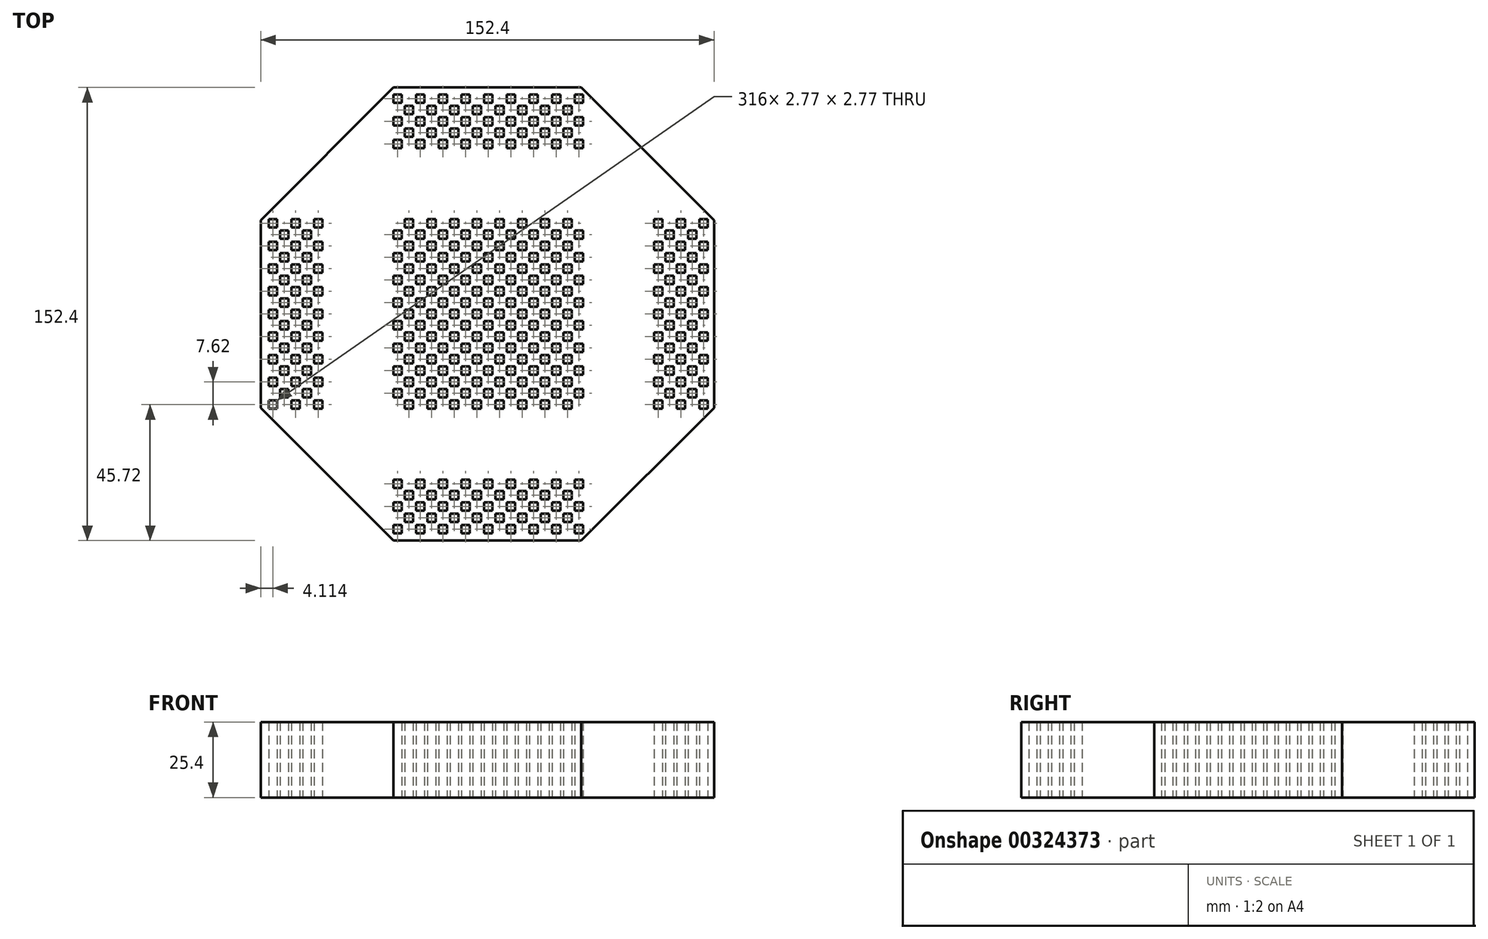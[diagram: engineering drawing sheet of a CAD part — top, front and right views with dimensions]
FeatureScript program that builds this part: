
annotation { "Feature Type Name" : "Feature", "Feature Type Description" : "" }
export const myFeature = defineFeature(function(context is Context, id is Id, definition is map)
    precondition{}
    {
        {
            var Q0;
            Q0=qCreatedBy(makeId("Top.planeOp"),FACE);
            var sketch = newSketch(context, id + "F0", { "sketchPlane" : qUnion([Q0])});
            skLineSegment(sketch, "E0.0", {"start": v(-31.56, 76.2) * mm, "end": v(31.56, 76.2) * mm});
            skLineSegment(sketch, "E0.1", {"start": v(31.56, 76.2) * mm, "end": v(76.2, 31.56) * mm});
            skLineSegment(sketch, "E0.2", {"start": v(76.2, 31.56) * mm, "end": v(76.2, -31.56) * mm});
            skLineSegment(sketch, "E0.3", {"start": v(76.2, -31.56) * mm, "end": v(31.56, -76.2) * mm});
            skLineSegment(sketch, "E0.4", {"start": v(31.56, -76.2) * mm, "end": v(-31.56, -76.2) * mm});
            skLineSegment(sketch, "E0.5", {"start": v(-31.56, -76.2) * mm, "end": v(-76.2, -31.56) * mm});
            skLineSegment(sketch, "E0.6", {"start": v(-76.2, -31.56) * mm, "end": v(-76.2, 31.56) * mm});
            skLineSegment(sketch, "E0.7", {"start": v(-76.2, 31.56) * mm, "end": v(-31.56, 76.2) * mm});
            skPoint(sketch, "E0.0.midPoint", {"position": v(0, 76.2) * mm});
            skPoint(sketch, "E0.cCircle.center.orphan", {"position": v(0, 0) * mm});
            skLineSegment(sketch, "E1.bottom", {"start": v(-31.56, 73.78) * mm, "end": v(-28.79, 73.78) * mm});
            skLineSegment(sketch, "E1.top", {"start": v(-31.56, 71) * mm, "end": v(-28.79, 71) * mm});
            skLineSegment(sketch, "E1.left", {"start": v(-31.56, 73.78) * mm, "end": v(-31.56, 71) * mm});
            skLineSegment(sketch, "E1.right", {"start": v(-28.79, 73.78) * mm, "end": v(-28.79, 71) * mm});
            skPoint(sketch, "E1.middle", {"position": v(-30.18, 72.4) * mm});
            skPoint(sketch, "E2.endSnap0", {"position": v(-30.18, 71) * mm});
            skLineSegment(sketch, "E3.bottom", {"start": v(-31.56, 66.16) * mm, "end": v(-28.79, 66.16) * mm});
            skLineSegment(sketch, "E3.top", {"start": v(-31.56, 63.38) * mm, "end": v(-28.79, 63.38) * mm});
            skLineSegment(sketch, "E3.left", {"start": v(-31.56, 66.16) * mm, "end": v(-31.56, 63.38) * mm});
            skLineSegment(sketch, "E3.right", {"start": v(-28.79, 66.16) * mm, "end": v(-28.79, 63.38) * mm});
            skPoint(sketch, "E3.middle", {"position": v(-30.18, 64.77) * mm});
            skLineSegment(sketch, "E4.1.0.0", {"start": v(-24.98, 69.97) * mm, "end": v(-24.98, 67.2) * mm});
            skPoint(sketch, "E4.1.0.1", {"position": v(-26.37, 68.58) * mm});
            skLineSegment(sketch, "E4.1.0.2", {"start": v(-27.75, 69.97) * mm, "end": v(-27.75, 67.2) * mm});
            skLineSegment(sketch, "E4.1.0.3", {"start": v(-27.75, 69.97) * mm, "end": v(-24.98, 69.97) * mm});
            skLineSegment(sketch, "E4.1.0.4", {"start": v(-27.75, 67.2) * mm, "end": v(-24.98, 67.2) * mm});
            skPoint(sketch, "E4.1.0.5", {"position": v(-22.56, 72.4) * mm});
            skLineSegment(sketch, "E4.1.0.6", {"start": v(-23.94, 73.78) * mm, "end": v(-21.17, 73.78) * mm});
            skPoint(sketch, "E4.1.0.7", {"position": v(-22.56, 71) * mm});
            skLineSegment(sketch, "E4.1.0.8", {"start": v(-23.94, 71) * mm, "end": v(-21.17, 71) * mm});
            skLineSegment(sketch, "E4.1.0.9", {"start": v(-23.94, 73.78) * mm, "end": v(-23.94, 71) * mm});
            skLineSegment(sketch, "E4.1.0.10", {"start": v(-21.17, 73.78) * mm, "end": v(-21.17, 71) * mm});
            skLineSegment(sketch, "E4.1.0.11", {"start": v(-23.94, 66.16) * mm, "end": v(-23.94, 63.38) * mm});
            skPoint(sketch, "E4.1.0.12", {"position": v(-22.56, 64.77) * mm});
            skLineSegment(sketch, "E4.1.0.13", {"start": v(-23.94, 63.38) * mm, "end": v(-21.17, 63.38) * mm});
            skLineSegment(sketch, "E4.1.0.14", {"start": v(-21.17, 66.16) * mm, "end": v(-21.17, 63.38) * mm});
            skLineSegment(sketch, "E4.1.0.15", {"start": v(-23.94, 66.16) * mm, "end": v(-21.17, 66.16) * mm});
            skLineSegment(sketch, "E4.2.0.0", {"start": v(-17.36, 69.97) * mm, "end": v(-17.36, 67.2) * mm});
            skPoint(sketch, "E4.2.0.1", {"position": v(-18.75, 68.58) * mm});
            skLineSegment(sketch, "E4.2.0.2", {"start": v(-20.13, 69.97) * mm, "end": v(-20.13, 67.2) * mm});
            skLineSegment(sketch, "E4.2.0.3", {"start": v(-20.13, 69.97) * mm, "end": v(-17.36, 69.97) * mm});
            skLineSegment(sketch, "E4.2.0.4", {"start": v(-20.13, 67.2) * mm, "end": v(-17.36, 67.2) * mm});
            skPoint(sketch, "E4.2.0.5", {"position": v(-14.94, 72.4) * mm});
            skLineSegment(sketch, "E4.2.0.6", {"start": v(-16.32, 73.78) * mm, "end": v(-13.55, 73.78) * mm});
            skPoint(sketch, "E4.2.0.7", {"position": v(-14.94, 71) * mm});
            skLineSegment(sketch, "E4.2.0.8", {"start": v(-16.32, 71) * mm, "end": v(-13.55, 71) * mm});
            skLineSegment(sketch, "E4.2.0.9", {"start": v(-16.32, 73.78) * mm, "end": v(-16.32, 71) * mm});
            skLineSegment(sketch, "E4.2.0.10", {"start": v(-13.55, 73.78) * mm, "end": v(-13.55, 71) * mm});
            skLineSegment(sketch, "E4.2.0.11", {"start": v(-16.32, 66.16) * mm, "end": v(-16.32, 63.38) * mm});
            skPoint(sketch, "E4.2.0.12", {"position": v(-14.94, 64.77) * mm});
            skLineSegment(sketch, "E4.2.0.13", {"start": v(-16.32, 63.38) * mm, "end": v(-13.55, 63.38) * mm});
            skLineSegment(sketch, "E4.2.0.14", {"start": v(-13.55, 66.16) * mm, "end": v(-13.55, 63.38) * mm});
            skLineSegment(sketch, "E4.2.0.15", {"start": v(-16.32, 66.16) * mm, "end": v(-13.55, 66.16) * mm});
            skLineSegment(sketch, "E4.3.0.0", {"start": v(-9.74, 69.97) * mm, "end": v(-9.74, 67.2) * mm});
            skPoint(sketch, "E4.3.0.1", {"position": v(-11.13, 68.58) * mm});
            skLineSegment(sketch, "E4.3.0.2", {"start": v(-12.51, 69.97) * mm, "end": v(-12.51, 67.2) * mm});
            skLineSegment(sketch, "E4.3.0.3", {"start": v(-12.51, 69.97) * mm, "end": v(-9.74, 69.97) * mm});
            skLineSegment(sketch, "E4.3.0.4", {"start": v(-12.51, 67.2) * mm, "end": v(-9.74, 67.2) * mm});
            skPoint(sketch, "E4.3.0.5", {"position": v(-7.32, 72.4) * mm});
            skLineSegment(sketch, "E4.3.0.6", {"start": v(-8.7, 73.78) * mm, "end": v(-5.93, 73.78) * mm});
            skPoint(sketch, "E4.3.0.7", {"position": v(-7.32, 71) * mm});
            skLineSegment(sketch, "E4.3.0.8", {"start": v(-8.7, 71) * mm, "end": v(-5.93, 71) * mm});
            skLineSegment(sketch, "E4.3.0.9", {"start": v(-8.7, 73.78) * mm, "end": v(-8.7, 71) * mm});
            skLineSegment(sketch, "E4.3.0.10", {"start": v(-5.93, 73.78) * mm, "end": v(-5.93, 71) * mm});
            skLineSegment(sketch, "E4.3.0.11", {"start": v(-8.7, 66.16) * mm, "end": v(-8.7, 63.38) * mm});
            skPoint(sketch, "E4.3.0.12", {"position": v(-7.32, 64.77) * mm});
            skLineSegment(sketch, "E4.3.0.13", {"start": v(-8.7, 63.38) * mm, "end": v(-5.93, 63.38) * mm});
            skLineSegment(sketch, "E4.3.0.14", {"start": v(-5.93, 66.16) * mm, "end": v(-5.93, 63.38) * mm});
            skLineSegment(sketch, "E4.3.0.15", {"start": v(-8.7, 66.16) * mm, "end": v(-5.93, 66.16) * mm});
            skLineSegment(sketch, "E4.4.0.0", {"start": v(-2.12, 69.97) * mm, "end": v(-2.12, 67.2) * mm});
            skPoint(sketch, "E4.4.0.1", {"position": v(-3.5, 68.58) * mm});
            skLineSegment(sketch, "E4.4.0.2", {"start": v(-4.9, 69.97) * mm, "end": v(-4.9, 67.2) * mm});
            skLineSegment(sketch, "E4.4.0.3", {"start": v(-4.9, 69.97) * mm, "end": v(-2.12, 69.97) * mm});
            skLineSegment(sketch, "E4.4.0.4", {"start": v(-4.9, 67.2) * mm, "end": v(-2.12, 67.2) * mm});
            skPoint(sketch, "E4.4.0.5", {"position": v(0.3, 72.4) * mm});
            skLineSegment(sketch, "E4.4.0.6", {"start": v(-1.08, 73.78) * mm, "end": v(1.7, 73.78) * mm});
            skPoint(sketch, "E4.4.0.7", {"position": v(0.3, 71) * mm});
            skLineSegment(sketch, "E4.4.0.8", {"start": v(-1.08, 71) * mm, "end": v(1.7, 71) * mm});
            skLineSegment(sketch, "E4.4.0.9", {"start": v(-1.08, 73.78) * mm, "end": v(-1.08, 71) * mm});
            skLineSegment(sketch, "E4.4.0.10", {"start": v(1.7, 73.78) * mm, "end": v(1.7, 71) * mm});
            skLineSegment(sketch, "E4.4.0.11", {"start": v(-1.08, 66.16) * mm, "end": v(-1.08, 63.38) * mm});
            skPoint(sketch, "E4.4.0.12", {"position": v(0.3, 64.77) * mm});
            skLineSegment(sketch, "E4.4.0.13", {"start": v(-1.08, 63.38) * mm, "end": v(1.7, 63.38) * mm});
            skLineSegment(sketch, "E4.4.0.14", {"start": v(1.7, 66.16) * mm, "end": v(1.7, 63.38) * mm});
            skLineSegment(sketch, "E4.4.0.15", {"start": v(-1.08, 66.16) * mm, "end": v(1.7, 66.16) * mm});
            skLineSegment(sketch, "E4.5.0.0", {"start": v(5.5, 69.97) * mm, "end": v(5.5, 67.2) * mm});
            skPoint(sketch, "E4.5.0.1", {"position": v(4.11, 68.58) * mm});
            skLineSegment(sketch, "E4.5.0.2", {"start": v(2.73, 69.97) * mm, "end": v(2.73, 67.2) * mm});
            skLineSegment(sketch, "E4.5.0.3", {"start": v(2.73, 69.97) * mm, "end": v(5.5, 69.97) * mm});
            skLineSegment(sketch, "E4.5.0.4", {"start": v(2.73, 67.2) * mm, "end": v(5.5, 67.2) * mm});
            skPoint(sketch, "E4.5.0.5", {"position": v(7.92, 72.4) * mm});
            skLineSegment(sketch, "E4.5.0.6", {"start": v(6.54, 73.78) * mm, "end": v(9.31, 73.78) * mm});
            skPoint(sketch, "E4.5.0.7", {"position": v(7.92, 71) * mm});
            skLineSegment(sketch, "E4.5.0.8", {"start": v(6.54, 71) * mm, "end": v(9.31, 71) * mm});
            skLineSegment(sketch, "E4.5.0.9", {"start": v(6.54, 73.78) * mm, "end": v(6.54, 71) * mm});
            skLineSegment(sketch, "E4.5.0.10", {"start": v(9.31, 73.78) * mm, "end": v(9.31, 71) * mm});
            skLineSegment(sketch, "E4.5.0.11", {"start": v(6.54, 66.16) * mm, "end": v(6.54, 63.38) * mm});
            skPoint(sketch, "E4.5.0.12", {"position": v(7.92, 64.77) * mm});
            skLineSegment(sketch, "E4.5.0.13", {"start": v(6.54, 63.38) * mm, "end": v(9.31, 63.38) * mm});
            skLineSegment(sketch, "E4.5.0.14", {"start": v(9.31, 66.16) * mm, "end": v(9.31, 63.38) * mm});
            skLineSegment(sketch, "E4.5.0.15", {"start": v(6.54, 66.16) * mm, "end": v(9.31, 66.16) * mm});
            skLineSegment(sketch, "E4.6.0.0", {"start": v(13.12, 69.97) * mm, "end": v(13.12, 67.2) * mm});
            skPoint(sketch, "E4.6.0.1", {"position": v(11.73, 68.58) * mm});
            skLineSegment(sketch, "E4.6.0.2", {"start": v(10.35, 69.97) * mm, "end": v(10.35, 67.2) * mm});
            skLineSegment(sketch, "E4.6.0.3", {"start": v(10.35, 69.97) * mm, "end": v(13.12, 69.97) * mm});
            skLineSegment(sketch, "E4.6.0.4", {"start": v(10.35, 67.2) * mm, "end": v(13.12, 67.2) * mm});
            skPoint(sketch, "E4.6.0.5", {"position": v(15.54, 72.4) * mm});
            skLineSegment(sketch, "E4.6.0.6", {"start": v(14.16, 73.78) * mm, "end": v(16.93, 73.78) * mm});
            skPoint(sketch, "E4.6.0.7", {"position": v(15.54, 71) * mm});
            skLineSegment(sketch, "E4.6.0.8", {"start": v(14.16, 71) * mm, "end": v(16.93, 71) * mm});
            skLineSegment(sketch, "E4.6.0.9", {"start": v(14.16, 73.78) * mm, "end": v(14.16, 71) * mm});
            skLineSegment(sketch, "E4.6.0.10", {"start": v(16.93, 73.78) * mm, "end": v(16.93, 71) * mm});
            skLineSegment(sketch, "E4.6.0.11", {"start": v(14.16, 66.16) * mm, "end": v(14.16, 63.38) * mm});
            skPoint(sketch, "E4.6.0.12", {"position": v(15.54, 64.77) * mm});
            skLineSegment(sketch, "E4.6.0.13", {"start": v(14.16, 63.38) * mm, "end": v(16.93, 63.38) * mm});
            skLineSegment(sketch, "E4.6.0.14", {"start": v(16.93, 66.16) * mm, "end": v(16.93, 63.38) * mm});
            skLineSegment(sketch, "E4.6.0.15", {"start": v(14.16, 66.16) * mm, "end": v(16.93, 66.16) * mm});
            skLineSegment(sketch, "E4.7.0.0", {"start": v(20.74, 69.97) * mm, "end": v(20.74, 67.2) * mm});
            skPoint(sketch, "E4.7.0.1", {"position": v(19.35, 68.58) * mm});
            skLineSegment(sketch, "E4.7.0.2", {"start": v(17.97, 69.97) * mm, "end": v(17.97, 67.2) * mm});
            skLineSegment(sketch, "E4.7.0.3", {"start": v(17.97, 69.97) * mm, "end": v(20.74, 69.97) * mm});
            skLineSegment(sketch, "E4.7.0.4", {"start": v(17.97, 67.2) * mm, "end": v(20.74, 67.2) * mm});
            skPoint(sketch, "E4.7.0.5", {"position": v(23.16, 72.4) * mm});
            skLineSegment(sketch, "E4.7.0.6", {"start": v(21.78, 73.78) * mm, "end": v(24.55, 73.78) * mm});
            skPoint(sketch, "E4.7.0.7", {"position": v(23.16, 71) * mm});
            skLineSegment(sketch, "E4.7.0.8", {"start": v(21.78, 71) * mm, "end": v(24.55, 71) * mm});
            skLineSegment(sketch, "E4.7.0.9", {"start": v(21.78, 73.78) * mm, "end": v(21.78, 71) * mm});
            skLineSegment(sketch, "E4.7.0.10", {"start": v(24.55, 73.78) * mm, "end": v(24.55, 71) * mm});
            skLineSegment(sketch, "E4.7.0.11", {"start": v(21.78, 66.16) * mm, "end": v(21.78, 63.38) * mm});
            skPoint(sketch, "E4.7.0.12", {"position": v(23.16, 64.77) * mm});
            skLineSegment(sketch, "E4.7.0.13", {"start": v(21.78, 63.38) * mm, "end": v(24.55, 63.38) * mm});
            skLineSegment(sketch, "E4.7.0.14", {"start": v(24.55, 66.16) * mm, "end": v(24.55, 63.38) * mm});
            skLineSegment(sketch, "E4.7.0.15", {"start": v(21.78, 66.16) * mm, "end": v(24.55, 66.16) * mm});
            skLineSegment(sketch, "E4.8.0.0", {"start": v(28.36, 69.97) * mm, "end": v(28.36, 67.2) * mm});
            skPoint(sketch, "E4.8.0.1", {"position": v(26.97, 68.58) * mm});
            skLineSegment(sketch, "E4.8.0.2", {"start": v(25.59, 69.97) * mm, "end": v(25.59, 67.2) * mm});
            skLineSegment(sketch, "E4.8.0.3", {"start": v(25.59, 69.97) * mm, "end": v(28.36, 69.97) * mm});
            skLineSegment(sketch, "E4.8.0.4", {"start": v(25.59, 67.2) * mm, "end": v(28.36, 67.2) * mm});
            skPoint(sketch, "E4.8.0.5", {"position": v(30.78, 72.4) * mm});
            skLineSegment(sketch, "E4.8.0.6", {"start": v(29.4, 73.78) * mm, "end": v(32.17, 73.78) * mm});
            skPoint(sketch, "E4.8.0.7", {"position": v(30.78, 71) * mm});
            skLineSegment(sketch, "E4.8.0.8", {"start": v(29.4, 71) * mm, "end": v(32.17, 71) * mm});
            skLineSegment(sketch, "E4.8.0.9", {"start": v(29.4, 73.78) * mm, "end": v(29.4, 71) * mm});
            skLineSegment(sketch, "E4.8.0.10", {"start": v(32.17, 73.78) * mm, "end": v(32.17, 71) * mm});
            skLineSegment(sketch, "E4.8.0.11", {"start": v(29.4, 66.16) * mm, "end": v(29.4, 63.38) * mm});
            skPoint(sketch, "E4.8.0.12", {"position": v(30.78, 64.77) * mm});
            skLineSegment(sketch, "E4.8.0.13", {"start": v(29.4, 63.38) * mm, "end": v(32.17, 63.38) * mm});
            skLineSegment(sketch, "E4.8.0.14", {"start": v(32.17, 66.16) * mm, "end": v(32.17, 63.38) * mm});
            skLineSegment(sketch, "E4.8.0.15", {"start": v(29.4, 66.16) * mm, "end": v(32.17, 66.16) * mm});
            skPoint(sketch, "E5.0.1.0", {"position": v(-11.13, 60.96) * mm});
            skPoint(sketch, "E5.0.1.1", {"position": v(19.35, 60.96) * mm});
            skPoint(sketch, "E5.0.1.2", {"position": v(23.16, 57.15) * mm});
            skPoint(sketch, "E5.0.1.3", {"position": v(11.73, 60.96) * mm});
            skPoint(sketch, "E5.0.1.4", {"position": v(-22.56, 57.15) * mm});
            skPoint(sketch, "E5.0.1.5", {"position": v(7.92, 57.15) * mm});
            skPoint(sketch, "E5.0.1.7", {"position": v(0.3, 57.15) * mm});
            skPoint(sketch, "E5.0.1.8", {"position": v(30.78, 57.15) * mm});
            skPoint(sketch, "E5.0.1.9", {"position": v(-30.18, 57.15) * mm});
            skPoint(sketch, "E5.0.1.10", {"position": v(-3.5, 60.96) * mm});
            skPoint(sketch, "E5.0.1.11", {"position": v(26.97, 60.96) * mm});
            skPoint(sketch, "E5.0.1.12", {"position": v(-7.32, 57.15) * mm});
            skPoint(sketch, "E5.0.1.13", {"position": v(-14.94, 57.15) * mm});
            skPoint(sketch, "E5.0.1.14", {"position": v(15.54, 57.15) * mm});
            skPoint(sketch, "E5.0.1.15", {"position": v(-18.75, 60.96) * mm});
            skPoint(sketch, "E5.0.1.17", {"position": v(-26.37, 60.96) * mm});
            skPoint(sketch, "E5.0.1.18", {"position": v(4.11, 60.96) * mm});
            skLineSegment(sketch, "E5.0.1.20", {"start": v(32.17, 58.54) * mm, "end": v(32.17, 55.76) * mm});
            skLineSegment(sketch, "E5.0.1.21", {"start": v(-20.13, 62.35) * mm, "end": v(-17.36, 62.35) * mm});
            skLineSegment(sketch, "E5.0.1.22", {"start": v(1.7, 58.54) * mm, "end": v(1.7, 55.76) * mm});
            skLineSegment(sketch, "E5.0.1.23", {"start": v(10.35, 62.35) * mm, "end": v(13.12, 62.35) * mm});
            skLineSegment(sketch, "E5.0.1.25", {"start": v(-28.79, 58.54) * mm, "end": v(-28.79, 55.76) * mm});
            skLineSegment(sketch, "E5.0.1.26", {"start": v(-31.56, 58.54) * mm, "end": v(-31.56, 55.76) * mm});
            skLineSegment(sketch, "E5.0.1.27", {"start": v(-31.56, 55.76) * mm, "end": v(-28.79, 55.76) * mm});
            skLineSegment(sketch, "E5.0.1.28", {"start": v(17.97, 59.57) * mm, "end": v(20.74, 59.57) * mm});
            skLineSegment(sketch, "E5.0.1.29", {"start": v(-23.94, 58.54) * mm, "end": v(-21.17, 58.54) * mm});
            skLineSegment(sketch, "E5.0.1.30", {"start": v(-12.51, 59.57) * mm, "end": v(-9.74, 59.57) * mm});
            skLineSegment(sketch, "E5.0.1.31", {"start": v(6.54, 58.54) * mm, "end": v(9.31, 58.54) * mm});
            skLineSegment(sketch, "E5.0.1.32", {"start": v(-21.17, 58.54) * mm, "end": v(-21.17, 55.76) * mm});
            skLineSegment(sketch, "E5.0.1.33", {"start": v(-12.51, 62.35) * mm, "end": v(-9.74, 62.35) * mm});
            skLineSegment(sketch, "E5.0.1.34", {"start": v(9.31, 58.54) * mm, "end": v(9.31, 55.76) * mm});
            skLineSegment(sketch, "E5.0.1.35", {"start": v(6.54, 58.54) * mm, "end": v(6.54, 55.76) * mm});
            skLineSegment(sketch, "E5.0.1.36", {"start": v(20.74, 62.35) * mm, "end": v(20.74, 59.57) * mm});
            skLineSegment(sketch, "E5.0.1.37", {"start": v(-23.94, 55.76) * mm, "end": v(-21.17, 55.76) * mm});
            skLineSegment(sketch, "E5.0.1.38", {"start": v(-12.51, 62.35) * mm, "end": v(-12.51, 59.57) * mm});
            skLineSegment(sketch, "E5.0.1.39", {"start": v(25.59, 59.57) * mm, "end": v(28.36, 59.57) * mm});
            skLineSegment(sketch, "E5.0.1.41", {"start": v(-4.9, 59.57) * mm, "end": v(-2.12, 59.57) * mm});
            skLineSegment(sketch, "E5.0.1.42", {"start": v(16.93, 58.54) * mm, "end": v(16.93, 55.76) * mm});
            skLineSegment(sketch, "E5.0.1.43", {"start": v(25.59, 62.35) * mm, "end": v(28.36, 62.35) * mm});
            skLineSegment(sketch, "E5.0.1.44", {"start": v(-13.55, 58.54) * mm, "end": v(-13.55, 55.76) * mm});
            skLineSegment(sketch, "E5.0.1.45", {"start": v(-4.9, 62.35) * mm, "end": v(-2.12, 62.35) * mm});
            skLineSegment(sketch, "E5.0.1.46", {"start": v(14.16, 55.76) * mm, "end": v(16.93, 55.76) * mm});
            skLineSegment(sketch, "E5.0.1.47", {"start": v(25.59, 62.35) * mm, "end": v(25.59, 59.57) * mm});
            skLineSegment(sketch, "E5.0.1.49", {"start": v(-16.32, 55.76) * mm, "end": v(-13.55, 55.76) * mm});
            skLineSegment(sketch, "E5.0.1.50", {"start": v(-4.9, 62.35) * mm, "end": v(-4.9, 59.57) * mm});
            skLineSegment(sketch, "E5.0.1.51", {"start": v(14.16, 58.54) * mm, "end": v(14.16, 55.76) * mm});
            skLineSegment(sketch, "E5.0.1.52", {"start": v(28.36, 62.35) * mm, "end": v(28.36, 59.57) * mm});
            skLineSegment(sketch, "E5.0.1.54", {"start": v(-16.32, 58.54) * mm, "end": v(-16.32, 55.76) * mm});
            skLineSegment(sketch, "E5.0.1.55", {"start": v(-2.12, 62.35) * mm, "end": v(-2.12, 59.57) * mm});
            skLineSegment(sketch, "E5.0.1.56", {"start": v(2.73, 59.57) * mm, "end": v(5.5, 59.57) * mm});
            skLineSegment(sketch, "E5.0.1.57", {"start": v(21.78, 58.54) * mm, "end": v(24.55, 58.54) * mm});
            skLineSegment(sketch, "E5.0.1.59", {"start": v(-27.75, 59.57) * mm, "end": v(-24.98, 59.57) * mm});
            skLineSegment(sketch, "E5.0.1.60", {"start": v(-8.7, 58.54) * mm, "end": v(-5.93, 58.54) * mm});
            skLineSegment(sketch, "E5.0.1.61", {"start": v(24.55, 58.54) * mm, "end": v(24.55, 55.76) * mm});
            skLineSegment(sketch, "E5.0.1.63", {"start": v(-5.93, 58.54) * mm, "end": v(-5.93, 55.76) * mm});
            skLineSegment(sketch, "E5.0.1.64", {"start": v(2.73, 62.35) * mm, "end": v(5.5, 62.35) * mm});
            skLineSegment(sketch, "E5.0.1.65", {"start": v(-27.75, 62.35) * mm, "end": v(-24.98, 62.35) * mm});
            skLineSegment(sketch, "E5.0.1.66", {"start": v(21.78, 55.76) * mm, "end": v(24.55, 55.76) * mm});
            skLineSegment(sketch, "E5.0.1.68", {"start": v(-8.7, 55.76) * mm, "end": v(-5.93, 55.76) * mm});
            skLineSegment(sketch, "E5.0.1.69", {"start": v(2.73, 62.35) * mm, "end": v(2.73, 59.57) * mm});
            skLineSegment(sketch, "E5.0.1.70", {"start": v(-27.75, 62.35) * mm, "end": v(-27.75, 59.57) * mm});
            skLineSegment(sketch, "E5.0.1.71", {"start": v(21.78, 58.54) * mm, "end": v(21.78, 55.76) * mm});
            skLineSegment(sketch, "E5.0.1.73", {"start": v(-8.7, 58.54) * mm, "end": v(-8.7, 55.76) * mm});
            skLineSegment(sketch, "E5.0.1.74", {"start": v(5.5, 62.35) * mm, "end": v(5.5, 59.57) * mm});
            skLineSegment(sketch, "E5.0.1.75", {"start": v(-24.98, 62.35) * mm, "end": v(-24.98, 59.57) * mm});
            skLineSegment(sketch, "E5.0.1.76", {"start": v(29.4, 58.54) * mm, "end": v(32.17, 58.54) * mm});
            skLineSegment(sketch, "E5.0.1.77", {"start": v(-20.13, 59.57) * mm, "end": v(-17.36, 59.57) * mm});
            skLineSegment(sketch, "E5.0.1.78", {"start": v(-1.08, 58.54) * mm, "end": v(1.7, 58.54) * mm});
            skLineSegment(sketch, "E5.0.1.79", {"start": v(10.35, 59.57) * mm, "end": v(13.12, 59.57) * mm});
            skLineSegment(sketch, "E5.0.1.80", {"start": v(29.4, 55.76) * mm, "end": v(32.17, 55.76) * mm});
            skLineSegment(sketch, "E5.0.1.81", {"start": v(-20.13, 62.35) * mm, "end": v(-20.13, 59.57) * mm});
            skLineSegment(sketch, "E5.0.1.82", {"start": v(-1.08, 55.76) * mm, "end": v(1.7, 55.76) * mm});
            skLineSegment(sketch, "E5.0.1.83", {"start": v(10.35, 62.35) * mm, "end": v(10.35, 59.57) * mm});
            skLineSegment(sketch, "E5.0.1.85", {"start": v(-17.36, 62.35) * mm, "end": v(-17.36, 59.57) * mm});
            skLineSegment(sketch, "E5.0.1.86", {"start": v(-1.08, 58.54) * mm, "end": v(-1.08, 55.76) * mm});
            skLineSegment(sketch, "E5.0.1.87", {"start": v(13.12, 62.35) * mm, "end": v(13.12, 59.57) * mm});
            skLineSegment(sketch, "E5.0.1.88", {"start": v(29.4, 58.54) * mm, "end": v(29.4, 55.76) * mm});
            skLineSegment(sketch, "E5.0.1.89", {"start": v(-31.56, 58.54) * mm, "end": v(-28.79, 58.54) * mm});
            skLineSegment(sketch, "E5.0.1.90", {"start": v(17.97, 62.35) * mm, "end": v(20.74, 62.35) * mm});
            skLineSegment(sketch, "E5.0.1.91", {"start": v(-23.94, 58.54) * mm, "end": v(-23.94, 55.76) * mm});
            skLineSegment(sketch, "E5.0.1.92", {"start": v(-9.74, 62.35) * mm, "end": v(-9.74, 59.57) * mm});
            skLineSegment(sketch, "E5.0.1.93", {"start": v(17.97, 62.35) * mm, "end": v(17.97, 59.57) * mm});
            skLineSegment(sketch, "E5.0.1.94", {"start": v(6.54, 55.76) * mm, "end": v(9.31, 55.76) * mm});
            skLineSegment(sketch, "E5.0.1.95", {"start": v(14.16, 58.54) * mm, "end": v(16.93, 58.54) * mm});
            skLineSegment(sketch, "E5.0.1.96", {"start": v(-16.32, 58.54) * mm, "end": v(-13.55, 58.54) * mm});
            skPoint(sketch, "E5.0.5.0", {"position": v(-11.13, 30.48) * mm});
            skPoint(sketch, "E5.0.5.1", {"position": v(19.35, 30.48) * mm});
            skPoint(sketch, "E5.0.5.2", {"position": v(23.16, 26.67) * mm});
            skPoint(sketch, "E5.0.5.3", {"position": v(11.73, 30.48) * mm});
            skPoint(sketch, "E5.0.5.4", {"position": v(-22.56, 26.67) * mm});
            skPoint(sketch, "E5.0.5.5", {"position": v(7.92, 26.67) * mm});
            skPoint(sketch, "E5.0.5.7", {"position": v(0.3, 26.67) * mm});
            skPoint(sketch, "E5.0.5.8", {"position": v(30.78, 26.67) * mm});
            skPoint(sketch, "E5.0.5.9", {"position": v(-30.18, 26.67) * mm});
            skPoint(sketch, "E5.0.5.10", {"position": v(-3.5, 30.48) * mm});
            skPoint(sketch, "E5.0.5.11", {"position": v(26.97, 30.48) * mm});
            skPoint(sketch, "E5.0.5.12", {"position": v(-7.32, 26.67) * mm});
            skPoint(sketch, "E5.0.5.13", {"position": v(-14.94, 26.67) * mm});
            skPoint(sketch, "E5.0.5.14", {"position": v(15.54, 26.67) * mm});
            skPoint(sketch, "E5.0.5.15", {"position": v(-18.75, 30.48) * mm});
            skPoint(sketch, "E5.0.5.17", {"position": v(-26.37, 30.48) * mm});
            skPoint(sketch, "E5.0.5.18", {"position": v(4.11, 30.48) * mm});
            skLineSegment(sketch, "E5.0.5.20", {"start": v(32.17, 28.06) * mm, "end": v(32.17, 25.28) * mm});
            skLineSegment(sketch, "E5.0.5.21", {"start": v(-20.13, 31.87) * mm, "end": v(-17.36, 31.87) * mm});
            skLineSegment(sketch, "E5.0.5.22", {"start": v(1.7, 28.06) * mm, "end": v(1.7, 25.28) * mm});
            skLineSegment(sketch, "E5.0.5.23", {"start": v(10.35, 31.87) * mm, "end": v(13.12, 31.87) * mm});
            skLineSegment(sketch, "E5.0.5.25", {"start": v(-28.79, 28.06) * mm, "end": v(-28.79, 25.28) * mm});
            skLineSegment(sketch, "E5.0.5.26", {"start": v(-31.56, 28.06) * mm, "end": v(-31.56, 25.28) * mm});
            skLineSegment(sketch, "E5.0.5.27", {"start": v(-31.56, 25.28) * mm, "end": v(-28.79, 25.28) * mm});
            skLineSegment(sketch, "E5.0.5.28", {"start": v(17.97, 29.1) * mm, "end": v(20.74, 29.1) * mm});
            skLineSegment(sketch, "E5.0.5.29", {"start": v(-23.94, 28.06) * mm, "end": v(-21.17, 28.06) * mm});
            skLineSegment(sketch, "E5.0.5.30", {"start": v(-12.51, 29.1) * mm, "end": v(-9.74, 29.1) * mm});
            skLineSegment(sketch, "E5.0.5.31", {"start": v(6.54, 28.06) * mm, "end": v(9.31, 28.06) * mm});
            skLineSegment(sketch, "E5.0.5.32", {"start": v(-21.17, 28.06) * mm, "end": v(-21.17, 25.28) * mm});
            skLineSegment(sketch, "E5.0.5.33", {"start": v(-12.51, 31.87) * mm, "end": v(-9.74, 31.87) * mm});
            skLineSegment(sketch, "E5.0.5.34", {"start": v(9.31, 28.06) * mm, "end": v(9.31, 25.28) * mm});
            skLineSegment(sketch, "E5.0.5.35", {"start": v(6.54, 28.06) * mm, "end": v(6.54, 25.28) * mm});
            skLineSegment(sketch, "E5.0.5.36", {"start": v(20.74, 31.87) * mm, "end": v(20.74, 29.1) * mm});
            skLineSegment(sketch, "E5.0.5.37", {"start": v(-23.94, 25.28) * mm, "end": v(-21.17, 25.28) * mm});
            skLineSegment(sketch, "E5.0.5.38", {"start": v(-12.51, 31.87) * mm, "end": v(-12.51, 29.1) * mm});
            skLineSegment(sketch, "E5.0.5.39", {"start": v(25.59, 29.1) * mm, "end": v(28.36, 29.1) * mm});
            skLineSegment(sketch, "E5.0.5.41", {"start": v(-4.9, 29.1) * mm, "end": v(-2.12, 29.1) * mm});
            skLineSegment(sketch, "E5.0.5.42", {"start": v(16.93, 28.06) * mm, "end": v(16.93, 25.28) * mm});
            skLineSegment(sketch, "E5.0.5.43", {"start": v(25.59, 31.87) * mm, "end": v(28.36, 31.87) * mm});
            skLineSegment(sketch, "E5.0.5.44", {"start": v(-13.55, 28.06) * mm, "end": v(-13.55, 25.28) * mm});
            skLineSegment(sketch, "E5.0.5.45", {"start": v(-4.9, 31.87) * mm, "end": v(-2.12, 31.87) * mm});
            skLineSegment(sketch, "E5.0.5.46", {"start": v(14.16, 25.28) * mm, "end": v(16.93, 25.28) * mm});
            skLineSegment(sketch, "E5.0.5.47", {"start": v(25.59, 31.87) * mm, "end": v(25.59, 29.1) * mm});
            skLineSegment(sketch, "E5.0.5.49", {"start": v(-16.32, 25.28) * mm, "end": v(-13.55, 25.28) * mm});
            skLineSegment(sketch, "E5.0.5.50", {"start": v(-4.9, 31.87) * mm, "end": v(-4.9, 29.1) * mm});
            skLineSegment(sketch, "E5.0.5.51", {"start": v(14.16, 28.06) * mm, "end": v(14.16, 25.28) * mm});
            skLineSegment(sketch, "E5.0.5.52", {"start": v(28.36, 31.87) * mm, "end": v(28.36, 29.1) * mm});
            skLineSegment(sketch, "E5.0.5.54", {"start": v(-16.32, 28.06) * mm, "end": v(-16.32, 25.28) * mm});
            skLineSegment(sketch, "E5.0.5.55", {"start": v(-2.12, 31.87) * mm, "end": v(-2.12, 29.1) * mm});
            skLineSegment(sketch, "E5.0.5.56", {"start": v(2.73, 29.1) * mm, "end": v(5.5, 29.1) * mm});
            skLineSegment(sketch, "E5.0.5.57", {"start": v(21.78, 28.06) * mm, "end": v(24.55, 28.06) * mm});
            skLineSegment(sketch, "E5.0.5.59", {"start": v(-27.75, 29.1) * mm, "end": v(-24.98, 29.1) * mm});
            skLineSegment(sketch, "E5.0.5.60", {"start": v(-8.7, 28.06) * mm, "end": v(-5.93, 28.06) * mm});
            skLineSegment(sketch, "E5.0.5.61", {"start": v(24.55, 28.06) * mm, "end": v(24.55, 25.28) * mm});
            skLineSegment(sketch, "E5.0.5.63", {"start": v(-5.93, 28.06) * mm, "end": v(-5.93, 25.28) * mm});
            skLineSegment(sketch, "E5.0.5.64", {"start": v(2.73, 31.87) * mm, "end": v(5.5, 31.87) * mm});
            skLineSegment(sketch, "E5.0.5.65", {"start": v(-27.75, 31.87) * mm, "end": v(-24.98, 31.87) * mm});
            skLineSegment(sketch, "E5.0.5.66", {"start": v(21.78, 25.28) * mm, "end": v(24.55, 25.28) * mm});
            skLineSegment(sketch, "E5.0.5.68", {"start": v(-8.7, 25.28) * mm, "end": v(-5.93, 25.28) * mm});
            skLineSegment(sketch, "E5.0.5.69", {"start": v(2.73, 31.87) * mm, "end": v(2.73, 29.1) * mm});
            skLineSegment(sketch, "E5.0.5.70", {"start": v(-27.75, 31.87) * mm, "end": v(-27.75, 29.1) * mm});
            skLineSegment(sketch, "E5.0.5.71", {"start": v(21.78, 28.06) * mm, "end": v(21.78, 25.28) * mm});
            skLineSegment(sketch, "E5.0.5.73", {"start": v(-8.7, 28.06) * mm, "end": v(-8.7, 25.28) * mm});
            skLineSegment(sketch, "E5.0.5.74", {"start": v(5.5, 31.87) * mm, "end": v(5.5, 29.1) * mm});
            skLineSegment(sketch, "E5.0.5.75", {"start": v(-24.98, 31.87) * mm, "end": v(-24.98, 29.1) * mm});
            skLineSegment(sketch, "E5.0.5.76", {"start": v(29.4, 28.06) * mm, "end": v(32.17, 28.06) * mm});
            skLineSegment(sketch, "E5.0.5.77", {"start": v(-20.13, 29.1) * mm, "end": v(-17.36, 29.1) * mm});
            skLineSegment(sketch, "E5.0.5.78", {"start": v(-1.08, 28.06) * mm, "end": v(1.7, 28.06) * mm});
            skLineSegment(sketch, "E5.0.5.79", {"start": v(10.35, 29.1) * mm, "end": v(13.12, 29.1) * mm});
            skLineSegment(sketch, "E5.0.5.80", {"start": v(29.4, 25.28) * mm, "end": v(32.17, 25.28) * mm});
            skLineSegment(sketch, "E5.0.5.81", {"start": v(-20.13, 31.87) * mm, "end": v(-20.13, 29.1) * mm});
            skLineSegment(sketch, "E5.0.5.82", {"start": v(-1.08, 25.28) * mm, "end": v(1.7, 25.28) * mm});
            skLineSegment(sketch, "E5.0.5.83", {"start": v(10.35, 31.87) * mm, "end": v(10.35, 29.1) * mm});
            skLineSegment(sketch, "E5.0.5.85", {"start": v(-17.36, 31.87) * mm, "end": v(-17.36, 29.1) * mm});
            skLineSegment(sketch, "E5.0.5.86", {"start": v(-1.08, 28.06) * mm, "end": v(-1.08, 25.28) * mm});
            skLineSegment(sketch, "E5.0.5.87", {"start": v(13.12, 31.87) * mm, "end": v(13.12, 29.1) * mm});
            skLineSegment(sketch, "E5.0.5.88", {"start": v(29.4, 28.06) * mm, "end": v(29.4, 25.28) * mm});
            skLineSegment(sketch, "E5.0.5.89", {"start": v(-31.56, 28.06) * mm, "end": v(-28.79, 28.06) * mm});
            skLineSegment(sketch, "E5.0.5.90", {"start": v(17.97, 31.87) * mm, "end": v(20.74, 31.87) * mm});
            skLineSegment(sketch, "E5.0.5.91", {"start": v(-23.94, 28.06) * mm, "end": v(-23.94, 25.28) * mm});
            skLineSegment(sketch, "E5.0.5.92", {"start": v(-9.74, 31.87) * mm, "end": v(-9.74, 29.1) * mm});
            skLineSegment(sketch, "E5.0.5.93", {"start": v(17.97, 31.87) * mm, "end": v(17.97, 29.1) * mm});
            skLineSegment(sketch, "E5.0.5.94", {"start": v(6.54, 25.28) * mm, "end": v(9.31, 25.28) * mm});
            skLineSegment(sketch, "E5.0.5.95", {"start": v(14.16, 28.06) * mm, "end": v(16.93, 28.06) * mm});
            skLineSegment(sketch, "E5.0.5.96", {"start": v(-16.32, 28.06) * mm, "end": v(-13.55, 28.06) * mm});
            skPoint(sketch, "E5.0.6.0", {"position": v(-11.13, 22.86) * mm});
            skPoint(sketch, "E5.0.6.1", {"position": v(19.35, 22.86) * mm});
            skPoint(sketch, "E5.0.6.2", {"position": v(23.16, 19.05) * mm});
            skPoint(sketch, "E5.0.6.3", {"position": v(11.73, 22.86) * mm});
            skPoint(sketch, "E5.0.6.4", {"position": v(-22.56, 19.05) * mm});
            skPoint(sketch, "E5.0.6.5", {"position": v(7.92, 19.05) * mm});
            skPoint(sketch, "E5.0.6.7", {"position": v(0.3, 19.05) * mm});
            skPoint(sketch, "E5.0.6.8", {"position": v(30.78, 19.05) * mm});
            skPoint(sketch, "E5.0.6.9", {"position": v(-30.18, 19.05) * mm});
            skPoint(sketch, "E5.0.6.10", {"position": v(-3.5, 22.86) * mm});
            skPoint(sketch, "E5.0.6.11", {"position": v(26.97, 22.86) * mm});
            skPoint(sketch, "E5.0.6.12", {"position": v(-7.32, 19.05) * mm});
            skPoint(sketch, "E5.0.6.13", {"position": v(-14.94, 19.05) * mm});
            skPoint(sketch, "E5.0.6.14", {"position": v(15.54, 19.05) * mm});
            skPoint(sketch, "E5.0.6.15", {"position": v(-18.75, 22.86) * mm});
            skPoint(sketch, "E5.0.6.17", {"position": v(-26.37, 22.86) * mm});
            skPoint(sketch, "E5.0.6.18", {"position": v(4.11, 22.86) * mm});
            skLineSegment(sketch, "E5.0.6.20", {"start": v(32.17, 20.44) * mm, "end": v(32.17, 17.66) * mm});
            skLineSegment(sketch, "E5.0.6.21", {"start": v(-20.13, 24.25) * mm, "end": v(-17.36, 24.25) * mm});
            skLineSegment(sketch, "E5.0.6.22", {"start": v(1.7, 20.44) * mm, "end": v(1.7, 17.66) * mm});
            skLineSegment(sketch, "E5.0.6.23", {"start": v(10.35, 24.25) * mm, "end": v(13.12, 24.25) * mm});
            skLineSegment(sketch, "E5.0.6.25", {"start": v(-28.79, 20.44) * mm, "end": v(-28.79, 17.66) * mm});
            skLineSegment(sketch, "E5.0.6.26", {"start": v(-31.56, 20.44) * mm, "end": v(-31.56, 17.66) * mm});
            skLineSegment(sketch, "E5.0.6.27", {"start": v(-31.56, 17.66) * mm, "end": v(-28.79, 17.66) * mm});
            skLineSegment(sketch, "E5.0.6.28", {"start": v(17.97, 21.47) * mm, "end": v(20.74, 21.47) * mm});
            skLineSegment(sketch, "E5.0.6.29", {"start": v(-23.94, 20.44) * mm, "end": v(-21.17, 20.44) * mm});
            skLineSegment(sketch, "E5.0.6.30", {"start": v(-12.51, 21.47) * mm, "end": v(-9.74, 21.47) * mm});
            skLineSegment(sketch, "E5.0.6.31", {"start": v(6.54, 20.44) * mm, "end": v(9.31, 20.44) * mm});
            skLineSegment(sketch, "E5.0.6.32", {"start": v(-21.17, 20.44) * mm, "end": v(-21.17, 17.66) * mm});
            skLineSegment(sketch, "E5.0.6.33", {"start": v(-12.51, 24.25) * mm, "end": v(-9.74, 24.25) * mm});
            skLineSegment(sketch, "E5.0.6.34", {"start": v(9.31, 20.44) * mm, "end": v(9.31, 17.66) * mm});
            skLineSegment(sketch, "E5.0.6.35", {"start": v(6.54, 20.44) * mm, "end": v(6.54, 17.66) * mm});
            skLineSegment(sketch, "E5.0.6.36", {"start": v(20.74, 24.25) * mm, "end": v(20.74, 21.47) * mm});
            skLineSegment(sketch, "E5.0.6.37", {"start": v(-23.94, 17.66) * mm, "end": v(-21.17, 17.66) * mm});
            skLineSegment(sketch, "E5.0.6.38", {"start": v(-12.51, 24.25) * mm, "end": v(-12.51, 21.47) * mm});
            skLineSegment(sketch, "E5.0.6.39", {"start": v(25.59, 21.47) * mm, "end": v(28.36, 21.47) * mm});
            skLineSegment(sketch, "E5.0.6.41", {"start": v(-4.9, 21.47) * mm, "end": v(-2.12, 21.47) * mm});
            skLineSegment(sketch, "E5.0.6.42", {"start": v(16.93, 20.44) * mm, "end": v(16.93, 17.66) * mm});
            skLineSegment(sketch, "E5.0.6.43", {"start": v(25.59, 24.25) * mm, "end": v(28.36, 24.25) * mm});
            skLineSegment(sketch, "E5.0.6.44", {"start": v(-13.55, 20.44) * mm, "end": v(-13.55, 17.66) * mm});
            skLineSegment(sketch, "E5.0.6.45", {"start": v(-4.9, 24.25) * mm, "end": v(-2.12, 24.25) * mm});
            skLineSegment(sketch, "E5.0.6.46", {"start": v(14.16, 17.66) * mm, "end": v(16.93, 17.66) * mm});
            skLineSegment(sketch, "E5.0.6.47", {"start": v(25.59, 24.25) * mm, "end": v(25.59, 21.47) * mm});
            skLineSegment(sketch, "E5.0.6.49", {"start": v(-16.32, 17.66) * mm, "end": v(-13.55, 17.66) * mm});
            skLineSegment(sketch, "E5.0.6.50", {"start": v(-4.9, 24.25) * mm, "end": v(-4.9, 21.47) * mm});
            skLineSegment(sketch, "E5.0.6.51", {"start": v(14.16, 20.44) * mm, "end": v(14.16, 17.66) * mm});
            skLineSegment(sketch, "E5.0.6.52", {"start": v(28.36, 24.25) * mm, "end": v(28.36, 21.47) * mm});
            skLineSegment(sketch, "E5.0.6.54", {"start": v(-16.32, 20.44) * mm, "end": v(-16.32, 17.66) * mm});
            skLineSegment(sketch, "E5.0.6.55", {"start": v(-2.12, 24.25) * mm, "end": v(-2.12, 21.47) * mm});
            skLineSegment(sketch, "E5.0.6.56", {"start": v(2.73, 21.47) * mm, "end": v(5.5, 21.47) * mm});
            skLineSegment(sketch, "E5.0.6.57", {"start": v(21.78, 20.44) * mm, "end": v(24.55, 20.44) * mm});
            skLineSegment(sketch, "E5.0.6.59", {"start": v(-27.75, 21.47) * mm, "end": v(-24.98, 21.47) * mm});
            skLineSegment(sketch, "E5.0.6.60", {"start": v(-8.7, 20.44) * mm, "end": v(-5.93, 20.44) * mm});
            skLineSegment(sketch, "E5.0.6.61", {"start": v(24.55, 20.44) * mm, "end": v(24.55, 17.66) * mm});
            skLineSegment(sketch, "E5.0.6.63", {"start": v(-5.93, 20.44) * mm, "end": v(-5.93, 17.66) * mm});
            skLineSegment(sketch, "E5.0.6.64", {"start": v(2.73, 24.25) * mm, "end": v(5.5, 24.25) * mm});
            skLineSegment(sketch, "E5.0.6.65", {"start": v(-27.75, 24.25) * mm, "end": v(-24.98, 24.25) * mm});
            skLineSegment(sketch, "E5.0.6.66", {"start": v(21.78, 17.66) * mm, "end": v(24.55, 17.66) * mm});
            skLineSegment(sketch, "E5.0.6.68", {"start": v(-8.7, 17.66) * mm, "end": v(-5.93, 17.66) * mm});
            skLineSegment(sketch, "E5.0.6.69", {"start": v(2.73, 24.25) * mm, "end": v(2.73, 21.47) * mm});
            skLineSegment(sketch, "E5.0.6.70", {"start": v(-27.75, 24.25) * mm, "end": v(-27.75, 21.47) * mm});
            skLineSegment(sketch, "E5.0.6.71", {"start": v(21.78, 20.44) * mm, "end": v(21.78, 17.66) * mm});
            skLineSegment(sketch, "E5.0.6.73", {"start": v(-8.7, 20.44) * mm, "end": v(-8.7, 17.66) * mm});
            skLineSegment(sketch, "E5.0.6.74", {"start": v(5.5, 24.25) * mm, "end": v(5.5, 21.47) * mm});
            skLineSegment(sketch, "E5.0.6.75", {"start": v(-24.98, 24.25) * mm, "end": v(-24.98, 21.47) * mm});
            skLineSegment(sketch, "E5.0.6.76", {"start": v(29.4, 20.44) * mm, "end": v(32.17, 20.44) * mm});
            skLineSegment(sketch, "E5.0.6.77", {"start": v(-20.13, 21.47) * mm, "end": v(-17.36, 21.47) * mm});
            skLineSegment(sketch, "E5.0.6.78", {"start": v(-1.08, 20.44) * mm, "end": v(1.7, 20.44) * mm});
            skLineSegment(sketch, "E5.0.6.79", {"start": v(10.35, 21.47) * mm, "end": v(13.12, 21.47) * mm});
            skLineSegment(sketch, "E5.0.6.80", {"start": v(29.4, 17.66) * mm, "end": v(32.17, 17.66) * mm});
            skLineSegment(sketch, "E5.0.6.81", {"start": v(-20.13, 24.25) * mm, "end": v(-20.13, 21.47) * mm});
            skLineSegment(sketch, "E5.0.6.82", {"start": v(-1.08, 17.66) * mm, "end": v(1.7, 17.66) * mm});
            skLineSegment(sketch, "E5.0.6.83", {"start": v(10.35, 24.25) * mm, "end": v(10.35, 21.47) * mm});
            skLineSegment(sketch, "E5.0.6.85", {"start": v(-17.36, 24.25) * mm, "end": v(-17.36, 21.47) * mm});
            skLineSegment(sketch, "E5.0.6.86", {"start": v(-1.08, 20.44) * mm, "end": v(-1.08, 17.66) * mm});
            skLineSegment(sketch, "E5.0.6.87", {"start": v(13.12, 24.25) * mm, "end": v(13.12, 21.47) * mm});
            skLineSegment(sketch, "E5.0.6.88", {"start": v(29.4, 20.44) * mm, "end": v(29.4, 17.66) * mm});
            skLineSegment(sketch, "E5.0.6.89", {"start": v(-31.56, 20.44) * mm, "end": v(-28.79, 20.44) * mm});
            skLineSegment(sketch, "E5.0.6.90", {"start": v(17.97, 24.25) * mm, "end": v(20.74, 24.25) * mm});
            skLineSegment(sketch, "E5.0.6.91", {"start": v(-23.94, 20.44) * mm, "end": v(-23.94, 17.66) * mm});
            skLineSegment(sketch, "E5.0.6.92", {"start": v(-9.74, 24.25) * mm, "end": v(-9.74, 21.47) * mm});
            skLineSegment(sketch, "E5.0.6.93", {"start": v(17.97, 24.25) * mm, "end": v(17.97, 21.47) * mm});
            skLineSegment(sketch, "E5.0.6.94", {"start": v(6.54, 17.66) * mm, "end": v(9.31, 17.66) * mm});
            skLineSegment(sketch, "E5.0.6.95", {"start": v(14.16, 20.44) * mm, "end": v(16.93, 20.44) * mm});
            skLineSegment(sketch, "E5.0.6.96", {"start": v(-16.32, 20.44) * mm, "end": v(-13.55, 20.44) * mm});
            skPoint(sketch, "E5.0.7.0", {"position": v(-11.13, 15.24) * mm});
            skPoint(sketch, "E5.0.7.1", {"position": v(19.35, 15.24) * mm});
            skPoint(sketch, "E5.0.7.2", {"position": v(23.16, 11.43) * mm});
            skPoint(sketch, "E5.0.7.3", {"position": v(11.73, 15.24) * mm});
            skPoint(sketch, "E5.0.7.4", {"position": v(-22.56, 11.43) * mm});
            skPoint(sketch, "E5.0.7.5", {"position": v(7.92, 11.43) * mm});
            skPoint(sketch, "E5.0.7.7", {"position": v(0.3, 11.43) * mm});
            skPoint(sketch, "E5.0.7.8", {"position": v(30.78, 11.43) * mm});
            skPoint(sketch, "E5.0.7.9", {"position": v(-30.18, 11.43) * mm});
            skPoint(sketch, "E5.0.7.10", {"position": v(-3.5, 15.24) * mm});
            skPoint(sketch, "E5.0.7.11", {"position": v(26.97, 15.24) * mm});
            skPoint(sketch, "E5.0.7.12", {"position": v(-7.32, 11.43) * mm});
            skPoint(sketch, "E5.0.7.13", {"position": v(-14.94, 11.43) * mm});
            skPoint(sketch, "E5.0.7.14", {"position": v(15.54, 11.43) * mm});
            skPoint(sketch, "E5.0.7.15", {"position": v(-18.75, 15.24) * mm});
            skPoint(sketch, "E5.0.7.17", {"position": v(-26.37, 15.24) * mm});
            skPoint(sketch, "E5.0.7.18", {"position": v(4.11, 15.24) * mm});
            skLineSegment(sketch, "E5.0.7.20", {"start": v(32.17, 12.82) * mm, "end": v(32.17, 10.04) * mm});
            skLineSegment(sketch, "E5.0.7.21", {"start": v(-20.13, 16.63) * mm, "end": v(-17.36, 16.63) * mm});
            skLineSegment(sketch, "E5.0.7.22", {"start": v(1.7, 12.82) * mm, "end": v(1.7, 10.04) * mm});
            skLineSegment(sketch, "E5.0.7.23", {"start": v(10.35, 16.63) * mm, "end": v(13.12, 16.63) * mm});
            skLineSegment(sketch, "E5.0.7.25", {"start": v(-28.79, 12.82) * mm, "end": v(-28.79, 10.04) * mm});
            skLineSegment(sketch, "E5.0.7.26", {"start": v(-31.56, 12.82) * mm, "end": v(-31.56, 10.04) * mm});
            skLineSegment(sketch, "E5.0.7.27", {"start": v(-31.56, 10.04) * mm, "end": v(-28.79, 10.04) * mm});
            skLineSegment(sketch, "E5.0.7.28", {"start": v(17.97, 13.85) * mm, "end": v(20.74, 13.85) * mm});
            skLineSegment(sketch, "E5.0.7.29", {"start": v(-23.94, 12.82) * mm, "end": v(-21.17, 12.82) * mm});
            skLineSegment(sketch, "E5.0.7.30", {"start": v(-12.51, 13.85) * mm, "end": v(-9.74, 13.85) * mm});
            skLineSegment(sketch, "E5.0.7.31", {"start": v(6.54, 12.82) * mm, "end": v(9.31, 12.82) * mm});
            skLineSegment(sketch, "E5.0.7.32", {"start": v(-21.17, 12.82) * mm, "end": v(-21.17, 10.04) * mm});
            skLineSegment(sketch, "E5.0.7.33", {"start": v(-12.51, 16.63) * mm, "end": v(-9.74, 16.63) * mm});
            skLineSegment(sketch, "E5.0.7.34", {"start": v(9.31, 12.82) * mm, "end": v(9.31, 10.04) * mm});
            skLineSegment(sketch, "E5.0.7.35", {"start": v(6.54, 12.82) * mm, "end": v(6.54, 10.04) * mm});
            skLineSegment(sketch, "E5.0.7.36", {"start": v(20.74, 16.63) * mm, "end": v(20.74, 13.85) * mm});
            skLineSegment(sketch, "E5.0.7.37", {"start": v(-23.94, 10.04) * mm, "end": v(-21.17, 10.04) * mm});
            skLineSegment(sketch, "E5.0.7.38", {"start": v(-12.51, 16.63) * mm, "end": v(-12.51, 13.85) * mm});
            skLineSegment(sketch, "E5.0.7.39", {"start": v(25.59, 13.85) * mm, "end": v(28.36, 13.85) * mm});
            skLineSegment(sketch, "E5.0.7.41", {"start": v(-4.9, 13.85) * mm, "end": v(-2.12, 13.85) * mm});
            skLineSegment(sketch, "E5.0.7.42", {"start": v(16.93, 12.82) * mm, "end": v(16.93, 10.04) * mm});
            skLineSegment(sketch, "E5.0.7.43", {"start": v(25.59, 16.63) * mm, "end": v(28.36, 16.63) * mm});
            skLineSegment(sketch, "E5.0.7.44", {"start": v(-13.55, 12.82) * mm, "end": v(-13.55, 10.04) * mm});
            skLineSegment(sketch, "E5.0.7.45", {"start": v(-4.9, 16.63) * mm, "end": v(-2.12, 16.63) * mm});
            skLineSegment(sketch, "E5.0.7.46", {"start": v(14.16, 10.04) * mm, "end": v(16.93, 10.04) * mm});
            skLineSegment(sketch, "E5.0.7.47", {"start": v(25.59, 16.63) * mm, "end": v(25.59, 13.85) * mm});
            skLineSegment(sketch, "E5.0.7.49", {"start": v(-16.32, 10.04) * mm, "end": v(-13.55, 10.04) * mm});
            skLineSegment(sketch, "E5.0.7.50", {"start": v(-4.9, 16.63) * mm, "end": v(-4.9, 13.85) * mm});
            skLineSegment(sketch, "E5.0.7.51", {"start": v(14.16, 12.82) * mm, "end": v(14.16, 10.04) * mm});
            skLineSegment(sketch, "E5.0.7.52", {"start": v(28.36, 16.63) * mm, "end": v(28.36, 13.85) * mm});
            skLineSegment(sketch, "E5.0.7.54", {"start": v(-16.32, 12.82) * mm, "end": v(-16.32, 10.04) * mm});
            skLineSegment(sketch, "E5.0.7.55", {"start": v(-2.12, 16.63) * mm, "end": v(-2.12, 13.85) * mm});
            skLineSegment(sketch, "E5.0.7.56", {"start": v(2.73, 13.85) * mm, "end": v(5.5, 13.85) * mm});
            skLineSegment(sketch, "E5.0.7.57", {"start": v(21.78, 12.82) * mm, "end": v(24.55, 12.82) * mm});
            skLineSegment(sketch, "E5.0.7.59", {"start": v(-27.75, 13.85) * mm, "end": v(-24.98, 13.85) * mm});
            skLineSegment(sketch, "E5.0.7.60", {"start": v(-8.7, 12.82) * mm, "end": v(-5.93, 12.82) * mm});
            skLineSegment(sketch, "E5.0.7.61", {"start": v(24.55, 12.82) * mm, "end": v(24.55, 10.04) * mm});
            skLineSegment(sketch, "E5.0.7.63", {"start": v(-5.93, 12.82) * mm, "end": v(-5.93, 10.04) * mm});
            skLineSegment(sketch, "E5.0.7.64", {"start": v(2.73, 16.63) * mm, "end": v(5.5, 16.63) * mm});
            skLineSegment(sketch, "E5.0.7.65", {"start": v(-27.75, 16.63) * mm, "end": v(-24.98, 16.63) * mm});
            skLineSegment(sketch, "E5.0.7.66", {"start": v(21.78, 10.04) * mm, "end": v(24.55, 10.04) * mm});
            skLineSegment(sketch, "E5.0.7.68", {"start": v(-8.7, 10.04) * mm, "end": v(-5.93, 10.04) * mm});
            skLineSegment(sketch, "E5.0.7.69", {"start": v(2.73, 16.63) * mm, "end": v(2.73, 13.85) * mm});
            skLineSegment(sketch, "E5.0.7.70", {"start": v(-27.75, 16.63) * mm, "end": v(-27.75, 13.85) * mm});
            skLineSegment(sketch, "E5.0.7.71", {"start": v(21.78, 12.82) * mm, "end": v(21.78, 10.04) * mm});
            skLineSegment(sketch, "E5.0.7.73", {"start": v(-8.7, 12.82) * mm, "end": v(-8.7, 10.04) * mm});
            skLineSegment(sketch, "E5.0.7.74", {"start": v(5.5, 16.63) * mm, "end": v(5.5, 13.85) * mm});
            skLineSegment(sketch, "E5.0.7.75", {"start": v(-24.98, 16.63) * mm, "end": v(-24.98, 13.85) * mm});
            skLineSegment(sketch, "E5.0.7.76", {"start": v(29.4, 12.82) * mm, "end": v(32.17, 12.82) * mm});
            skLineSegment(sketch, "E5.0.7.77", {"start": v(-20.13, 13.85) * mm, "end": v(-17.36, 13.85) * mm});
            skLineSegment(sketch, "E5.0.7.78", {"start": v(-1.08, 12.82) * mm, "end": v(1.7, 12.82) * mm});
            skLineSegment(sketch, "E5.0.7.79", {"start": v(10.35, 13.85) * mm, "end": v(13.12, 13.85) * mm});
            skLineSegment(sketch, "E5.0.7.80", {"start": v(29.4, 10.04) * mm, "end": v(32.17, 10.04) * mm});
            skLineSegment(sketch, "E5.0.7.81", {"start": v(-20.13, 16.63) * mm, "end": v(-20.13, 13.85) * mm});
            skLineSegment(sketch, "E5.0.7.82", {"start": v(-1.08, 10.04) * mm, "end": v(1.7, 10.04) * mm});
            skLineSegment(sketch, "E5.0.7.83", {"start": v(10.35, 16.63) * mm, "end": v(10.35, 13.85) * mm});
            skLineSegment(sketch, "E5.0.7.85", {"start": v(-17.36, 16.63) * mm, "end": v(-17.36, 13.85) * mm});
            skLineSegment(sketch, "E5.0.7.86", {"start": v(-1.08, 12.82) * mm, "end": v(-1.08, 10.04) * mm});
            skLineSegment(sketch, "E5.0.7.87", {"start": v(13.12, 16.63) * mm, "end": v(13.12, 13.85) * mm});
            skLineSegment(sketch, "E5.0.7.88", {"start": v(29.4, 12.82) * mm, "end": v(29.4, 10.04) * mm});
            skLineSegment(sketch, "E5.0.7.89", {"start": v(-31.56, 12.82) * mm, "end": v(-28.79, 12.82) * mm});
            skLineSegment(sketch, "E5.0.7.90", {"start": v(17.97, 16.63) * mm, "end": v(20.74, 16.63) * mm});
            skLineSegment(sketch, "E5.0.7.91", {"start": v(-23.94, 12.82) * mm, "end": v(-23.94, 10.04) * mm});
            skLineSegment(sketch, "E5.0.7.92", {"start": v(-9.74, 16.63) * mm, "end": v(-9.74, 13.85) * mm});
            skLineSegment(sketch, "E5.0.7.93", {"start": v(17.97, 16.63) * mm, "end": v(17.97, 13.85) * mm});
            skLineSegment(sketch, "E5.0.7.94", {"start": v(6.54, 10.04) * mm, "end": v(9.31, 10.04) * mm});
            skLineSegment(sketch, "E5.0.7.95", {"start": v(14.16, 12.82) * mm, "end": v(16.93, 12.82) * mm});
            skLineSegment(sketch, "E5.0.7.96", {"start": v(-16.32, 12.82) * mm, "end": v(-13.55, 12.82) * mm});
            skPoint(sketch, "E5.0.8.0", {"position": v(-11.13, 7.62) * mm});
            skPoint(sketch, "E5.0.8.1", {"position": v(19.35, 7.62) * mm});
            skPoint(sketch, "E5.0.8.2", {"position": v(23.16, 3.81) * mm});
            skPoint(sketch, "E5.0.8.3", {"position": v(11.73, 7.62) * mm});
            skPoint(sketch, "E5.0.8.4", {"position": v(-22.56, 3.81) * mm});
            skPoint(sketch, "E5.0.8.5", {"position": v(7.92, 3.81) * mm});
            skPoint(sketch, "E5.0.8.7", {"position": v(0.3, 3.81) * mm});
            skPoint(sketch, "E5.0.8.8", {"position": v(30.78, 3.81) * mm});
            skPoint(sketch, "E5.0.8.9", {"position": v(-30.18, 3.81) * mm});
            skPoint(sketch, "E5.0.8.10", {"position": v(-3.5, 7.62) * mm});
            skPoint(sketch, "E5.0.8.11", {"position": v(26.97, 7.62) * mm});
            skPoint(sketch, "E5.0.8.12", {"position": v(-7.32, 3.81) * mm});
            skPoint(sketch, "E5.0.8.13", {"position": v(-14.94, 3.81) * mm});
            skPoint(sketch, "E5.0.8.14", {"position": v(15.54, 3.81) * mm});
            skPoint(sketch, "E5.0.8.15", {"position": v(-18.75, 7.62) * mm});
            skPoint(sketch, "E5.0.8.17", {"position": v(-26.37, 7.62) * mm});
            skPoint(sketch, "E5.0.8.18", {"position": v(4.11, 7.62) * mm});
            skLineSegment(sketch, "E5.0.8.20", {"start": v(32.17, 5.2) * mm, "end": v(32.17, 2.42) * mm});
            skLineSegment(sketch, "E5.0.8.21", {"start": v(-20.13, 9) * mm, "end": v(-17.36, 9) * mm});
            skLineSegment(sketch, "E5.0.8.22", {"start": v(1.7, 5.2) * mm, "end": v(1.7, 2.42) * mm});
            skLineSegment(sketch, "E5.0.8.23", {"start": v(10.35, 9) * mm, "end": v(13.12, 9) * mm});
            skLineSegment(sketch, "E5.0.8.25", {"start": v(-28.79, 5.2) * mm, "end": v(-28.79, 2.42) * mm});
            skLineSegment(sketch, "E5.0.8.26", {"start": v(-31.56, 5.2) * mm, "end": v(-31.56, 2.42) * mm});
            skLineSegment(sketch, "E5.0.8.27", {"start": v(-31.56, 2.42) * mm, "end": v(-28.79, 2.42) * mm});
            skLineSegment(sketch, "E5.0.8.28", {"start": v(17.97, 6.23) * mm, "end": v(20.74, 6.23) * mm});
            skLineSegment(sketch, "E5.0.8.29", {"start": v(-23.94, 5.2) * mm, "end": v(-21.17, 5.2) * mm});
            skLineSegment(sketch, "E5.0.8.30", {"start": v(-12.51, 6.23) * mm, "end": v(-9.74, 6.23) * mm});
            skLineSegment(sketch, "E5.0.8.31", {"start": v(6.54, 5.2) * mm, "end": v(9.31, 5.2) * mm});
            skLineSegment(sketch, "E5.0.8.32", {"start": v(-21.17, 5.2) * mm, "end": v(-21.17, 2.42) * mm});
            skLineSegment(sketch, "E5.0.8.33", {"start": v(-12.51, 9) * mm, "end": v(-9.74, 9) * mm});
            skLineSegment(sketch, "E5.0.8.34", {"start": v(9.31, 5.2) * mm, "end": v(9.31, 2.42) * mm});
            skLineSegment(sketch, "E5.0.8.35", {"start": v(6.54, 5.2) * mm, "end": v(6.54, 2.42) * mm});
            skLineSegment(sketch, "E5.0.8.36", {"start": v(20.74, 9) * mm, "end": v(20.74, 6.23) * mm});
            skLineSegment(sketch, "E5.0.8.37", {"start": v(-23.94, 2.42) * mm, "end": v(-21.17, 2.42) * mm});
            skLineSegment(sketch, "E5.0.8.38", {"start": v(-12.51, 9) * mm, "end": v(-12.51, 6.23) * mm});
            skLineSegment(sketch, "E5.0.8.39", {"start": v(25.59, 6.23) * mm, "end": v(28.36, 6.23) * mm});
            skLineSegment(sketch, "E5.0.8.41", {"start": v(-4.9, 6.23) * mm, "end": v(-2.12, 6.23) * mm});
            skLineSegment(sketch, "E5.0.8.42", {"start": v(16.93, 5.2) * mm, "end": v(16.93, 2.42) * mm});
            skLineSegment(sketch, "E5.0.8.43", {"start": v(25.59, 9) * mm, "end": v(28.36, 9) * mm});
            skLineSegment(sketch, "E5.0.8.44", {"start": v(-13.55, 5.2) * mm, "end": v(-13.55, 2.42) * mm});
            skLineSegment(sketch, "E5.0.8.45", {"start": v(-4.9, 9) * mm, "end": v(-2.12, 9) * mm});
            skLineSegment(sketch, "E5.0.8.46", {"start": v(14.16, 2.42) * mm, "end": v(16.93, 2.42) * mm});
            skLineSegment(sketch, "E5.0.8.47", {"start": v(25.59, 9) * mm, "end": v(25.59, 6.23) * mm});
            skLineSegment(sketch, "E5.0.8.49", {"start": v(-16.32, 2.42) * mm, "end": v(-13.55, 2.42) * mm});
            skLineSegment(sketch, "E5.0.8.50", {"start": v(-4.9, 9) * mm, "end": v(-4.9, 6.23) * mm});
            skLineSegment(sketch, "E5.0.8.51", {"start": v(14.16, 5.2) * mm, "end": v(14.16, 2.42) * mm});
            skLineSegment(sketch, "E5.0.8.52", {"start": v(28.36, 9) * mm, "end": v(28.36, 6.23) * mm});
            skLineSegment(sketch, "E5.0.8.54", {"start": v(-16.32, 5.2) * mm, "end": v(-16.32, 2.42) * mm});
            skLineSegment(sketch, "E5.0.8.55", {"start": v(-2.12, 9) * mm, "end": v(-2.12, 6.23) * mm});
            skLineSegment(sketch, "E5.0.8.56", {"start": v(2.73, 6.23) * mm, "end": v(5.5, 6.23) * mm});
            skLineSegment(sketch, "E5.0.8.57", {"start": v(21.78, 5.2) * mm, "end": v(24.55, 5.2) * mm});
            skLineSegment(sketch, "E5.0.8.59", {"start": v(-27.75, 6.23) * mm, "end": v(-24.98, 6.23) * mm});
            skLineSegment(sketch, "E5.0.8.60", {"start": v(-8.7, 5.2) * mm, "end": v(-5.93, 5.2) * mm});
            skLineSegment(sketch, "E5.0.8.61", {"start": v(24.55, 5.2) * mm, "end": v(24.55, 2.42) * mm});
            skLineSegment(sketch, "E5.0.8.63", {"start": v(-5.93, 5.2) * mm, "end": v(-5.93, 2.42) * mm});
            skLineSegment(sketch, "E5.0.8.64", {"start": v(2.73, 9) * mm, "end": v(5.5, 9) * mm});
            skLineSegment(sketch, "E5.0.8.65", {"start": v(-27.75, 9) * mm, "end": v(-24.98, 9) * mm});
            skLineSegment(sketch, "E5.0.8.66", {"start": v(21.78, 2.42) * mm, "end": v(24.55, 2.42) * mm});
            skLineSegment(sketch, "E5.0.8.68", {"start": v(-8.7, 2.42) * mm, "end": v(-5.93, 2.42) * mm});
            skLineSegment(sketch, "E5.0.8.69", {"start": v(2.73, 9) * mm, "end": v(2.73, 6.23) * mm});
            skLineSegment(sketch, "E5.0.8.70", {"start": v(-27.75, 9) * mm, "end": v(-27.75, 6.23) * mm});
            skLineSegment(sketch, "E5.0.8.71", {"start": v(21.78, 5.2) * mm, "end": v(21.78, 2.42) * mm});
            skLineSegment(sketch, "E5.0.8.73", {"start": v(-8.7, 5.2) * mm, "end": v(-8.7, 2.42) * mm});
            skLineSegment(sketch, "E5.0.8.74", {"start": v(5.5, 9) * mm, "end": v(5.5, 6.23) * mm});
            skLineSegment(sketch, "E5.0.8.75", {"start": v(-24.98, 9) * mm, "end": v(-24.98, 6.23) * mm});
            skLineSegment(sketch, "E5.0.8.76", {"start": v(29.4, 5.2) * mm, "end": v(32.17, 5.2) * mm});
            skLineSegment(sketch, "E5.0.8.77", {"start": v(-20.13, 6.23) * mm, "end": v(-17.36, 6.23) * mm});
            skLineSegment(sketch, "E5.0.8.78", {"start": v(-1.08, 5.2) * mm, "end": v(1.7, 5.2) * mm});
            skLineSegment(sketch, "E5.0.8.79", {"start": v(10.35, 6.23) * mm, "end": v(13.12, 6.23) * mm});
            skLineSegment(sketch, "E5.0.8.80", {"start": v(29.4, 2.42) * mm, "end": v(32.17, 2.42) * mm});
            skLineSegment(sketch, "E5.0.8.81", {"start": v(-20.13, 9) * mm, "end": v(-20.13, 6.23) * mm});
            skLineSegment(sketch, "E5.0.8.82", {"start": v(-1.08, 2.42) * mm, "end": v(1.7, 2.42) * mm});
            skLineSegment(sketch, "E5.0.8.83", {"start": v(10.35, 9) * mm, "end": v(10.35, 6.23) * mm});
            skLineSegment(sketch, "E5.0.8.85", {"start": v(-17.36, 9) * mm, "end": v(-17.36, 6.23) * mm});
            skLineSegment(sketch, "E5.0.8.86", {"start": v(-1.08, 5.2) * mm, "end": v(-1.08, 2.42) * mm});
            skLineSegment(sketch, "E5.0.8.87", {"start": v(13.12, 9) * mm, "end": v(13.12, 6.23) * mm});
            skLineSegment(sketch, "E5.0.8.88", {"start": v(29.4, 5.2) * mm, "end": v(29.4, 2.42) * mm});
            skLineSegment(sketch, "E5.0.8.89", {"start": v(-31.56, 5.2) * mm, "end": v(-28.79, 5.2) * mm});
            skLineSegment(sketch, "E5.0.8.90", {"start": v(17.97, 9) * mm, "end": v(20.74, 9) * mm});
            skLineSegment(sketch, "E5.0.8.91", {"start": v(-23.94, 5.2) * mm, "end": v(-23.94, 2.42) * mm});
            skLineSegment(sketch, "E5.0.8.92", {"start": v(-9.74, 9) * mm, "end": v(-9.74, 6.23) * mm});
            skLineSegment(sketch, "E5.0.8.93", {"start": v(17.97, 9) * mm, "end": v(17.97, 6.23) * mm});
            skLineSegment(sketch, "E5.0.8.94", {"start": v(6.54, 2.42) * mm, "end": v(9.31, 2.42) * mm});
            skLineSegment(sketch, "E5.0.8.95", {"start": v(14.16, 5.2) * mm, "end": v(16.93, 5.2) * mm});
            skLineSegment(sketch, "E5.0.8.96", {"start": v(-16.32, 5.2) * mm, "end": v(-13.55, 5.2) * mm});
            skPoint(sketch, "E5.0.9.0", {"position": v(-11.13, 0) * mm});
            skPoint(sketch, "E5.0.9.1", {"position": v(19.35, 0) * mm});
            skPoint(sketch, "E5.0.9.2", {"position": v(23.16, -3.8) * mm});
            skPoint(sketch, "E5.0.9.3", {"position": v(11.73, 0) * mm});
            skPoint(sketch, "E5.0.9.4", {"position": v(-22.56, -3.8) * mm});
            skPoint(sketch, "E5.0.9.5", {"position": v(7.92, -3.8) * mm});
            skPoint(sketch, "E5.0.9.7", {"position": v(0.3, -3.8) * mm});
            skPoint(sketch, "E5.0.9.8", {"position": v(30.78, -3.8) * mm});
            skPoint(sketch, "E5.0.9.9", {"position": v(-30.18, -3.8) * mm});
            skPoint(sketch, "E5.0.9.10", {"position": v(-3.5, 0) * mm});
            skPoint(sketch, "E5.0.9.11", {"position": v(26.97, 0) * mm});
            skPoint(sketch, "E5.0.9.12", {"position": v(-7.32, -3.8) * mm});
            skPoint(sketch, "E5.0.9.13", {"position": v(-14.94, -3.8) * mm});
            skPoint(sketch, "E5.0.9.14", {"position": v(15.54, -3.8) * mm});
            skPoint(sketch, "E5.0.9.15", {"position": v(-18.75, 0) * mm});
            skPoint(sketch, "E5.0.9.17", {"position": v(-26.37, 0) * mm});
            skPoint(sketch, "E5.0.9.18", {"position": v(4.11, 0) * mm});
            skLineSegment(sketch, "E5.0.9.20", {"start": v(32.17, -2.42) * mm, "end": v(32.17, -5.2) * mm});
            skLineSegment(sketch, "E5.0.9.21", {"start": v(-20.13, 1.39) * mm, "end": v(-17.36, 1.39) * mm});
            skLineSegment(sketch, "E5.0.9.22", {"start": v(1.7, -2.42) * mm, "end": v(1.7, -5.2) * mm});
            skLineSegment(sketch, "E5.0.9.23", {"start": v(10.35, 1.39) * mm, "end": v(13.12, 1.39) * mm});
            skLineSegment(sketch, "E5.0.9.25", {"start": v(-28.79, -2.42) * mm, "end": v(-28.79, -5.2) * mm});
            skLineSegment(sketch, "E5.0.9.26", {"start": v(-31.56, -2.42) * mm, "end": v(-31.56, -5.2) * mm});
            skLineSegment(sketch, "E5.0.9.27", {"start": v(-31.56, -5.2) * mm, "end": v(-28.79, -5.2) * mm});
            skLineSegment(sketch, "E5.0.9.28", {"start": v(17.97, -1.39) * mm, "end": v(20.74, -1.39) * mm});
            skLineSegment(sketch, "E5.0.9.29", {"start": v(-23.94, -2.42) * mm, "end": v(-21.17, -2.42) * mm});
            skLineSegment(sketch, "E5.0.9.30", {"start": v(-12.51, -1.39) * mm, "end": v(-9.74, -1.39) * mm});
            skLineSegment(sketch, "E5.0.9.31", {"start": v(6.54, -2.42) * mm, "end": v(9.31, -2.42) * mm});
            skLineSegment(sketch, "E5.0.9.32", {"start": v(-21.17, -2.42) * mm, "end": v(-21.17, -5.2) * mm});
            skLineSegment(sketch, "E5.0.9.33", {"start": v(-12.51, 1.39) * mm, "end": v(-9.74, 1.39) * mm});
            skLineSegment(sketch, "E5.0.9.34", {"start": v(9.31, -2.42) * mm, "end": v(9.31, -5.2) * mm});
            skLineSegment(sketch, "E5.0.9.35", {"start": v(6.54, -2.42) * mm, "end": v(6.54, -5.2) * mm});
            skLineSegment(sketch, "E5.0.9.36", {"start": v(20.74, 1.39) * mm, "end": v(20.74, -1.39) * mm});
            skLineSegment(sketch, "E5.0.9.37", {"start": v(-23.94, -5.2) * mm, "end": v(-21.17, -5.2) * mm});
            skLineSegment(sketch, "E5.0.9.38", {"start": v(-12.51, 1.39) * mm, "end": v(-12.51, -1.39) * mm});
            skLineSegment(sketch, "E5.0.9.39", {"start": v(25.59, -1.39) * mm, "end": v(28.36, -1.39) * mm});
            skLineSegment(sketch, "E5.0.9.41", {"start": v(-4.9, -1.39) * mm, "end": v(-2.12, -1.39) * mm});
            skLineSegment(sketch, "E5.0.9.42", {"start": v(16.93, -2.42) * mm, "end": v(16.93, -5.2) * mm});
            skLineSegment(sketch, "E5.0.9.43", {"start": v(25.59, 1.39) * mm, "end": v(28.36, 1.39) * mm});
            skLineSegment(sketch, "E5.0.9.44", {"start": v(-13.55, -2.42) * mm, "end": v(-13.55, -5.2) * mm});
            skLineSegment(sketch, "E5.0.9.45", {"start": v(-4.9, 1.39) * mm, "end": v(-2.12, 1.39) * mm});
            skLineSegment(sketch, "E5.0.9.46", {"start": v(14.16, -5.2) * mm, "end": v(16.93, -5.2) * mm});
            skLineSegment(sketch, "E5.0.9.47", {"start": v(25.59, 1.39) * mm, "end": v(25.59, -1.39) * mm});
            skLineSegment(sketch, "E5.0.9.49", {"start": v(-16.32, -5.2) * mm, "end": v(-13.55, -5.2) * mm});
            skLineSegment(sketch, "E5.0.9.50", {"start": v(-4.9, 1.39) * mm, "end": v(-4.9, -1.39) * mm});
            skLineSegment(sketch, "E5.0.9.51", {"start": v(14.16, -2.42) * mm, "end": v(14.16, -5.2) * mm});
            skLineSegment(sketch, "E5.0.9.52", {"start": v(28.36, 1.39) * mm, "end": v(28.36, -1.39) * mm});
            skLineSegment(sketch, "E5.0.9.54", {"start": v(-16.32, -2.42) * mm, "end": v(-16.32, -5.2) * mm});
            skLineSegment(sketch, "E5.0.9.55", {"start": v(-2.12, 1.39) * mm, "end": v(-2.12, -1.39) * mm});
            skLineSegment(sketch, "E5.0.9.56", {"start": v(2.73, -1.39) * mm, "end": v(5.5, -1.39) * mm});
            skLineSegment(sketch, "E5.0.9.57", {"start": v(21.78, -2.42) * mm, "end": v(24.55, -2.42) * mm});
            skLineSegment(sketch, "E5.0.9.59", {"start": v(-27.75, -1.39) * mm, "end": v(-24.98, -1.39) * mm});
            skLineSegment(sketch, "E5.0.9.60", {"start": v(-8.7, -2.42) * mm, "end": v(-5.93, -2.42) * mm});
            skLineSegment(sketch, "E5.0.9.61", {"start": v(24.55, -2.42) * mm, "end": v(24.55, -5.2) * mm});
            skLineSegment(sketch, "E5.0.9.63", {"start": v(-5.93, -2.42) * mm, "end": v(-5.93, -5.2) * mm});
            skLineSegment(sketch, "E5.0.9.64", {"start": v(2.73, 1.39) * mm, "end": v(5.5, 1.39) * mm});
            skLineSegment(sketch, "E5.0.9.65", {"start": v(-27.75, 1.39) * mm, "end": v(-24.98, 1.39) * mm});
            skLineSegment(sketch, "E5.0.9.66", {"start": v(21.78, -5.2) * mm, "end": v(24.55, -5.2) * mm});
            skLineSegment(sketch, "E5.0.9.68", {"start": v(-8.7, -5.2) * mm, "end": v(-5.93, -5.2) * mm});
            skLineSegment(sketch, "E5.0.9.69", {"start": v(2.73, 1.39) * mm, "end": v(2.73, -1.39) * mm});
            skLineSegment(sketch, "E5.0.9.70", {"start": v(-27.75, 1.39) * mm, "end": v(-27.75, -1.39) * mm});
            skLineSegment(sketch, "E5.0.9.71", {"start": v(21.78, -2.42) * mm, "end": v(21.78, -5.2) * mm});
            skLineSegment(sketch, "E5.0.9.73", {"start": v(-8.7, -2.42) * mm, "end": v(-8.7, -5.2) * mm});
            skLineSegment(sketch, "E5.0.9.74", {"start": v(5.5, 1.39) * mm, "end": v(5.5, -1.39) * mm});
            skLineSegment(sketch, "E5.0.9.75", {"start": v(-24.98, 1.39) * mm, "end": v(-24.98, -1.39) * mm});
            skLineSegment(sketch, "E5.0.9.76", {"start": v(29.4, -2.42) * mm, "end": v(32.17, -2.42) * mm});
            skLineSegment(sketch, "E5.0.9.77", {"start": v(-20.13, -1.39) * mm, "end": v(-17.36, -1.39) * mm});
            skLineSegment(sketch, "E5.0.9.78", {"start": v(-1.08, -2.42) * mm, "end": v(1.7, -2.42) * mm});
            skLineSegment(sketch, "E5.0.9.79", {"start": v(10.35, -1.39) * mm, "end": v(13.12, -1.39) * mm});
            skLineSegment(sketch, "E5.0.9.80", {"start": v(29.4, -5.2) * mm, "end": v(32.17, -5.2) * mm});
            skLineSegment(sketch, "E5.0.9.81", {"start": v(-20.13, 1.39) * mm, "end": v(-20.13, -1.39) * mm});
            skLineSegment(sketch, "E5.0.9.82", {"start": v(-1.08, -5.2) * mm, "end": v(1.7, -5.2) * mm});
            skLineSegment(sketch, "E5.0.9.83", {"start": v(10.35, 1.39) * mm, "end": v(10.35, -1.39) * mm});
            skLineSegment(sketch, "E5.0.9.85", {"start": v(-17.36, 1.39) * mm, "end": v(-17.36, -1.39) * mm});
            skLineSegment(sketch, "E5.0.9.86", {"start": v(-1.08, -2.42) * mm, "end": v(-1.08, -5.2) * mm});
            skLineSegment(sketch, "E5.0.9.87", {"start": v(13.12, 1.39) * mm, "end": v(13.12, -1.39) * mm});
            skLineSegment(sketch, "E5.0.9.88", {"start": v(29.4, -2.42) * mm, "end": v(29.4, -5.2) * mm});
            skLineSegment(sketch, "E5.0.9.89", {"start": v(-31.56, -2.42) * mm, "end": v(-28.79, -2.42) * mm});
            skLineSegment(sketch, "E5.0.9.90", {"start": v(17.97, 1.39) * mm, "end": v(20.74, 1.39) * mm});
            skLineSegment(sketch, "E5.0.9.91", {"start": v(-23.94, -2.42) * mm, "end": v(-23.94, -5.2) * mm});
            skLineSegment(sketch, "E5.0.9.92", {"start": v(-9.74, 1.39) * mm, "end": v(-9.74, -1.39) * mm});
            skLineSegment(sketch, "E5.0.9.93", {"start": v(17.97, 1.39) * mm, "end": v(17.97, -1.39) * mm});
            skLineSegment(sketch, "E5.0.9.94", {"start": v(6.54, -5.2) * mm, "end": v(9.31, -5.2) * mm});
            skLineSegment(sketch, "E5.0.9.95", {"start": v(14.16, -2.42) * mm, "end": v(16.93, -2.42) * mm});
            skLineSegment(sketch, "E5.0.9.96", {"start": v(-16.32, -2.42) * mm, "end": v(-13.55, -2.42) * mm});
            skPoint(sketch, "E6.0.1.0", {"position": v(19.35, -7.62) * mm});
            skPoint(sketch, "E6.0.1.1", {"position": v(-18.75, -7.62) * mm});
            skPoint(sketch, "E6.0.1.2", {"position": v(30.78, -11.43) * mm});
            skPoint(sketch, "E6.0.1.3", {"position": v(11.73, -7.62) * mm});
            skPoint(sketch, "E6.0.1.4", {"position": v(-7.32, -11.43) * mm});
            skPoint(sketch, "E6.0.1.5", {"position": v(-14.94, -11.43) * mm});
            skPoint(sketch, "E6.0.1.6", {"position": v(-22.56, -11.43) * mm});
            skPoint(sketch, "E6.0.1.7", {"position": v(-3.5, -7.62) * mm});
            skPoint(sketch, "E6.0.1.10", {"position": v(-26.37, -7.62) * mm});
            skPoint(sketch, "E6.0.1.11", {"position": v(-11.13, -7.62) * mm});
            skPoint(sketch, "E6.0.1.12", {"position": v(0.3, -11.43) * mm});
            skPoint(sketch, "E6.0.1.13", {"position": v(15.54, -11.43) * mm});
            skPoint(sketch, "E6.0.1.14", {"position": v(7.92, -11.43) * mm});
            skPoint(sketch, "E6.0.1.15", {"position": v(26.97, -7.62) * mm});
            skPoint(sketch, "E6.0.1.16", {"position": v(4.11, -7.62) * mm});
            skPoint(sketch, "E6.0.1.17", {"position": v(-30.18, -11.43) * mm});
            skPoint(sketch, "E6.0.1.19", {"position": v(23.16, -11.43) * mm});
            skPoint(sketch, "E6.0.1.21", {"position": v(0, -7.62) * mm});
            skLineSegment(sketch, "E6.0.1.22", {"start": v(-4.9, -6.23) * mm, "end": v(-4.9, -9) * mm});
            skLineSegment(sketch, "E6.0.1.23", {"start": v(-1.08, -12.82) * mm, "end": v(1.7, -12.82) * mm});
            skLineSegment(sketch, "E6.0.1.24", {"start": v(21.78, -12.82) * mm, "end": v(24.55, -12.82) * mm});
            skLineSegment(sketch, "E6.0.1.25", {"start": v(9.31, -10.04) * mm, "end": v(9.31, -12.82) * mm});
            skLineSegment(sketch, "E6.0.1.27", {"start": v(-17.36, -6.23) * mm, "end": v(-17.36, -9) * mm});
            skLineSegment(sketch, "E6.0.1.28", {"start": v(-16.32, -12.82) * mm, "end": v(-13.55, -12.82) * mm});
            skLineSegment(sketch, "E6.0.1.29", {"start": v(-20.13, -6.23) * mm, "end": v(-20.13, -9) * mm});
            skLineSegment(sketch, "E6.0.1.30", {"start": v(-23.94, -12.82) * mm, "end": v(-21.17, -12.82) * mm});
            skLineSegment(sketch, "E6.0.1.31", {"start": v(-20.13, -6.23) * mm, "end": v(-17.36, -6.23) * mm});
            skLineSegment(sketch, "E6.0.1.32", {"start": v(-21.17, -10.04) * mm, "end": v(-21.17, -12.82) * mm});
            skLineSegment(sketch, "E6.0.1.35", {"start": v(29.4, -12.82) * mm, "end": v(32.17, -12.82) * mm});
            skLineSegment(sketch, "E6.0.1.36", {"start": v(6.54, -10.04) * mm, "end": v(9.31, -10.04) * mm});
            skLineSegment(sketch, "E6.0.1.37", {"start": v(-12.51, -9) * mm, "end": v(-9.74, -9) * mm});
            skLineSegment(sketch, "E6.0.1.38", {"start": v(14.16, -10.04) * mm, "end": v(16.93, -10.04) * mm});
            skLineSegment(sketch, "E6.0.1.39", {"start": v(-5.93, -10.04) * mm, "end": v(-5.93, -12.82) * mm});
            skLineSegment(sketch, "E6.0.1.40", {"start": v(-23.94, -10.04) * mm, "end": v(-21.17, -10.04) * mm});
            skLineSegment(sketch, "E6.0.1.41", {"start": v(6.54, -12.82) * mm, "end": v(9.31, -12.82) * mm});
            skLineSegment(sketch, "E6.0.1.42", {"start": v(14.16, -12.82) * mm, "end": v(16.93, -12.82) * mm});
            skLineSegment(sketch, "E6.0.1.43", {"start": v(17.97, -6.23) * mm, "end": v(17.97, -9) * mm});
            skLineSegment(sketch, "E6.0.1.44", {"start": v(32.17, -10.04) * mm, "end": v(32.17, -12.82) * mm});
            skLineSegment(sketch, "E6.0.1.45", {"start": v(20.74, -6.23) * mm, "end": v(20.74, -9) * mm});
            skLineSegment(sketch, "E6.0.1.46", {"start": v(17.97, -9) * mm, "end": v(20.74, -9) * mm});
            skLineSegment(sketch, "E6.0.1.47", {"start": v(-8.7, -12.82) * mm, "end": v(-5.93, -12.82) * mm});
            skLineSegment(sketch, "E6.0.1.48", {"start": v(24.55, -10.04) * mm, "end": v(24.55, -12.82) * mm});
            skLineSegment(sketch, "E6.0.1.49", {"start": v(-20.13, -9) * mm, "end": v(-17.36, -9) * mm});
            skLineSegment(sketch, "E6.0.1.51", {"start": v(28.36, -6.23) * mm, "end": v(28.36, -9) * mm});
            skLineSegment(sketch, "E6.0.1.52", {"start": v(-9.74, -6.23) * mm, "end": v(-9.74, -9) * mm});
            skLineSegment(sketch, "E6.0.1.53", {"start": v(-13.55, -10.04) * mm, "end": v(-13.55, -12.82) * mm});
            skLineSegment(sketch, "E6.0.1.54", {"start": v(-8.7, -10.04) * mm, "end": v(-5.93, -10.04) * mm});
            skLineSegment(sketch, "E6.0.1.55", {"start": v(-31.56, -12.82) * mm, "end": v(-28.79, -12.82) * mm});
            skLineSegment(sketch, "E6.0.1.56", {"start": v(-23.94, -10.04) * mm, "end": v(-23.94, -12.82) * mm});
            skLineSegment(sketch, "E6.0.1.57", {"start": v(-31.56, -10.04) * mm, "end": v(-31.56, -12.82) * mm});
            skLineSegment(sketch, "E6.0.1.58", {"start": v(16.93, -10.04) * mm, "end": v(16.93, -12.82) * mm});
            skLineSegment(sketch, "E6.0.1.59", {"start": v(5.5, -6.23) * mm, "end": v(5.5, -9) * mm});
            skLineSegment(sketch, "E6.0.1.60", {"start": v(-4.9, -9) * mm, "end": v(-2.12, -9) * mm});
            skLineSegment(sketch, "E6.0.1.61", {"start": v(-28.79, -10.04) * mm, "end": v(-28.79, -12.82) * mm});
            skLineSegment(sketch, "E6.0.1.62", {"start": v(2.73, -9) * mm, "end": v(5.5, -9) * mm});
            skLineSegment(sketch, "E6.0.1.64", {"start": v(29.4, -10.04) * mm, "end": v(29.4, -12.82) * mm});
            skLineSegment(sketch, "E6.0.1.65", {"start": v(21.78, -10.04) * mm, "end": v(24.55, -10.04) * mm});
            skLineSegment(sketch, "E6.0.1.66", {"start": v(6.54, -10.04) * mm, "end": v(6.54, -12.82) * mm});
            skLineSegment(sketch, "E6.0.1.67", {"start": v(-31.56, -10.04) * mm, "end": v(-28.79, -10.04) * mm});
            skLineSegment(sketch, "E6.0.1.68", {"start": v(21.78, -10.04) * mm, "end": v(21.78, -12.82) * mm});
            skLineSegment(sketch, "E6.0.1.70", {"start": v(13.12, -6.23) * mm, "end": v(13.12, -9) * mm});
            skLineSegment(sketch, "E6.0.1.71", {"start": v(10.35, -6.23) * mm, "end": v(13.12, -6.23) * mm});
            skLineSegment(sketch, "E6.0.1.72", {"start": v(-8.7, -10.04) * mm, "end": v(-8.7, -12.82) * mm});
            skLineSegment(sketch, "E6.0.1.73", {"start": v(14.16, -10.04) * mm, "end": v(14.16, -12.82) * mm});
            skLineSegment(sketch, "E6.0.1.75", {"start": v(-16.32, -10.04) * mm, "end": v(-16.32, -12.82) * mm});
            skLineSegment(sketch, "E6.0.1.77", {"start": v(-1.08, -10.04) * mm, "end": v(-1.08, -12.82) * mm});
            skLineSegment(sketch, "E6.0.1.78", {"start": v(-12.51, -6.23) * mm, "end": v(-12.51, -9) * mm});
            skLineSegment(sketch, "E6.0.1.79", {"start": v(1.7, -10.04) * mm, "end": v(1.7, -12.82) * mm});
            skLineSegment(sketch, "E6.0.1.80", {"start": v(-12.51, -6.23) * mm, "end": v(-9.74, -6.23) * mm});
            skLineSegment(sketch, "E6.0.1.82", {"start": v(2.73, -6.23) * mm, "end": v(2.73, -9) * mm});
            skLineSegment(sketch, "E6.0.1.83", {"start": v(10.35, -6.23) * mm, "end": v(10.35, -9) * mm});
            skLineSegment(sketch, "E6.0.1.85", {"start": v(-16.32, -10.04) * mm, "end": v(-13.55, -10.04) * mm});
            skLineSegment(sketch, "E6.0.1.86", {"start": v(2.73, -6.23) * mm, "end": v(5.5, -6.23) * mm});
            skLineSegment(sketch, "E6.0.1.87", {"start": v(25.59, -6.23) * mm, "end": v(25.59, -9) * mm});
            skLineSegment(sketch, "E6.0.1.88", {"start": v(10.35, -9) * mm, "end": v(13.12, -9) * mm});
            skLineSegment(sketch, "E6.0.1.90", {"start": v(-1.08, -10.04) * mm, "end": v(1.7, -10.04) * mm});
            skLineSegment(sketch, "E6.0.1.92", {"start": v(29.4, -10.04) * mm, "end": v(32.17, -10.04) * mm});
            skLineSegment(sketch, "E6.0.1.93", {"start": v(25.59, -6.23) * mm, "end": v(28.36, -6.23) * mm});
            skLineSegment(sketch, "E6.0.1.94", {"start": v(-27.75, -9) * mm, "end": v(-24.98, -9) * mm});
            skLineSegment(sketch, "E6.0.1.95", {"start": v(-24.98, -6.23) * mm, "end": v(-24.98, -9) * mm});
            skLineSegment(sketch, "E6.0.1.96", {"start": v(17.97, -6.23) * mm, "end": v(20.74, -6.23) * mm});
            skLineSegment(sketch, "E6.0.1.99", {"start": v(25.59, -9) * mm, "end": v(28.36, -9) * mm});
            skLineSegment(sketch, "E6.0.1.101", {"start": v(-27.75, -6.23) * mm, "end": v(-27.75, -9) * mm});
            skLineSegment(sketch, "E6.0.1.104", {"start": v(-27.75, -6.23) * mm, "end": v(-24.98, -6.23) * mm});
            skLineSegment(sketch, "E6.0.1.105", {"start": v(-4.9, -6.23) * mm, "end": v(-2.12, -6.23) * mm});
            skLineSegment(sketch, "E6.0.1.106", {"start": v(-2.12, -6.23) * mm, "end": v(-2.12, -9) * mm});
            skPoint(sketch, "E6.0.2.0", {"position": v(19.35, -15.24) * mm});
            skPoint(sketch, "E6.0.2.1", {"position": v(-18.75, -15.24) * mm});
            skPoint(sketch, "E6.0.2.2", {"position": v(30.78, -19.05) * mm});
            skPoint(sketch, "E6.0.2.3", {"position": v(11.73, -15.24) * mm});
            skPoint(sketch, "E6.0.2.4", {"position": v(-7.32, -19.05) * mm});
            skPoint(sketch, "E6.0.2.5", {"position": v(-14.94, -19.05) * mm});
            skPoint(sketch, "E6.0.2.6", {"position": v(-22.56, -19.05) * mm});
            skPoint(sketch, "E6.0.2.7", {"position": v(-3.5, -15.24) * mm});
            skPoint(sketch, "E6.0.2.10", {"position": v(-26.37, -15.24) * mm});
            skPoint(sketch, "E6.0.2.11", {"position": v(-11.13, -15.24) * mm});
            skPoint(sketch, "E6.0.2.12", {"position": v(0.3, -19.05) * mm});
            skPoint(sketch, "E6.0.2.13", {"position": v(15.54, -19.05) * mm});
            skPoint(sketch, "E6.0.2.14", {"position": v(7.92, -19.05) * mm});
            skPoint(sketch, "E6.0.2.15", {"position": v(26.97, -15.24) * mm});
            skPoint(sketch, "E6.0.2.16", {"position": v(4.11, -15.24) * mm});
            skPoint(sketch, "E6.0.2.17", {"position": v(-30.18, -19.05) * mm});
            skPoint(sketch, "E6.0.2.19", {"position": v(23.16, -19.05) * mm});
            skPoint(sketch, "E6.0.2.21", {"position": v(0, -15.24) * mm});
            skLineSegment(sketch, "E6.0.2.22", {"start": v(-4.9, -13.85) * mm, "end": v(-4.9, -16.63) * mm});
            skLineSegment(sketch, "E6.0.2.23", {"start": v(-1.08, -20.44) * mm, "end": v(1.7, -20.44) * mm});
            skLineSegment(sketch, "E6.0.2.24", {"start": v(21.78, -20.44) * mm, "end": v(24.55, -20.44) * mm});
            skLineSegment(sketch, "E6.0.2.25", {"start": v(9.31, -17.66) * mm, "end": v(9.31, -20.44) * mm});
            skLineSegment(sketch, "E6.0.2.27", {"start": v(-17.36, -13.85) * mm, "end": v(-17.36, -16.63) * mm});
            skLineSegment(sketch, "E6.0.2.28", {"start": v(-16.32, -20.44) * mm, "end": v(-13.55, -20.44) * mm});
            skLineSegment(sketch, "E6.0.2.29", {"start": v(-20.13, -13.85) * mm, "end": v(-20.13, -16.63) * mm});
            skLineSegment(sketch, "E6.0.2.30", {"start": v(-23.94, -20.44) * mm, "end": v(-21.17, -20.44) * mm});
            skLineSegment(sketch, "E6.0.2.31", {"start": v(-20.13, -13.85) * mm, "end": v(-17.36, -13.85) * mm});
            skLineSegment(sketch, "E6.0.2.32", {"start": v(-21.17, -17.66) * mm, "end": v(-21.17, -20.44) * mm});
            skLineSegment(sketch, "E6.0.2.35", {"start": v(29.4, -20.44) * mm, "end": v(32.17, -20.44) * mm});
            skLineSegment(sketch, "E6.0.2.36", {"start": v(6.54, -17.66) * mm, "end": v(9.31, -17.66) * mm});
            skLineSegment(sketch, "E6.0.2.37", {"start": v(-12.51, -16.63) * mm, "end": v(-9.74, -16.63) * mm});
            skLineSegment(sketch, "E6.0.2.38", {"start": v(14.16, -17.66) * mm, "end": v(16.93, -17.66) * mm});
            skLineSegment(sketch, "E6.0.2.39", {"start": v(-5.93, -17.66) * mm, "end": v(-5.93, -20.44) * mm});
            skLineSegment(sketch, "E6.0.2.40", {"start": v(-23.94, -17.66) * mm, "end": v(-21.17, -17.66) * mm});
            skLineSegment(sketch, "E6.0.2.41", {"start": v(6.54, -20.44) * mm, "end": v(9.31, -20.44) * mm});
            skLineSegment(sketch, "E6.0.2.42", {"start": v(14.16, -20.44) * mm, "end": v(16.93, -20.44) * mm});
            skLineSegment(sketch, "E6.0.2.43", {"start": v(17.97, -13.85) * mm, "end": v(17.97, -16.63) * mm});
            skLineSegment(sketch, "E6.0.2.44", {"start": v(32.17, -17.66) * mm, "end": v(32.17, -20.44) * mm});
            skLineSegment(sketch, "E6.0.2.45", {"start": v(20.74, -13.85) * mm, "end": v(20.74, -16.63) * mm});
            skLineSegment(sketch, "E6.0.2.46", {"start": v(17.97, -16.63) * mm, "end": v(20.74, -16.63) * mm});
            skLineSegment(sketch, "E6.0.2.47", {"start": v(-8.7, -20.44) * mm, "end": v(-5.93, -20.44) * mm});
            skLineSegment(sketch, "E6.0.2.48", {"start": v(24.55, -17.66) * mm, "end": v(24.55, -20.44) * mm});
            skLineSegment(sketch, "E6.0.2.49", {"start": v(-20.13, -16.63) * mm, "end": v(-17.36, -16.63) * mm});
            skLineSegment(sketch, "E6.0.2.51", {"start": v(28.36, -13.85) * mm, "end": v(28.36, -16.63) * mm});
            skLineSegment(sketch, "E6.0.2.52", {"start": v(-9.74, -13.85) * mm, "end": v(-9.74, -16.63) * mm});
            skLineSegment(sketch, "E6.0.2.53", {"start": v(-13.55, -17.66) * mm, "end": v(-13.55, -20.44) * mm});
            skLineSegment(sketch, "E6.0.2.54", {"start": v(-8.7, -17.66) * mm, "end": v(-5.93, -17.66) * mm});
            skLineSegment(sketch, "E6.0.2.55", {"start": v(-31.56, -20.44) * mm, "end": v(-28.79, -20.44) * mm});
            skLineSegment(sketch, "E6.0.2.56", {"start": v(-23.94, -17.66) * mm, "end": v(-23.94, -20.44) * mm});
            skLineSegment(sketch, "E6.0.2.57", {"start": v(-31.56, -17.66) * mm, "end": v(-31.56, -20.44) * mm});
            skLineSegment(sketch, "E6.0.2.58", {"start": v(16.93, -17.66) * mm, "end": v(16.93, -20.44) * mm});
            skLineSegment(sketch, "E6.0.2.59", {"start": v(5.5, -13.85) * mm, "end": v(5.5, -16.63) * mm});
            skLineSegment(sketch, "E6.0.2.60", {"start": v(-4.9, -16.63) * mm, "end": v(-2.12, -16.63) * mm});
            skLineSegment(sketch, "E6.0.2.61", {"start": v(-28.79, -17.66) * mm, "end": v(-28.79, -20.44) * mm});
            skLineSegment(sketch, "E6.0.2.62", {"start": v(2.73, -16.63) * mm, "end": v(5.5, -16.63) * mm});
            skLineSegment(sketch, "E6.0.2.64", {"start": v(29.4, -17.66) * mm, "end": v(29.4, -20.44) * mm});
            skLineSegment(sketch, "E6.0.2.65", {"start": v(21.78, -17.66) * mm, "end": v(24.55, -17.66) * mm});
            skLineSegment(sketch, "E6.0.2.66", {"start": v(6.54, -17.66) * mm, "end": v(6.54, -20.44) * mm});
            skLineSegment(sketch, "E6.0.2.67", {"start": v(-31.56, -17.66) * mm, "end": v(-28.79, -17.66) * mm});
            skLineSegment(sketch, "E6.0.2.68", {"start": v(21.78, -17.66) * mm, "end": v(21.78, -20.44) * mm});
            skLineSegment(sketch, "E6.0.2.70", {"start": v(13.12, -13.85) * mm, "end": v(13.12, -16.63) * mm});
            skLineSegment(sketch, "E6.0.2.71", {"start": v(10.35, -13.85) * mm, "end": v(13.12, -13.85) * mm});
            skLineSegment(sketch, "E6.0.2.72", {"start": v(-8.7, -17.66) * mm, "end": v(-8.7, -20.44) * mm});
            skLineSegment(sketch, "E6.0.2.73", {"start": v(14.16, -17.66) * mm, "end": v(14.16, -20.44) * mm});
            skLineSegment(sketch, "E6.0.2.75", {"start": v(-16.32, -17.66) * mm, "end": v(-16.32, -20.44) * mm});
            skLineSegment(sketch, "E6.0.2.77", {"start": v(-1.08, -17.66) * mm, "end": v(-1.08, -20.44) * mm});
            skLineSegment(sketch, "E6.0.2.78", {"start": v(-12.51, -13.85) * mm, "end": v(-12.51, -16.63) * mm});
            skLineSegment(sketch, "E6.0.2.79", {"start": v(1.7, -17.66) * mm, "end": v(1.7, -20.44) * mm});
            skLineSegment(sketch, "E6.0.2.80", {"start": v(-12.51, -13.85) * mm, "end": v(-9.74, -13.85) * mm});
            skLineSegment(sketch, "E6.0.2.82", {"start": v(2.73, -13.85) * mm, "end": v(2.73, -16.63) * mm});
            skLineSegment(sketch, "E6.0.2.83", {"start": v(10.35, -13.85) * mm, "end": v(10.35, -16.63) * mm});
            skLineSegment(sketch, "E6.0.2.85", {"start": v(-16.32, -17.66) * mm, "end": v(-13.55, -17.66) * mm});
            skLineSegment(sketch, "E6.0.2.86", {"start": v(2.73, -13.85) * mm, "end": v(5.5, -13.85) * mm});
            skLineSegment(sketch, "E6.0.2.87", {"start": v(25.59, -13.85) * mm, "end": v(25.59, -16.63) * mm});
            skLineSegment(sketch, "E6.0.2.88", {"start": v(10.35, -16.63) * mm, "end": v(13.12, -16.63) * mm});
            skLineSegment(sketch, "E6.0.2.90", {"start": v(-1.08, -17.66) * mm, "end": v(1.7, -17.66) * mm});
            skLineSegment(sketch, "E6.0.2.92", {"start": v(29.4, -17.66) * mm, "end": v(32.17, -17.66) * mm});
            skLineSegment(sketch, "E6.0.2.93", {"start": v(25.59, -13.85) * mm, "end": v(28.36, -13.85) * mm});
            skLineSegment(sketch, "E6.0.2.94", {"start": v(-27.75, -16.63) * mm, "end": v(-24.98, -16.63) * mm});
            skLineSegment(sketch, "E6.0.2.95", {"start": v(-24.98, -13.85) * mm, "end": v(-24.98, -16.63) * mm});
            skLineSegment(sketch, "E6.0.2.96", {"start": v(17.97, -13.85) * mm, "end": v(20.74, -13.85) * mm});
            skLineSegment(sketch, "E6.0.2.99", {"start": v(25.59, -16.63) * mm, "end": v(28.36, -16.63) * mm});
            skLineSegment(sketch, "E6.0.2.101", {"start": v(-27.75, -13.85) * mm, "end": v(-27.75, -16.63) * mm});
            skLineSegment(sketch, "E6.0.2.104", {"start": v(-27.75, -13.85) * mm, "end": v(-24.98, -13.85) * mm});
            skLineSegment(sketch, "E6.0.2.105", {"start": v(-4.9, -13.85) * mm, "end": v(-2.12, -13.85) * mm});
            skLineSegment(sketch, "E6.0.2.106", {"start": v(-2.12, -13.85) * mm, "end": v(-2.12, -16.63) * mm});
            skPoint(sketch, "E6.0.3.0", {"position": v(19.35, -22.86) * mm});
            skPoint(sketch, "E6.0.3.1", {"position": v(-18.75, -22.86) * mm});
            skPoint(sketch, "E6.0.3.2", {"position": v(30.78, -26.67) * mm});
            skPoint(sketch, "E6.0.3.3", {"position": v(11.73, -22.86) * mm});
            skPoint(sketch, "E6.0.3.4", {"position": v(-7.32, -26.67) * mm});
            skPoint(sketch, "E6.0.3.5", {"position": v(-14.94, -26.67) * mm});
            skPoint(sketch, "E6.0.3.6", {"position": v(-22.56, -26.67) * mm});
            skPoint(sketch, "E6.0.3.7", {"position": v(-3.5, -22.86) * mm});
            skPoint(sketch, "E6.0.3.10", {"position": v(-26.37, -22.86) * mm});
            skPoint(sketch, "E6.0.3.11", {"position": v(-11.13, -22.86) * mm});
            skPoint(sketch, "E6.0.3.12", {"position": v(0.3, -26.67) * mm});
            skPoint(sketch, "E6.0.3.13", {"position": v(15.54, -26.67) * mm});
            skPoint(sketch, "E6.0.3.14", {"position": v(7.92, -26.67) * mm});
            skPoint(sketch, "E6.0.3.15", {"position": v(26.97, -22.86) * mm});
            skPoint(sketch, "E6.0.3.16", {"position": v(4.11, -22.86) * mm});
            skPoint(sketch, "E6.0.3.17", {"position": v(-30.18, -26.67) * mm});
            skPoint(sketch, "E6.0.3.19", {"position": v(23.16, -26.67) * mm});
            skPoint(sketch, "E6.0.3.21", {"position": v(0, -22.86) * mm});
            skLineSegment(sketch, "E6.0.3.22", {"start": v(-4.9, -21.47) * mm, "end": v(-4.9, -24.25) * mm});
            skLineSegment(sketch, "E6.0.3.23", {"start": v(-1.08, -28.06) * mm, "end": v(1.7, -28.06) * mm});
            skLineSegment(sketch, "E6.0.3.24", {"start": v(21.78, -28.06) * mm, "end": v(24.55, -28.06) * mm});
            skLineSegment(sketch, "E6.0.3.25", {"start": v(9.31, -25.28) * mm, "end": v(9.31, -28.06) * mm});
            skLineSegment(sketch, "E6.0.3.27", {"start": v(-17.36, -21.47) * mm, "end": v(-17.36, -24.25) * mm});
            skLineSegment(sketch, "E6.0.3.28", {"start": v(-16.32, -28.06) * mm, "end": v(-13.55, -28.06) * mm});
            skLineSegment(sketch, "E6.0.3.29", {"start": v(-20.13, -21.47) * mm, "end": v(-20.13, -24.25) * mm});
            skLineSegment(sketch, "E6.0.3.30", {"start": v(-23.94, -28.06) * mm, "end": v(-21.17, -28.06) * mm});
            skLineSegment(sketch, "E6.0.3.31", {"start": v(-20.13, -21.47) * mm, "end": v(-17.36, -21.47) * mm});
            skLineSegment(sketch, "E6.0.3.32", {"start": v(-21.17, -25.28) * mm, "end": v(-21.17, -28.06) * mm});
            skLineSegment(sketch, "E6.0.3.35", {"start": v(29.4, -28.06) * mm, "end": v(32.17, -28.06) * mm});
            skLineSegment(sketch, "E6.0.3.36", {"start": v(6.54, -25.28) * mm, "end": v(9.31, -25.28) * mm});
            skLineSegment(sketch, "E6.0.3.37", {"start": v(-12.51, -24.25) * mm, "end": v(-9.74, -24.25) * mm});
            skLineSegment(sketch, "E6.0.3.38", {"start": v(14.16, -25.28) * mm, "end": v(16.93, -25.28) * mm});
            skLineSegment(sketch, "E6.0.3.39", {"start": v(-5.93, -25.28) * mm, "end": v(-5.93, -28.06) * mm});
            skLineSegment(sketch, "E6.0.3.40", {"start": v(-23.94, -25.28) * mm, "end": v(-21.17, -25.28) * mm});
            skLineSegment(sketch, "E6.0.3.41", {"start": v(6.54, -28.06) * mm, "end": v(9.31, -28.06) * mm});
            skLineSegment(sketch, "E6.0.3.42", {"start": v(14.16, -28.06) * mm, "end": v(16.93, -28.06) * mm});
            skLineSegment(sketch, "E6.0.3.43", {"start": v(17.97, -21.47) * mm, "end": v(17.97, -24.25) * mm});
            skLineSegment(sketch, "E6.0.3.44", {"start": v(32.17, -25.28) * mm, "end": v(32.17, -28.06) * mm});
            skLineSegment(sketch, "E6.0.3.45", {"start": v(20.74, -21.47) * mm, "end": v(20.74, -24.25) * mm});
            skLineSegment(sketch, "E6.0.3.46", {"start": v(17.97, -24.25) * mm, "end": v(20.74, -24.25) * mm});
            skLineSegment(sketch, "E6.0.3.47", {"start": v(-8.7, -28.06) * mm, "end": v(-5.93, -28.06) * mm});
            skLineSegment(sketch, "E6.0.3.48", {"start": v(24.55, -25.28) * mm, "end": v(24.55, -28.06) * mm});
            skLineSegment(sketch, "E6.0.3.49", {"start": v(-20.13, -24.25) * mm, "end": v(-17.36, -24.25) * mm});
            skLineSegment(sketch, "E6.0.3.51", {"start": v(28.36, -21.47) * mm, "end": v(28.36, -24.25) * mm});
            skLineSegment(sketch, "E6.0.3.52", {"start": v(-9.74, -21.47) * mm, "end": v(-9.74, -24.25) * mm});
            skLineSegment(sketch, "E6.0.3.53", {"start": v(-13.55, -25.28) * mm, "end": v(-13.55, -28.06) * mm});
            skLineSegment(sketch, "E6.0.3.54", {"start": v(-8.7, -25.28) * mm, "end": v(-5.93, -25.28) * mm});
            skLineSegment(sketch, "E6.0.3.55", {"start": v(-31.56, -28.06) * mm, "end": v(-28.79, -28.06) * mm});
            skLineSegment(sketch, "E6.0.3.56", {"start": v(-23.94, -25.28) * mm, "end": v(-23.94, -28.06) * mm});
            skLineSegment(sketch, "E6.0.3.57", {"start": v(-31.56, -25.28) * mm, "end": v(-31.56, -28.06) * mm});
            skLineSegment(sketch, "E6.0.3.58", {"start": v(16.93, -25.28) * mm, "end": v(16.93, -28.06) * mm});
            skLineSegment(sketch, "E6.0.3.59", {"start": v(5.5, -21.47) * mm, "end": v(5.5, -24.25) * mm});
            skLineSegment(sketch, "E6.0.3.60", {"start": v(-4.9, -24.25) * mm, "end": v(-2.12, -24.25) * mm});
            skLineSegment(sketch, "E6.0.3.61", {"start": v(-28.79, -25.28) * mm, "end": v(-28.79, -28.06) * mm});
            skLineSegment(sketch, "E6.0.3.62", {"start": v(2.73, -24.25) * mm, "end": v(5.5, -24.25) * mm});
            skLineSegment(sketch, "E6.0.3.64", {"start": v(29.4, -25.28) * mm, "end": v(29.4, -28.06) * mm});
            skLineSegment(sketch, "E6.0.3.65", {"start": v(21.78, -25.28) * mm, "end": v(24.55, -25.28) * mm});
            skLineSegment(sketch, "E6.0.3.66", {"start": v(6.54, -25.28) * mm, "end": v(6.54, -28.06) * mm});
            skLineSegment(sketch, "E6.0.3.67", {"start": v(-31.56, -25.28) * mm, "end": v(-28.79, -25.28) * mm});
            skLineSegment(sketch, "E6.0.3.68", {"start": v(21.78, -25.28) * mm, "end": v(21.78, -28.06) * mm});
            skLineSegment(sketch, "E6.0.3.70", {"start": v(13.12, -21.47) * mm, "end": v(13.12, -24.25) * mm});
            skLineSegment(sketch, "E6.0.3.71", {"start": v(10.35, -21.47) * mm, "end": v(13.12, -21.47) * mm});
            skLineSegment(sketch, "E6.0.3.72", {"start": v(-8.7, -25.28) * mm, "end": v(-8.7, -28.06) * mm});
            skLineSegment(sketch, "E6.0.3.73", {"start": v(14.16, -25.28) * mm, "end": v(14.16, -28.06) * mm});
            skLineSegment(sketch, "E6.0.3.75", {"start": v(-16.32, -25.28) * mm, "end": v(-16.32, -28.06) * mm});
            skLineSegment(sketch, "E6.0.3.77", {"start": v(-1.08, -25.28) * mm, "end": v(-1.08, -28.06) * mm});
            skLineSegment(sketch, "E6.0.3.78", {"start": v(-12.51, -21.47) * mm, "end": v(-12.51, -24.25) * mm});
            skLineSegment(sketch, "E6.0.3.79", {"start": v(1.7, -25.28) * mm, "end": v(1.7, -28.06) * mm});
            skLineSegment(sketch, "E6.0.3.80", {"start": v(-12.51, -21.47) * mm, "end": v(-9.74, -21.47) * mm});
            skLineSegment(sketch, "E6.0.3.82", {"start": v(2.73, -21.47) * mm, "end": v(2.73, -24.25) * mm});
            skLineSegment(sketch, "E6.0.3.83", {"start": v(10.35, -21.47) * mm, "end": v(10.35, -24.25) * mm});
            skLineSegment(sketch, "E6.0.3.85", {"start": v(-16.32, -25.28) * mm, "end": v(-13.55, -25.28) * mm});
            skLineSegment(sketch, "E6.0.3.86", {"start": v(2.73, -21.47) * mm, "end": v(5.5, -21.47) * mm});
            skLineSegment(sketch, "E6.0.3.87", {"start": v(25.59, -21.47) * mm, "end": v(25.59, -24.25) * mm});
            skLineSegment(sketch, "E6.0.3.88", {"start": v(10.35, -24.25) * mm, "end": v(13.12, -24.25) * mm});
            skLineSegment(sketch, "E6.0.3.90", {"start": v(-1.08, -25.28) * mm, "end": v(1.7, -25.28) * mm});
            skLineSegment(sketch, "E6.0.3.92", {"start": v(29.4, -25.28) * mm, "end": v(32.17, -25.28) * mm});
            skLineSegment(sketch, "E6.0.3.93", {"start": v(25.59, -21.47) * mm, "end": v(28.36, -21.47) * mm});
            skLineSegment(sketch, "E6.0.3.94", {"start": v(-27.75, -24.25) * mm, "end": v(-24.98, -24.25) * mm});
            skLineSegment(sketch, "E6.0.3.95", {"start": v(-24.98, -21.47) * mm, "end": v(-24.98, -24.25) * mm});
            skLineSegment(sketch, "E6.0.3.96", {"start": v(17.97, -21.47) * mm, "end": v(20.74, -21.47) * mm});
            skLineSegment(sketch, "E6.0.3.99", {"start": v(25.59, -24.25) * mm, "end": v(28.36, -24.25) * mm});
            skLineSegment(sketch, "E6.0.3.101", {"start": v(-27.75, -21.47) * mm, "end": v(-27.75, -24.25) * mm});
            skLineSegment(sketch, "E6.0.3.104", {"start": v(-27.75, -21.47) * mm, "end": v(-24.98, -21.47) * mm});
            skLineSegment(sketch, "E6.0.3.105", {"start": v(-4.9, -21.47) * mm, "end": v(-2.12, -21.47) * mm});
            skLineSegment(sketch, "E6.0.3.106", {"start": v(-2.12, -21.47) * mm, "end": v(-2.12, -24.25) * mm});
            skPoint(sketch, "E6.0.4.0", {"position": v(19.35, -30.48) * mm});
            skPoint(sketch, "E6.0.4.1", {"position": v(-18.75, -30.48) * mm});
            skPoint(sketch, "E6.0.4.3", {"position": v(11.73, -30.48) * mm});
            skPoint(sketch, "E6.0.4.7", {"position": v(-3.5, -30.48) * mm});
            skPoint(sketch, "E6.0.4.10", {"position": v(-26.37, -30.48) * mm});
            skPoint(sketch, "E6.0.4.11", {"position": v(-11.13, -30.48) * mm});
            skPoint(sketch, "E6.0.4.15", {"position": v(26.97, -30.48) * mm});
            skPoint(sketch, "E6.0.4.16", {"position": v(4.11, -30.48) * mm});
            skPoint(sketch, "E6.0.4.21", {"position": v(0, -30.48) * mm});
            skLineSegment(sketch, "E6.0.4.22", {"start": v(-4.9, -29.1) * mm, "end": v(-4.9, -31.87) * mm});
            skLineSegment(sketch, "E6.0.4.27", {"start": v(-17.36, -29.1) * mm, "end": v(-17.36, -31.87) * mm});
            skLineSegment(sketch, "E6.0.4.29", {"start": v(-20.13, -29.1) * mm, "end": v(-20.13, -31.87) * mm});
            skLineSegment(sketch, "E6.0.4.31", {"start": v(-20.13, -29.1) * mm, "end": v(-17.36, -29.1) * mm});
            skLineSegment(sketch, "E6.0.4.37", {"start": v(-12.51, -31.87) * mm, "end": v(-9.74, -31.87) * mm});
            skLineSegment(sketch, "E6.0.4.43", {"start": v(17.97, -29.1) * mm, "end": v(17.97, -31.87) * mm});
            skLineSegment(sketch, "E6.0.4.45", {"start": v(20.74, -29.1) * mm, "end": v(20.74, -31.87) * mm});
            skLineSegment(sketch, "E6.0.4.46", {"start": v(17.97, -31.87) * mm, "end": v(20.74, -31.87) * mm});
            skLineSegment(sketch, "E6.0.4.49", {"start": v(-20.13, -31.87) * mm, "end": v(-17.36, -31.87) * mm});
            skLineSegment(sketch, "E6.0.4.51", {"start": v(28.36, -29.1) * mm, "end": v(28.36, -31.87) * mm});
            skLineSegment(sketch, "E6.0.4.52", {"start": v(-9.74, -29.1) * mm, "end": v(-9.74, -31.87) * mm});
            skLineSegment(sketch, "E6.0.4.59", {"start": v(5.5, -29.1) * mm, "end": v(5.5, -31.87) * mm});
            skLineSegment(sketch, "E6.0.4.60", {"start": v(-4.9, -31.87) * mm, "end": v(-2.12, -31.87) * mm});
            skLineSegment(sketch, "E6.0.4.62", {"start": v(2.73, -31.87) * mm, "end": v(5.5, -31.87) * mm});
            skLineSegment(sketch, "E6.0.4.70", {"start": v(13.12, -29.1) * mm, "end": v(13.12, -31.87) * mm});
            skLineSegment(sketch, "E6.0.4.71", {"start": v(10.35, -29.1) * mm, "end": v(13.12, -29.1) * mm});
            skLineSegment(sketch, "E6.0.4.78", {"start": v(-12.51, -29.1) * mm, "end": v(-12.51, -31.87) * mm});
            skLineSegment(sketch, "E6.0.4.80", {"start": v(-12.51, -29.1) * mm, "end": v(-9.74, -29.1) * mm});
            skLineSegment(sketch, "E6.0.4.82", {"start": v(2.73, -29.1) * mm, "end": v(2.73, -31.87) * mm});
            skLineSegment(sketch, "E6.0.4.83", {"start": v(10.35, -29.1) * mm, "end": v(10.35, -31.87) * mm});
            skLineSegment(sketch, "E6.0.4.86", {"start": v(2.73, -29.1) * mm, "end": v(5.5, -29.1) * mm});
            skLineSegment(sketch, "E6.0.4.87", {"start": v(25.59, -29.1) * mm, "end": v(25.59, -31.87) * mm});
            skLineSegment(sketch, "E6.0.4.88", {"start": v(10.35, -31.87) * mm, "end": v(13.12, -31.87) * mm});
            skLineSegment(sketch, "E6.0.4.93", {"start": v(25.59, -29.1) * mm, "end": v(28.36, -29.1) * mm});
            skLineSegment(sketch, "E6.0.4.94", {"start": v(-27.75, -31.87) * mm, "end": v(-24.98, -31.87) * mm});
            skLineSegment(sketch, "E6.0.4.95", {"start": v(-24.98, -29.1) * mm, "end": v(-24.98, -31.87) * mm});
            skLineSegment(sketch, "E6.0.4.96", {"start": v(17.97, -29.1) * mm, "end": v(20.74, -29.1) * mm});
            skLineSegment(sketch, "E6.0.4.99", {"start": v(25.59, -31.87) * mm, "end": v(28.36, -31.87) * mm});
            skLineSegment(sketch, "E6.0.4.101", {"start": v(-27.75, -29.1) * mm, "end": v(-27.75, -31.87) * mm});
            skLineSegment(sketch, "E6.0.4.104", {"start": v(-27.75, -29.1) * mm, "end": v(-24.98, -29.1) * mm});
            skLineSegment(sketch, "E6.0.4.105", {"start": v(-4.9, -29.1) * mm, "end": v(-2.12, -29.1) * mm});
            skLineSegment(sketch, "E6.0.4.106", {"start": v(-2.12, -29.1) * mm, "end": v(-2.12, -31.87) * mm});
            skPoint(sketch, "E6.0.7.2", {"position": v(30.78, -57.15) * mm});
            skPoint(sketch, "E6.0.7.4", {"position": v(-7.32, -57.15) * mm});
            skPoint(sketch, "E6.0.7.5", {"position": v(-14.94, -57.15) * mm});
            skPoint(sketch, "E6.0.7.6", {"position": v(-22.56, -57.15) * mm});
            skPoint(sketch, "E6.0.7.12", {"position": v(0.3, -57.15) * mm});
            skPoint(sketch, "E6.0.7.13", {"position": v(15.54, -57.15) * mm});
            skPoint(sketch, "E6.0.7.14", {"position": v(7.92, -57.15) * mm});
            skPoint(sketch, "E6.0.7.17", {"position": v(-30.18, -57.15) * mm});
            skPoint(sketch, "E6.0.7.19", {"position": v(23.16, -57.15) * mm});
            skLineSegment(sketch, "E6.0.7.23", {"start": v(-1.08, -58.54) * mm, "end": v(1.7, -58.54) * mm});
            skLineSegment(sketch, "E6.0.7.24", {"start": v(21.78, -58.54) * mm, "end": v(24.55, -58.54) * mm});
            skLineSegment(sketch, "E6.0.7.25", {"start": v(9.31, -55.76) * mm, "end": v(9.31, -58.54) * mm});
            skLineSegment(sketch, "E6.0.7.28", {"start": v(-16.32, -58.54) * mm, "end": v(-13.55, -58.54) * mm});
            skLineSegment(sketch, "E6.0.7.30", {"start": v(-23.94, -58.54) * mm, "end": v(-21.17, -58.54) * mm});
            skLineSegment(sketch, "E6.0.7.32", {"start": v(-21.17, -55.76) * mm, "end": v(-21.17, -58.54) * mm});
            skLineSegment(sketch, "E6.0.7.35", {"start": v(29.4, -58.54) * mm, "end": v(32.17, -58.54) * mm});
            skLineSegment(sketch, "E6.0.7.36", {"start": v(6.54, -55.76) * mm, "end": v(9.31, -55.76) * mm});
            skLineSegment(sketch, "E6.0.7.38", {"start": v(14.16, -55.76) * mm, "end": v(16.93, -55.76) * mm});
            skLineSegment(sketch, "E6.0.7.39", {"start": v(-5.93, -55.76) * mm, "end": v(-5.93, -58.54) * mm});
            skLineSegment(sketch, "E6.0.7.40", {"start": v(-23.94, -55.76) * mm, "end": v(-21.17, -55.76) * mm});
            skLineSegment(sketch, "E6.0.7.41", {"start": v(6.54, -58.54) * mm, "end": v(9.31, -58.54) * mm});
            skLineSegment(sketch, "E6.0.7.42", {"start": v(14.16, -58.54) * mm, "end": v(16.93, -58.54) * mm});
            skLineSegment(sketch, "E6.0.7.44", {"start": v(32.17, -55.76) * mm, "end": v(32.17, -58.54) * mm});
            skLineSegment(sketch, "E6.0.7.47", {"start": v(-8.7, -58.54) * mm, "end": v(-5.93, -58.54) * mm});
            skLineSegment(sketch, "E6.0.7.48", {"start": v(24.55, -55.76) * mm, "end": v(24.55, -58.54) * mm});
            skLineSegment(sketch, "E6.0.7.53", {"start": v(-13.55, -55.76) * mm, "end": v(-13.55, -58.54) * mm});
            skLineSegment(sketch, "E6.0.7.54", {"start": v(-8.7, -55.76) * mm, "end": v(-5.93, -55.76) * mm});
            skLineSegment(sketch, "E6.0.7.55", {"start": v(-31.56, -58.54) * mm, "end": v(-28.79, -58.54) * mm});
            skLineSegment(sketch, "E6.0.7.56", {"start": v(-23.94, -55.76) * mm, "end": v(-23.94, -58.54) * mm});
            skLineSegment(sketch, "E6.0.7.57", {"start": v(-31.56, -55.76) * mm, "end": v(-31.56, -58.54) * mm});
            skLineSegment(sketch, "E6.0.7.58", {"start": v(16.93, -55.76) * mm, "end": v(16.93, -58.54) * mm});
            skLineSegment(sketch, "E6.0.7.61", {"start": v(-28.79, -55.76) * mm, "end": v(-28.79, -58.54) * mm});
            skLineSegment(sketch, "E6.0.7.64", {"start": v(29.4, -55.76) * mm, "end": v(29.4, -58.54) * mm});
            skLineSegment(sketch, "E6.0.7.65", {"start": v(21.78, -55.76) * mm, "end": v(24.55, -55.76) * mm});
            skLineSegment(sketch, "E6.0.7.66", {"start": v(6.54, -55.76) * mm, "end": v(6.54, -58.54) * mm});
            skLineSegment(sketch, "E6.0.7.67", {"start": v(-31.56, -55.76) * mm, "end": v(-28.79, -55.76) * mm});
            skLineSegment(sketch, "E6.0.7.68", {"start": v(21.78, -55.76) * mm, "end": v(21.78, -58.54) * mm});
            skLineSegment(sketch, "E6.0.7.72", {"start": v(-8.7, -55.76) * mm, "end": v(-8.7, -58.54) * mm});
            skLineSegment(sketch, "E6.0.7.73", {"start": v(14.16, -55.76) * mm, "end": v(14.16, -58.54) * mm});
            skLineSegment(sketch, "E6.0.7.75", {"start": v(-16.32, -55.76) * mm, "end": v(-16.32, -58.54) * mm});
            skLineSegment(sketch, "E6.0.7.77", {"start": v(-1.08, -55.76) * mm, "end": v(-1.08, -58.54) * mm});
            skLineSegment(sketch, "E6.0.7.79", {"start": v(1.7, -55.76) * mm, "end": v(1.7, -58.54) * mm});
            skLineSegment(sketch, "E6.0.7.85", {"start": v(-16.32, -55.76) * mm, "end": v(-13.55, -55.76) * mm});
            skLineSegment(sketch, "E6.0.7.90", {"start": v(-1.08, -55.76) * mm, "end": v(1.7, -55.76) * mm});
            skLineSegment(sketch, "E6.0.7.92", {"start": v(29.4, -55.76) * mm, "end": v(32.17, -55.76) * mm});
            skPoint(sketch, "E6.0.8.0", {"position": v(19.35, -60.96) * mm});
            skPoint(sketch, "E6.0.8.1", {"position": v(-18.75, -60.96) * mm});
            skPoint(sketch, "E6.0.8.2", {"position": v(30.78, -64.77) * mm});
            skPoint(sketch, "E6.0.8.3", {"position": v(11.73, -60.96) * mm});
            skPoint(sketch, "E6.0.8.4", {"position": v(-7.32, -64.77) * mm});
            skPoint(sketch, "E6.0.8.5", {"position": v(-14.94, -64.77) * mm});
            skPoint(sketch, "E6.0.8.6", {"position": v(-22.56, -64.77) * mm});
            skPoint(sketch, "E6.0.8.7", {"position": v(-3.5, -60.96) * mm});
            skPoint(sketch, "E6.0.8.10", {"position": v(-26.37, -60.96) * mm});
            skPoint(sketch, "E6.0.8.11", {"position": v(-11.13, -60.96) * mm});
            skPoint(sketch, "E6.0.8.12", {"position": v(0.3, -64.77) * mm});
            skPoint(sketch, "E6.0.8.13", {"position": v(15.54, -64.77) * mm});
            skPoint(sketch, "E6.0.8.14", {"position": v(7.92, -64.77) * mm});
            skPoint(sketch, "E6.0.8.15", {"position": v(26.97, -60.96) * mm});
            skPoint(sketch, "E6.0.8.16", {"position": v(4.11, -60.96) * mm});
            skPoint(sketch, "E6.0.8.17", {"position": v(-30.18, -64.77) * mm});
            skPoint(sketch, "E6.0.8.19", {"position": v(23.16, -64.77) * mm});
            skPoint(sketch, "E6.0.8.21", {"position": v(0, -60.96) * mm});
            skLineSegment(sketch, "E6.0.8.22", {"start": v(-4.9, -59.57) * mm, "end": v(-4.9, -62.35) * mm});
            skLineSegment(sketch, "E6.0.8.23", {"start": v(-1.08, -66.16) * mm, "end": v(1.7, -66.16) * mm});
            skLineSegment(sketch, "E6.0.8.24", {"start": v(21.78, -66.16) * mm, "end": v(24.55, -66.16) * mm});
            skLineSegment(sketch, "E6.0.8.25", {"start": v(9.31, -63.38) * mm, "end": v(9.31, -66.16) * mm});
            skLineSegment(sketch, "E6.0.8.27", {"start": v(-17.36, -59.57) * mm, "end": v(-17.36, -62.35) * mm});
            skLineSegment(sketch, "E6.0.8.28", {"start": v(-16.32, -66.16) * mm, "end": v(-13.55, -66.16) * mm});
            skLineSegment(sketch, "E6.0.8.29", {"start": v(-20.13, -59.57) * mm, "end": v(-20.13, -62.35) * mm});
            skLineSegment(sketch, "E6.0.8.30", {"start": v(-23.94, -66.16) * mm, "end": v(-21.17, -66.16) * mm});
            skLineSegment(sketch, "E6.0.8.31", {"start": v(-20.13, -59.57) * mm, "end": v(-17.36, -59.57) * mm});
            skLineSegment(sketch, "E6.0.8.32", {"start": v(-21.17, -63.38) * mm, "end": v(-21.17, -66.16) * mm});
            skLineSegment(sketch, "E6.0.8.35", {"start": v(29.4, -66.16) * mm, "end": v(32.17, -66.16) * mm});
            skLineSegment(sketch, "E6.0.8.36", {"start": v(6.54, -63.38) * mm, "end": v(9.31, -63.38) * mm});
            skLineSegment(sketch, "E6.0.8.37", {"start": v(-12.51, -62.35) * mm, "end": v(-9.74, -62.35) * mm});
            skLineSegment(sketch, "E6.0.8.38", {"start": v(14.16, -63.38) * mm, "end": v(16.93, -63.38) * mm});
            skLineSegment(sketch, "E6.0.8.39", {"start": v(-5.93, -63.38) * mm, "end": v(-5.93, -66.16) * mm});
            skLineSegment(sketch, "E6.0.8.40", {"start": v(-23.94, -63.38) * mm, "end": v(-21.17, -63.38) * mm});
            skLineSegment(sketch, "E6.0.8.41", {"start": v(6.54, -66.16) * mm, "end": v(9.31, -66.16) * mm});
            skLineSegment(sketch, "E6.0.8.42", {"start": v(14.16, -66.16) * mm, "end": v(16.93, -66.16) * mm});
            skLineSegment(sketch, "E6.0.8.43", {"start": v(17.97, -59.57) * mm, "end": v(17.97, -62.35) * mm});
            skLineSegment(sketch, "E6.0.8.44", {"start": v(32.17, -63.38) * mm, "end": v(32.17, -66.16) * mm});
            skLineSegment(sketch, "E6.0.8.45", {"start": v(20.74, -59.57) * mm, "end": v(20.74, -62.35) * mm});
            skLineSegment(sketch, "E6.0.8.46", {"start": v(17.97, -62.35) * mm, "end": v(20.74, -62.35) * mm});
            skLineSegment(sketch, "E6.0.8.47", {"start": v(-8.7, -66.16) * mm, "end": v(-5.93, -66.16) * mm});
            skLineSegment(sketch, "E6.0.8.48", {"start": v(24.55, -63.38) * mm, "end": v(24.55, -66.16) * mm});
            skLineSegment(sketch, "E6.0.8.49", {"start": v(-20.13, -62.35) * mm, "end": v(-17.36, -62.35) * mm});
            skLineSegment(sketch, "E6.0.8.51", {"start": v(28.36, -59.57) * mm, "end": v(28.36, -62.35) * mm});
            skLineSegment(sketch, "E6.0.8.52", {"start": v(-9.74, -59.57) * mm, "end": v(-9.74, -62.35) * mm});
            skLineSegment(sketch, "E6.0.8.53", {"start": v(-13.55, -63.38) * mm, "end": v(-13.55, -66.16) * mm});
            skLineSegment(sketch, "E6.0.8.54", {"start": v(-8.7, -63.38) * mm, "end": v(-5.93, -63.38) * mm});
            skLineSegment(sketch, "E6.0.8.55", {"start": v(-31.56, -66.16) * mm, "end": v(-28.79, -66.16) * mm});
            skLineSegment(sketch, "E6.0.8.56", {"start": v(-23.94, -63.38) * mm, "end": v(-23.94, -66.16) * mm});
            skLineSegment(sketch, "E6.0.8.57", {"start": v(-31.56, -63.38) * mm, "end": v(-31.56, -66.16) * mm});
            skLineSegment(sketch, "E6.0.8.58", {"start": v(16.93, -63.38) * mm, "end": v(16.93, -66.16) * mm});
            skLineSegment(sketch, "E6.0.8.59", {"start": v(5.5, -59.57) * mm, "end": v(5.5, -62.35) * mm});
            skLineSegment(sketch, "E6.0.8.60", {"start": v(-4.9, -62.35) * mm, "end": v(-2.12, -62.35) * mm});
            skLineSegment(sketch, "E6.0.8.61", {"start": v(-28.79, -63.38) * mm, "end": v(-28.79, -66.16) * mm});
            skLineSegment(sketch, "E6.0.8.62", {"start": v(2.73, -62.35) * mm, "end": v(5.5, -62.35) * mm});
            skLineSegment(sketch, "E6.0.8.64", {"start": v(29.4, -63.38) * mm, "end": v(29.4, -66.16) * mm});
            skLineSegment(sketch, "E6.0.8.65", {"start": v(21.78, -63.38) * mm, "end": v(24.55, -63.38) * mm});
            skLineSegment(sketch, "E6.0.8.66", {"start": v(6.54, -63.38) * mm, "end": v(6.54, -66.16) * mm});
            skLineSegment(sketch, "E6.0.8.67", {"start": v(-31.56, -63.38) * mm, "end": v(-28.79, -63.38) * mm});
            skLineSegment(sketch, "E6.0.8.68", {"start": v(21.78, -63.38) * mm, "end": v(21.78, -66.16) * mm});
            skLineSegment(sketch, "E6.0.8.70", {"start": v(13.12, -59.57) * mm, "end": v(13.12, -62.35) * mm});
            skLineSegment(sketch, "E6.0.8.71", {"start": v(10.35, -59.57) * mm, "end": v(13.12, -59.57) * mm});
            skLineSegment(sketch, "E6.0.8.72", {"start": v(-8.7, -63.38) * mm, "end": v(-8.7, -66.16) * mm});
            skLineSegment(sketch, "E6.0.8.73", {"start": v(14.16, -63.38) * mm, "end": v(14.16, -66.16) * mm});
            skLineSegment(sketch, "E6.0.8.75", {"start": v(-16.32, -63.38) * mm, "end": v(-16.32, -66.16) * mm});
            skLineSegment(sketch, "E6.0.8.77", {"start": v(-1.08, -63.38) * mm, "end": v(-1.08, -66.16) * mm});
            skLineSegment(sketch, "E6.0.8.78", {"start": v(-12.51, -59.57) * mm, "end": v(-12.51, -62.35) * mm});
            skLineSegment(sketch, "E6.0.8.79", {"start": v(1.7, -63.38) * mm, "end": v(1.7, -66.16) * mm});
            skLineSegment(sketch, "E6.0.8.80", {"start": v(-12.51, -59.57) * mm, "end": v(-9.74, -59.57) * mm});
            skLineSegment(sketch, "E6.0.8.82", {"start": v(2.73, -59.57) * mm, "end": v(2.73, -62.35) * mm});
            skLineSegment(sketch, "E6.0.8.83", {"start": v(10.35, -59.57) * mm, "end": v(10.35, -62.35) * mm});
            skLineSegment(sketch, "E6.0.8.85", {"start": v(-16.32, -63.38) * mm, "end": v(-13.55, -63.38) * mm});
            skLineSegment(sketch, "E6.0.8.86", {"start": v(2.73, -59.57) * mm, "end": v(5.5, -59.57) * mm});
            skLineSegment(sketch, "E6.0.8.87", {"start": v(25.59, -59.57) * mm, "end": v(25.59, -62.35) * mm});
            skLineSegment(sketch, "E6.0.8.88", {"start": v(10.35, -62.35) * mm, "end": v(13.12, -62.35) * mm});
            skLineSegment(sketch, "E6.0.8.90", {"start": v(-1.08, -63.38) * mm, "end": v(1.7, -63.38) * mm});
            skLineSegment(sketch, "E6.0.8.92", {"start": v(29.4, -63.38) * mm, "end": v(32.17, -63.38) * mm});
            skLineSegment(sketch, "E6.0.8.93", {"start": v(25.59, -59.57) * mm, "end": v(28.36, -59.57) * mm});
            skLineSegment(sketch, "E6.0.8.94", {"start": v(-27.75, -62.35) * mm, "end": v(-24.98, -62.35) * mm});
            skLineSegment(sketch, "E6.0.8.95", {"start": v(-24.98, -59.57) * mm, "end": v(-24.98, -62.35) * mm});
            skLineSegment(sketch, "E6.0.8.96", {"start": v(17.97, -59.57) * mm, "end": v(20.74, -59.57) * mm});
            skLineSegment(sketch, "E6.0.8.99", {"start": v(25.59, -62.35) * mm, "end": v(28.36, -62.35) * mm});
            skLineSegment(sketch, "E6.0.8.101", {"start": v(-27.75, -59.57) * mm, "end": v(-27.75, -62.35) * mm});
            skLineSegment(sketch, "E6.0.8.104", {"start": v(-27.75, -59.57) * mm, "end": v(-24.98, -59.57) * mm});
            skLineSegment(sketch, "E6.0.8.105", {"start": v(-4.9, -59.57) * mm, "end": v(-2.12, -59.57) * mm});
            skLineSegment(sketch, "E6.0.8.106", {"start": v(-2.12, -59.57) * mm, "end": v(-2.12, -62.35) * mm});
            skPoint(sketch, "E6.0.9.0", {"position": v(19.35, -68.58) * mm});
            skPoint(sketch, "E6.0.9.1", {"position": v(-18.75, -68.58) * mm});
            skPoint(sketch, "E6.0.9.2", {"position": v(30.78, -72.39) * mm});
            skPoint(sketch, "E6.0.9.3", {"position": v(11.73, -68.58) * mm});
            skPoint(sketch, "E6.0.9.4", {"position": v(-7.32, -72.39) * mm});
            skPoint(sketch, "E6.0.9.5", {"position": v(-14.94, -72.39) * mm});
            skPoint(sketch, "E6.0.9.6", {"position": v(-22.56, -72.39) * mm});
            skPoint(sketch, "E6.0.9.7", {"position": v(-3.5, -68.58) * mm});
            skPoint(sketch, "E6.0.9.10", {"position": v(-26.37, -68.58) * mm});
            skPoint(sketch, "E6.0.9.11", {"position": v(-11.13, -68.58) * mm});
            skPoint(sketch, "E6.0.9.12", {"position": v(0.3, -72.39) * mm});
            skPoint(sketch, "E6.0.9.13", {"position": v(15.54, -72.39) * mm});
            skPoint(sketch, "E6.0.9.14", {"position": v(7.92, -72.39) * mm});
            skPoint(sketch, "E6.0.9.15", {"position": v(26.97, -68.58) * mm});
            skPoint(sketch, "E6.0.9.16", {"position": v(4.11, -68.58) * mm});
            skPoint(sketch, "E6.0.9.17", {"position": v(-30.18, -72.39) * mm});
            skPoint(sketch, "E6.0.9.19", {"position": v(23.16, -72.39) * mm});
            skPoint(sketch, "E6.0.9.21", {"position": v(0, -68.58) * mm});
            skLineSegment(sketch, "E6.0.9.22", {"start": v(-4.9, -67.2) * mm, "end": v(-4.9, -69.97) * mm});
            skLineSegment(sketch, "E6.0.9.23", {"start": v(-1.08, -73.78) * mm, "end": v(1.7, -73.78) * mm});
            skLineSegment(sketch, "E6.0.9.24", {"start": v(21.78, -73.78) * mm, "end": v(24.55, -73.78) * mm});
            skLineSegment(sketch, "E6.0.9.25", {"start": v(9.31, -71) * mm, "end": v(9.31, -73.78) * mm});
            skLineSegment(sketch, "E6.0.9.27", {"start": v(-17.36, -67.2) * mm, "end": v(-17.36, -69.97) * mm});
            skLineSegment(sketch, "E6.0.9.28", {"start": v(-16.32, -73.78) * mm, "end": v(-13.55, -73.78) * mm});
            skLineSegment(sketch, "E6.0.9.29", {"start": v(-20.13, -67.2) * mm, "end": v(-20.13, -69.97) * mm});
            skLineSegment(sketch, "E6.0.9.30", {"start": v(-23.94, -73.78) * mm, "end": v(-21.17, -73.78) * mm});
            skLineSegment(sketch, "E6.0.9.31", {"start": v(-20.13, -67.2) * mm, "end": v(-17.36, -67.2) * mm});
            skLineSegment(sketch, "E6.0.9.32", {"start": v(-21.17, -71) * mm, "end": v(-21.17, -73.78) * mm});
            skLineSegment(sketch, "E6.0.9.35", {"start": v(29.4, -73.78) * mm, "end": v(32.17, -73.78) * mm});
            skLineSegment(sketch, "E6.0.9.36", {"start": v(6.54, -71) * mm, "end": v(9.31, -71) * mm});
            skLineSegment(sketch, "E6.0.9.37", {"start": v(-12.51, -69.97) * mm, "end": v(-9.74, -69.97) * mm});
            skLineSegment(sketch, "E6.0.9.38", {"start": v(14.16, -71) * mm, "end": v(16.93, -71) * mm});
            skLineSegment(sketch, "E6.0.9.39", {"start": v(-5.93, -71) * mm, "end": v(-5.93, -73.78) * mm});
            skLineSegment(sketch, "E6.0.9.40", {"start": v(-23.94, -71) * mm, "end": v(-21.17, -71) * mm});
            skLineSegment(sketch, "E6.0.9.41", {"start": v(6.54, -73.78) * mm, "end": v(9.31, -73.78) * mm});
            skLineSegment(sketch, "E6.0.9.42", {"start": v(14.16, -73.78) * mm, "end": v(16.93, -73.78) * mm});
            skLineSegment(sketch, "E6.0.9.43", {"start": v(17.97, -67.2) * mm, "end": v(17.97, -69.97) * mm});
            skLineSegment(sketch, "E6.0.9.44", {"start": v(32.17, -71) * mm, "end": v(32.17, -73.78) * mm});
            skLineSegment(sketch, "E6.0.9.45", {"start": v(20.74, -67.2) * mm, "end": v(20.74, -69.97) * mm});
            skLineSegment(sketch, "E6.0.9.46", {"start": v(17.97, -69.97) * mm, "end": v(20.74, -69.97) * mm});
            skLineSegment(sketch, "E6.0.9.47", {"start": v(-8.7, -73.78) * mm, "end": v(-5.93, -73.78) * mm});
            skLineSegment(sketch, "E6.0.9.48", {"start": v(24.55, -71) * mm, "end": v(24.55, -73.78) * mm});
            skLineSegment(sketch, "E6.0.9.49", {"start": v(-20.13, -69.97) * mm, "end": v(-17.36, -69.97) * mm});
            skLineSegment(sketch, "E6.0.9.51", {"start": v(28.36, -67.2) * mm, "end": v(28.36, -69.97) * mm});
            skLineSegment(sketch, "E6.0.9.52", {"start": v(-9.74, -67.2) * mm, "end": v(-9.74, -69.97) * mm});
            skLineSegment(sketch, "E6.0.9.53", {"start": v(-13.55, -71) * mm, "end": v(-13.55, -73.78) * mm});
            skLineSegment(sketch, "E6.0.9.54", {"start": v(-8.7, -71) * mm, "end": v(-5.93, -71) * mm});
            skLineSegment(sketch, "E6.0.9.55", {"start": v(-31.56, -73.78) * mm, "end": v(-28.79, -73.78) * mm});
            skLineSegment(sketch, "E6.0.9.56", {"start": v(-23.94, -71) * mm, "end": v(-23.94, -73.78) * mm});
            skLineSegment(sketch, "E6.0.9.57", {"start": v(-31.56, -71) * mm, "end": v(-31.56, -73.78) * mm});
            skLineSegment(sketch, "E6.0.9.58", {"start": v(16.93, -71) * mm, "end": v(16.93, -73.78) * mm});
            skLineSegment(sketch, "E6.0.9.59", {"start": v(5.5, -67.2) * mm, "end": v(5.5, -69.97) * mm});
            skLineSegment(sketch, "E6.0.9.60", {"start": v(-4.9, -69.97) * mm, "end": v(-2.12, -69.97) * mm});
            skLineSegment(sketch, "E6.0.9.61", {"start": v(-28.79, -71) * mm, "end": v(-28.79, -73.78) * mm});
            skLineSegment(sketch, "E6.0.9.62", {"start": v(2.73, -69.97) * mm, "end": v(5.5, -69.97) * mm});
            skLineSegment(sketch, "E6.0.9.64", {"start": v(29.4, -71) * mm, "end": v(29.4, -73.78) * mm});
            skLineSegment(sketch, "E6.0.9.65", {"start": v(21.78, -71) * mm, "end": v(24.55, -71) * mm});
            skLineSegment(sketch, "E6.0.9.66", {"start": v(6.54, -71) * mm, "end": v(6.54, -73.78) * mm});
            skLineSegment(sketch, "E6.0.9.67", {"start": v(-31.56, -71) * mm, "end": v(-28.79, -71) * mm});
            skLineSegment(sketch, "E6.0.9.68", {"start": v(21.78, -71) * mm, "end": v(21.78, -73.78) * mm});
            skLineSegment(sketch, "E6.0.9.70", {"start": v(13.12, -67.2) * mm, "end": v(13.12, -69.97) * mm});
            skLineSegment(sketch, "E6.0.9.71", {"start": v(10.35, -67.2) * mm, "end": v(13.12, -67.2) * mm});
            skLineSegment(sketch, "E6.0.9.72", {"start": v(-8.7, -71) * mm, "end": v(-8.7, -73.78) * mm});
            skLineSegment(sketch, "E6.0.9.73", {"start": v(14.16, -71) * mm, "end": v(14.16, -73.78) * mm});
            skLineSegment(sketch, "E6.0.9.75", {"start": v(-16.32, -71) * mm, "end": v(-16.32, -73.78) * mm});
            skLineSegment(sketch, "E6.0.9.77", {"start": v(-1.08, -71) * mm, "end": v(-1.08, -73.78) * mm});
            skLineSegment(sketch, "E6.0.9.78", {"start": v(-12.51, -67.2) * mm, "end": v(-12.51, -69.97) * mm});
            skLineSegment(sketch, "E6.0.9.79", {"start": v(1.7, -71) * mm, "end": v(1.7, -73.78) * mm});
            skLineSegment(sketch, "E6.0.9.80", {"start": v(-12.51, -67.2) * mm, "end": v(-9.74, -67.2) * mm});
            skLineSegment(sketch, "E6.0.9.82", {"start": v(2.73, -67.2) * mm, "end": v(2.73, -69.97) * mm});
            skLineSegment(sketch, "E6.0.9.83", {"start": v(10.35, -67.2) * mm, "end": v(10.35, -69.97) * mm});
            skLineSegment(sketch, "E6.0.9.85", {"start": v(-16.32, -71) * mm, "end": v(-13.55, -71) * mm});
            skLineSegment(sketch, "E6.0.9.86", {"start": v(2.73, -67.2) * mm, "end": v(5.5, -67.2) * mm});
            skLineSegment(sketch, "E6.0.9.87", {"start": v(25.59, -67.2) * mm, "end": v(25.59, -69.97) * mm});
            skLineSegment(sketch, "E6.0.9.88", {"start": v(10.35, -69.97) * mm, "end": v(13.12, -69.97) * mm});
            skLineSegment(sketch, "E6.0.9.90", {"start": v(-1.08, -71) * mm, "end": v(1.7, -71) * mm});
            skLineSegment(sketch, "E6.0.9.92", {"start": v(29.4, -71) * mm, "end": v(32.17, -71) * mm});
            skLineSegment(sketch, "E6.0.9.93", {"start": v(25.59, -67.2) * mm, "end": v(28.36, -67.2) * mm});
            skLineSegment(sketch, "E6.0.9.94", {"start": v(-27.75, -69.97) * mm, "end": v(-24.98, -69.97) * mm});
            skLineSegment(sketch, "E6.0.9.95", {"start": v(-24.98, -67.2) * mm, "end": v(-24.98, -69.97) * mm});
            skLineSegment(sketch, "E6.0.9.96", {"start": v(17.97, -67.2) * mm, "end": v(20.74, -67.2) * mm});
            skLineSegment(sketch, "E6.0.9.99", {"start": v(25.59, -69.97) * mm, "end": v(28.36, -69.97) * mm});
            skLineSegment(sketch, "E6.0.9.101", {"start": v(-27.75, -67.2) * mm, "end": v(-27.75, -69.97) * mm});
            skLineSegment(sketch, "E6.0.9.104", {"start": v(-27.75, -67.2) * mm, "end": v(-24.98, -67.2) * mm});
            skLineSegment(sketch, "E6.0.9.105", {"start": v(-4.9, -67.2) * mm, "end": v(-2.12, -67.2) * mm});
            skLineSegment(sketch, "E6.0.9.106", {"start": v(-2.12, -67.2) * mm, "end": v(-2.12, -69.97) * mm});
            skPoint(sketch, "E7.3.0.0", {"position": v(61.26, 11.43) * mm});
            skPoint(sketch, "E7.3.0.1", {"position": v(57.45, -15.24) * mm});
            skPoint(sketch, "E7.3.0.2", {"position": v(61.26, 26.67) * mm});
            skPoint(sketch, "E7.3.0.3", {"position": v(57.45, 30.48) * mm});
            skPoint(sketch, "E7.3.0.4", {"position": v(57.45, 22.86) * mm});
            skPoint(sketch, "E7.3.0.5", {"position": v(61.26, 3.81) * mm});
            skPoint(sketch, "E7.3.0.6", {"position": v(57.45, -30.48) * mm});
            skPoint(sketch, "E7.3.0.7", {"position": v(61.26, -19.05) * mm});
            skPoint(sketch, "E7.3.0.9", {"position": v(57.45, 0) * mm});
            skPoint(sketch, "E7.3.0.10", {"position": v(61.26, -11.43) * mm});
            skPoint(sketch, "E7.3.0.11", {"position": v(61.26, -3.8) * mm});
            skPoint(sketch, "E7.3.0.12", {"position": v(57.45, -22.86) * mm});
            skPoint(sketch, "E7.3.0.13", {"position": v(61.26, -26.67) * mm});
            skPoint(sketch, "E7.3.0.14", {"position": v(61.26, 19.05) * mm});
            skPoint(sketch, "E7.3.0.15", {"position": v(57.45, 7.62) * mm});
            skPoint(sketch, "E7.3.0.16", {"position": v(57.45, 15.24) * mm});
            skPoint(sketch, "E7.3.0.17", {"position": v(57.45, -7.62) * mm});
            skLineSegment(sketch, "E7.3.0.18", {"start": v(62.65, -25.28) * mm, "end": v(62.65, -28.06) * mm});
            skLineSegment(sketch, "E7.3.0.19", {"start": v(56.07, -16.63) * mm, "end": v(58.84, -16.63) * mm});
            skLineSegment(sketch, "E7.3.0.20", {"start": v(59.88, -20.44) * mm, "end": v(62.65, -20.44) * mm});
            skLineSegment(sketch, "E7.3.0.21", {"start": v(56.07, -24.25) * mm, "end": v(58.84, -24.25) * mm});
            skLineSegment(sketch, "E7.3.0.22", {"start": v(59.88, -12.82) * mm, "end": v(62.65, -12.82) * mm});
            skLineSegment(sketch, "E7.3.0.23", {"start": v(59.88, -28.06) * mm, "end": v(62.65, -28.06) * mm});
            skLineSegment(sketch, "E7.3.0.24", {"start": v(62.65, 20.44) * mm, "end": v(62.65, 17.66) * mm});
            skLineSegment(sketch, "E7.3.0.25", {"start": v(59.88, 20.44) * mm, "end": v(62.65, 20.44) * mm});
            skLineSegment(sketch, "E7.3.0.26", {"start": v(59.88, -2.42) * mm, "end": v(62.65, -2.42) * mm});
            skLineSegment(sketch, "E7.3.0.27", {"start": v(62.65, -17.66) * mm, "end": v(62.65, -20.44) * mm});
            skLineSegment(sketch, "E7.3.0.28", {"start": v(62.65, -2.42) * mm, "end": v(62.65, -5.2) * mm});
            skLineSegment(sketch, "E7.3.0.29", {"start": v(59.88, 2.42) * mm, "end": v(62.65, 2.42) * mm});
            skLineSegment(sketch, "E7.3.0.30", {"start": v(59.88, 25.28) * mm, "end": v(62.65, 25.28) * mm});
            skLineSegment(sketch, "E7.3.0.31", {"start": v(59.88, 12.82) * mm, "end": v(62.65, 12.82) * mm});
            skLineSegment(sketch, "E7.3.0.32", {"start": v(62.65, 12.82) * mm, "end": v(62.65, 10.04) * mm});
            skLineSegment(sketch, "E7.3.0.33", {"start": v(59.88, -10.04) * mm, "end": v(62.65, -10.04) * mm});
            skLineSegment(sketch, "E7.3.0.34", {"start": v(59.88, -5.2) * mm, "end": v(62.65, -5.2) * mm});
            skLineSegment(sketch, "E7.3.0.35", {"start": v(59.88, 17.66) * mm, "end": v(62.65, 17.66) * mm});
            skLineSegment(sketch, "E7.3.0.36", {"start": v(59.88, 5.2) * mm, "end": v(62.65, 5.2) * mm});
            skLineSegment(sketch, "E7.3.0.37", {"start": v(62.65, 5.2) * mm, "end": v(62.65, 2.42) * mm});
            skLineSegment(sketch, "E7.3.0.38", {"start": v(62.65, -10.04) * mm, "end": v(62.65, -12.82) * mm});
            skLineSegment(sketch, "E7.3.0.39", {"start": v(59.88, 28.06) * mm, "end": v(62.65, 28.06) * mm});
            skLineSegment(sketch, "E7.3.0.40", {"start": v(62.65, 28.06) * mm, "end": v(62.65, 25.28) * mm});
            skLineSegment(sketch, "E7.3.0.41", {"start": v(59.88, -10.04) * mm, "end": v(59.88, -12.82) * mm});
            skLineSegment(sketch, "E7.3.0.42", {"start": v(59.88, 10.04) * mm, "end": v(62.65, 10.04) * mm});
            skLineSegment(sketch, "E7.3.0.43", {"start": v(59.88, -25.28) * mm, "end": v(62.65, -25.28) * mm});
            skLineSegment(sketch, "E7.3.0.44", {"start": v(56.07, -21.47) * mm, "end": v(56.07, -24.25) * mm});
            skLineSegment(sketch, "E7.3.0.45", {"start": v(59.88, -17.66) * mm, "end": v(62.65, -17.66) * mm});
            skLineSegment(sketch, "E7.3.0.46", {"start": v(56.07, -29.1) * mm, "end": v(58.84, -29.1) * mm});
            skLineSegment(sketch, "E7.3.0.47", {"start": v(56.07, -1.39) * mm, "end": v(58.84, -1.39) * mm});
            skLineSegment(sketch, "E7.3.0.48", {"start": v(56.07, -21.47) * mm, "end": v(58.84, -21.47) * mm});
            skLineSegment(sketch, "E7.3.0.49", {"start": v(56.07, -29.1) * mm, "end": v(56.07, -31.87) * mm});
            skLineSegment(sketch, "E7.3.0.50", {"start": v(56.07, -13.85) * mm, "end": v(56.07, -16.63) * mm});
            skLineSegment(sketch, "E7.3.0.51", {"start": v(58.84, -29.1) * mm, "end": v(58.84, -31.87) * mm});
            skLineSegment(sketch, "E7.3.0.52", {"start": v(56.07, 21.47) * mm, "end": v(58.84, 21.47) * mm});
            skLineSegment(sketch, "E7.3.0.53", {"start": v(59.88, -17.66) * mm, "end": v(59.88, -20.44) * mm});
            skLineSegment(sketch, "E7.3.0.54", {"start": v(59.88, -25.28) * mm, "end": v(59.88, -28.06) * mm});
            skLineSegment(sketch, "E7.3.0.55", {"start": v(59.88, 12.82) * mm, "end": v(59.88, 10.04) * mm});
            skLineSegment(sketch, "E7.3.0.56", {"start": v(58.84, -21.47) * mm, "end": v(58.84, -24.25) * mm});
            skLineSegment(sketch, "E7.3.0.57", {"start": v(56.07, 9) * mm, "end": v(58.84, 9) * mm});
            skLineSegment(sketch, "E7.3.0.58", {"start": v(56.07, 16.63) * mm, "end": v(56.07, 13.85) * mm});
            skLineSegment(sketch, "E7.3.0.59", {"start": v(58.84, 24.25) * mm, "end": v(58.84, 21.47) * mm});
            skLineSegment(sketch, "E7.3.0.60", {"start": v(56.07, -6.23) * mm, "end": v(56.07, -9) * mm});
            skLineSegment(sketch, "E7.3.0.61", {"start": v(58.84, 1.39) * mm, "end": v(58.84, -1.39) * mm});
            skLineSegment(sketch, "E7.3.0.62", {"start": v(58.84, -6.23) * mm, "end": v(58.84, -9) * mm});
            skLineSegment(sketch, "E7.3.0.63", {"start": v(56.07, 1.39) * mm, "end": v(58.84, 1.39) * mm});
            skLineSegment(sketch, "E7.3.0.64", {"start": v(58.84, 16.63) * mm, "end": v(58.84, 13.85) * mm});
            skLineSegment(sketch, "E7.3.0.65", {"start": v(56.07, -6.23) * mm, "end": v(58.84, -6.23) * mm});
            skLineSegment(sketch, "E7.3.0.66", {"start": v(56.07, 9) * mm, "end": v(56.07, 6.23) * mm});
            skLineSegment(sketch, "E7.3.0.67", {"start": v(56.07, 31.87) * mm, "end": v(56.07, 29.1) * mm});
            skLineSegment(sketch, "E7.3.0.68", {"start": v(56.07, 24.25) * mm, "end": v(58.84, 24.25) * mm});
            skLineSegment(sketch, "E7.3.0.69", {"start": v(56.07, 13.85) * mm, "end": v(58.84, 13.85) * mm});
            skLineSegment(sketch, "E7.3.0.70", {"start": v(59.88, 5.2) * mm, "end": v(59.88, 2.42) * mm});
            skLineSegment(sketch, "E7.3.0.71", {"start": v(59.88, 28.06) * mm, "end": v(59.88, 25.28) * mm});
            skLineSegment(sketch, "E7.3.0.72", {"start": v(56.07, 1.39) * mm, "end": v(56.07, -1.39) * mm});
            skLineSegment(sketch, "E7.3.0.73", {"start": v(58.84, 9) * mm, "end": v(58.84, 6.23) * mm});
            skLineSegment(sketch, "E7.3.0.74", {"start": v(56.07, 24.25) * mm, "end": v(56.07, 21.47) * mm});
            skLineSegment(sketch, "E7.3.0.75", {"start": v(56.07, 16.63) * mm, "end": v(58.84, 16.63) * mm});
            skLineSegment(sketch, "E7.3.0.76", {"start": v(59.88, -2.42) * mm, "end": v(59.88, -5.2) * mm});
            skLineSegment(sketch, "E7.3.0.77", {"start": v(56.07, 6.23) * mm, "end": v(58.84, 6.23) * mm});
            skLineSegment(sketch, "E7.3.0.78", {"start": v(56.07, -9) * mm, "end": v(58.84, -9) * mm});
            skLineSegment(sketch, "E7.3.0.79", {"start": v(56.07, -13.85) * mm, "end": v(58.84, -13.85) * mm});
            skLineSegment(sketch, "E7.3.0.80", {"start": v(56.07, 29.1) * mm, "end": v(58.84, 29.1) * mm});
            skLineSegment(sketch, "E7.3.0.81", {"start": v(59.88, 20.44) * mm, "end": v(59.88, 17.66) * mm});
            skLineSegment(sketch, "E7.3.0.82", {"start": v(58.84, -13.85) * mm, "end": v(58.84, -16.63) * mm});
            skLineSegment(sketch, "E7.3.0.83", {"start": v(56.07, 31.87) * mm, "end": v(58.84, 31.87) * mm});
            skLineSegment(sketch, "E7.3.0.84", {"start": v(58.84, 31.87) * mm, "end": v(58.84, 29.1) * mm});
            skLineSegment(sketch, "E7.3.0.85", {"start": v(56.07, -31.87) * mm, "end": v(58.84, -31.87) * mm});
            skPoint(sketch, "E7.4.0.0", {"position": v(68.88, 11.43) * mm});
            skPoint(sketch, "E7.4.0.1", {"position": v(65.07, -15.24) * mm});
            skPoint(sketch, "E7.4.0.2", {"position": v(68.88, 26.67) * mm});
            skPoint(sketch, "E7.4.0.3", {"position": v(65.07, 30.48) * mm});
            skPoint(sketch, "E7.4.0.4", {"position": v(65.07, 22.86) * mm});
            skPoint(sketch, "E7.4.0.5", {"position": v(68.88, 3.81) * mm});
            skPoint(sketch, "E7.4.0.6", {"position": v(65.07, -30.48) * mm});
            skPoint(sketch, "E7.4.0.7", {"position": v(68.88, -19.05) * mm});
            skPoint(sketch, "E7.4.0.9", {"position": v(65.07, 0) * mm});
            skPoint(sketch, "E7.4.0.10", {"position": v(68.88, -11.43) * mm});
            skPoint(sketch, "E7.4.0.11", {"position": v(68.88, -3.8) * mm});
            skPoint(sketch, "E7.4.0.12", {"position": v(65.07, -22.86) * mm});
            skPoint(sketch, "E7.4.0.13", {"position": v(68.88, -26.67) * mm});
            skPoint(sketch, "E7.4.0.14", {"position": v(68.88, 19.05) * mm});
            skPoint(sketch, "E7.4.0.15", {"position": v(65.07, 7.62) * mm});
            skPoint(sketch, "E7.4.0.16", {"position": v(65.07, 15.24) * mm});
            skPoint(sketch, "E7.4.0.17", {"position": v(65.07, -7.62) * mm});
            skLineSegment(sketch, "E7.4.0.18", {"start": v(70.27, -25.28) * mm, "end": v(70.27, -28.06) * mm});
            skLineSegment(sketch, "E7.4.0.19", {"start": v(63.69, -16.63) * mm, "end": v(66.46, -16.63) * mm});
            skLineSegment(sketch, "E7.4.0.20", {"start": v(67.5, -20.44) * mm, "end": v(70.27, -20.44) * mm});
            skLineSegment(sketch, "E7.4.0.21", {"start": v(63.69, -24.25) * mm, "end": v(66.46, -24.25) * mm});
            skLineSegment(sketch, "E7.4.0.22", {"start": v(67.5, -12.82) * mm, "end": v(70.27, -12.82) * mm});
            skLineSegment(sketch, "E7.4.0.23", {"start": v(67.5, -28.06) * mm, "end": v(70.27, -28.06) * mm});
            skLineSegment(sketch, "E7.4.0.24", {"start": v(70.27, 20.44) * mm, "end": v(70.27, 17.66) * mm});
            skLineSegment(sketch, "E7.4.0.25", {"start": v(67.5, 20.44) * mm, "end": v(70.27, 20.44) * mm});
            skLineSegment(sketch, "E7.4.0.26", {"start": v(67.5, -2.42) * mm, "end": v(70.27, -2.42) * mm});
            skLineSegment(sketch, "E7.4.0.27", {"start": v(70.27, -17.66) * mm, "end": v(70.27, -20.44) * mm});
            skLineSegment(sketch, "E7.4.0.28", {"start": v(70.27, -2.42) * mm, "end": v(70.27, -5.2) * mm});
            skLineSegment(sketch, "E7.4.0.29", {"start": v(67.5, 2.42) * mm, "end": v(70.27, 2.42) * mm});
            skLineSegment(sketch, "E7.4.0.30", {"start": v(67.5, 25.28) * mm, "end": v(70.27, 25.28) * mm});
            skLineSegment(sketch, "E7.4.0.31", {"start": v(67.5, 12.82) * mm, "end": v(70.27, 12.82) * mm});
            skLineSegment(sketch, "E7.4.0.32", {"start": v(70.27, 12.82) * mm, "end": v(70.27, 10.04) * mm});
            skLineSegment(sketch, "E7.4.0.33", {"start": v(67.5, -10.04) * mm, "end": v(70.27, -10.04) * mm});
            skLineSegment(sketch, "E7.4.0.34", {"start": v(67.5, -5.2) * mm, "end": v(70.27, -5.2) * mm});
            skLineSegment(sketch, "E7.4.0.35", {"start": v(67.5, 17.66) * mm, "end": v(70.27, 17.66) * mm});
            skLineSegment(sketch, "E7.4.0.36", {"start": v(67.5, 5.2) * mm, "end": v(70.27, 5.2) * mm});
            skLineSegment(sketch, "E7.4.0.37", {"start": v(70.27, 5.2) * mm, "end": v(70.27, 2.42) * mm});
            skLineSegment(sketch, "E7.4.0.38", {"start": v(70.27, -10.04) * mm, "end": v(70.27, -12.82) * mm});
            skLineSegment(sketch, "E7.4.0.39", {"start": v(67.5, 28.06) * mm, "end": v(70.27, 28.06) * mm});
            skLineSegment(sketch, "E7.4.0.40", {"start": v(70.27, 28.06) * mm, "end": v(70.27, 25.28) * mm});
            skLineSegment(sketch, "E7.4.0.41", {"start": v(67.5, -10.04) * mm, "end": v(67.5, -12.82) * mm});
            skLineSegment(sketch, "E7.4.0.42", {"start": v(67.5, 10.04) * mm, "end": v(70.27, 10.04) * mm});
            skLineSegment(sketch, "E7.4.0.43", {"start": v(67.5, -25.28) * mm, "end": v(70.27, -25.28) * mm});
            skLineSegment(sketch, "E7.4.0.44", {"start": v(63.69, -21.47) * mm, "end": v(63.69, -24.25) * mm});
            skLineSegment(sketch, "E7.4.0.45", {"start": v(67.5, -17.66) * mm, "end": v(70.27, -17.66) * mm});
            skLineSegment(sketch, "E7.4.0.46", {"start": v(63.69, -29.1) * mm, "end": v(66.46, -29.1) * mm});
            skLineSegment(sketch, "E7.4.0.47", {"start": v(63.69, -1.39) * mm, "end": v(66.46, -1.39) * mm});
            skLineSegment(sketch, "E7.4.0.48", {"start": v(63.69, -21.47) * mm, "end": v(66.46, -21.47) * mm});
            skLineSegment(sketch, "E7.4.0.49", {"start": v(63.69, -29.1) * mm, "end": v(63.69, -31.87) * mm});
            skLineSegment(sketch, "E7.4.0.50", {"start": v(63.69, -13.85) * mm, "end": v(63.69, -16.63) * mm});
            skLineSegment(sketch, "E7.4.0.51", {"start": v(66.46, -29.1) * mm, "end": v(66.46, -31.87) * mm});
            skLineSegment(sketch, "E7.4.0.52", {"start": v(63.69, 21.47) * mm, "end": v(66.46, 21.47) * mm});
            skLineSegment(sketch, "E7.4.0.53", {"start": v(67.5, -17.66) * mm, "end": v(67.5, -20.44) * mm});
            skLineSegment(sketch, "E7.4.0.54", {"start": v(67.5, -25.28) * mm, "end": v(67.5, -28.06) * mm});
            skLineSegment(sketch, "E7.4.0.55", {"start": v(67.5, 12.82) * mm, "end": v(67.5, 10.04) * mm});
            skLineSegment(sketch, "E7.4.0.56", {"start": v(66.46, -21.47) * mm, "end": v(66.46, -24.25) * mm});
            skLineSegment(sketch, "E7.4.0.57", {"start": v(63.69, 9) * mm, "end": v(66.46, 9) * mm});
            skLineSegment(sketch, "E7.4.0.58", {"start": v(63.69, 16.63) * mm, "end": v(63.69, 13.85) * mm});
            skLineSegment(sketch, "E7.4.0.59", {"start": v(66.46, 24.25) * mm, "end": v(66.46, 21.47) * mm});
            skLineSegment(sketch, "E7.4.0.60", {"start": v(63.69, -6.23) * mm, "end": v(63.69, -9) * mm});
            skLineSegment(sketch, "E7.4.0.61", {"start": v(66.46, 1.39) * mm, "end": v(66.46, -1.39) * mm});
            skLineSegment(sketch, "E7.4.0.62", {"start": v(66.46, -6.23) * mm, "end": v(66.46, -9) * mm});
            skLineSegment(sketch, "E7.4.0.63", {"start": v(63.69, 1.39) * mm, "end": v(66.46, 1.39) * mm});
            skLineSegment(sketch, "E7.4.0.64", {"start": v(66.46, 16.63) * mm, "end": v(66.46, 13.85) * mm});
            skLineSegment(sketch, "E7.4.0.65", {"start": v(63.69, -6.23) * mm, "end": v(66.46, -6.23) * mm});
            skLineSegment(sketch, "E7.4.0.66", {"start": v(63.69, 9) * mm, "end": v(63.69, 6.23) * mm});
            skLineSegment(sketch, "E7.4.0.67", {"start": v(63.69, 31.87) * mm, "end": v(63.69, 29.1) * mm});
            skLineSegment(sketch, "E7.4.0.68", {"start": v(63.69, 24.25) * mm, "end": v(66.46, 24.25) * mm});
            skLineSegment(sketch, "E7.4.0.69", {"start": v(63.69, 13.85) * mm, "end": v(66.46, 13.85) * mm});
            skLineSegment(sketch, "E7.4.0.70", {"start": v(67.5, 5.2) * mm, "end": v(67.5, 2.42) * mm});
            skLineSegment(sketch, "E7.4.0.71", {"start": v(67.5, 28.06) * mm, "end": v(67.5, 25.28) * mm});
            skLineSegment(sketch, "E7.4.0.72", {"start": v(63.69, 1.39) * mm, "end": v(63.69, -1.39) * mm});
            skLineSegment(sketch, "E7.4.0.73", {"start": v(66.46, 9) * mm, "end": v(66.46, 6.23) * mm});
            skLineSegment(sketch, "E7.4.0.74", {"start": v(63.69, 24.25) * mm, "end": v(63.69, 21.47) * mm});
            skLineSegment(sketch, "E7.4.0.75", {"start": v(63.69, 16.63) * mm, "end": v(66.46, 16.63) * mm});
            skLineSegment(sketch, "E7.4.0.76", {"start": v(67.5, -2.42) * mm, "end": v(67.5, -5.2) * mm});
            skLineSegment(sketch, "E7.4.0.77", {"start": v(63.69, 6.23) * mm, "end": v(66.46, 6.23) * mm});
            skLineSegment(sketch, "E7.4.0.78", {"start": v(63.69, -9) * mm, "end": v(66.46, -9) * mm});
            skLineSegment(sketch, "E7.4.0.79", {"start": v(63.69, -13.85) * mm, "end": v(66.46, -13.85) * mm});
            skLineSegment(sketch, "E7.4.0.80", {"start": v(63.69, 29.1) * mm, "end": v(66.46, 29.1) * mm});
            skLineSegment(sketch, "E7.4.0.81", {"start": v(67.5, 20.44) * mm, "end": v(67.5, 17.66) * mm});
            skLineSegment(sketch, "E7.4.0.82", {"start": v(66.46, -13.85) * mm, "end": v(66.46, -16.63) * mm});
            skLineSegment(sketch, "E7.4.0.83", {"start": v(63.69, 31.87) * mm, "end": v(66.46, 31.87) * mm});
            skLineSegment(sketch, "E7.4.0.84", {"start": v(66.46, 31.87) * mm, "end": v(66.46, 29.1) * mm});
            skLineSegment(sketch, "E7.4.0.85", {"start": v(63.69, -31.87) * mm, "end": v(66.46, -31.87) * mm});
            skPoint(sketch, "E7.5.0.1", {"position": v(72.7, -15.24) * mm});
            skPoint(sketch, "E7.5.0.3", {"position": v(72.7, 30.48) * mm});
            skPoint(sketch, "E7.5.0.4", {"position": v(72.7, 22.86) * mm});
            skPoint(sketch, "E7.5.0.6", {"position": v(72.7, -30.48) * mm});
            skPoint(sketch, "E7.5.0.9", {"position": v(72.7, 0) * mm});
            skPoint(sketch, "E7.5.0.12", {"position": v(72.7, -22.86) * mm});
            skPoint(sketch, "E7.5.0.15", {"position": v(72.7, 7.62) * mm});
            skPoint(sketch, "E7.5.0.16", {"position": v(72.7, 15.24) * mm});
            skPoint(sketch, "E7.5.0.17", {"position": v(72.7, -7.62) * mm});
            skLineSegment(sketch, "E7.5.0.19", {"start": v(71.3, -16.63) * mm, "end": v(74.08, -16.63) * mm});
            skLineSegment(sketch, "E7.5.0.21", {"start": v(71.3, -24.25) * mm, "end": v(74.08, -24.25) * mm});
            skLineSegment(sketch, "E7.5.0.44", {"start": v(71.3, -21.47) * mm, "end": v(71.3, -24.25) * mm});
            skLineSegment(sketch, "E7.5.0.46", {"start": v(71.3, -29.1) * mm, "end": v(74.08, -29.1) * mm});
            skLineSegment(sketch, "E7.5.0.47", {"start": v(71.3, -1.39) * mm, "end": v(74.08, -1.39) * mm});
            skLineSegment(sketch, "E7.5.0.48", {"start": v(71.3, -21.47) * mm, "end": v(74.08, -21.47) * mm});
            skLineSegment(sketch, "E7.5.0.49", {"start": v(71.3, -29.1) * mm, "end": v(71.3, -31.87) * mm});
            skLineSegment(sketch, "E7.5.0.50", {"start": v(71.3, -13.85) * mm, "end": v(71.3, -16.63) * mm});
            skLineSegment(sketch, "E7.5.0.51", {"start": v(74.08, -29.1) * mm, "end": v(74.08, -31.87) * mm});
            skLineSegment(sketch, "E7.5.0.52", {"start": v(71.3, 21.47) * mm, "end": v(74.08, 21.47) * mm});
            skLineSegment(sketch, "E7.5.0.56", {"start": v(74.08, -21.47) * mm, "end": v(74.08, -24.25) * mm});
            skLineSegment(sketch, "E7.5.0.57", {"start": v(71.3, 9) * mm, "end": v(74.08, 9) * mm});
            skLineSegment(sketch, "E7.5.0.58", {"start": v(71.3, 16.63) * mm, "end": v(71.3, 13.85) * mm});
            skLineSegment(sketch, "E7.5.0.59", {"start": v(74.08, 24.25) * mm, "end": v(74.08, 21.47) * mm});
            skLineSegment(sketch, "E7.5.0.60", {"start": v(71.3, -6.23) * mm, "end": v(71.3, -9) * mm});
            skLineSegment(sketch, "E7.5.0.61", {"start": v(74.08, 1.39) * mm, "end": v(74.08, -1.39) * mm});
            skLineSegment(sketch, "E7.5.0.62", {"start": v(74.08, -6.23) * mm, "end": v(74.08, -9) * mm});
            skLineSegment(sketch, "E7.5.0.63", {"start": v(71.3, 1.39) * mm, "end": v(74.08, 1.39) * mm});
            skLineSegment(sketch, "E7.5.0.64", {"start": v(74.08, 16.63) * mm, "end": v(74.08, 13.85) * mm});
            skLineSegment(sketch, "E7.5.0.65", {"start": v(71.3, -6.23) * mm, "end": v(74.08, -6.23) * mm});
            skLineSegment(sketch, "E7.5.0.66", {"start": v(71.3, 9) * mm, "end": v(71.3, 6.23) * mm});
            skLineSegment(sketch, "E7.5.0.67", {"start": v(71.3, 31.87) * mm, "end": v(71.3, 29.1) * mm});
            skLineSegment(sketch, "E7.5.0.68", {"start": v(71.3, 24.25) * mm, "end": v(74.08, 24.25) * mm});
            skLineSegment(sketch, "E7.5.0.69", {"start": v(71.3, 13.85) * mm, "end": v(74.08, 13.85) * mm});
            skLineSegment(sketch, "E7.5.0.72", {"start": v(71.3, 1.39) * mm, "end": v(71.3, -1.39) * mm});
            skLineSegment(sketch, "E7.5.0.73", {"start": v(74.08, 9) * mm, "end": v(74.08, 6.23) * mm});
            skLineSegment(sketch, "E7.5.0.74", {"start": v(71.3, 24.25) * mm, "end": v(71.3, 21.47) * mm});
            skLineSegment(sketch, "E7.5.0.75", {"start": v(71.3, 16.63) * mm, "end": v(74.08, 16.63) * mm});
            skLineSegment(sketch, "E7.5.0.77", {"start": v(71.3, 6.23) * mm, "end": v(74.08, 6.23) * mm});
            skLineSegment(sketch, "E7.5.0.78", {"start": v(71.3, -9) * mm, "end": v(74.08, -9) * mm});
            skLineSegment(sketch, "E7.5.0.79", {"start": v(71.3, -13.85) * mm, "end": v(74.08, -13.85) * mm});
            skLineSegment(sketch, "E7.5.0.80", {"start": v(71.3, 29.1) * mm, "end": v(74.08, 29.1) * mm});
            skLineSegment(sketch, "E7.5.0.82", {"start": v(74.08, -13.85) * mm, "end": v(74.08, -16.63) * mm});
            skLineSegment(sketch, "E7.5.0.83", {"start": v(71.3, 31.87) * mm, "end": v(74.08, 31.87) * mm});
            skLineSegment(sketch, "E7.5.0.84", {"start": v(74.08, 31.87) * mm, "end": v(74.08, 29.1) * mm});
            skLineSegment(sketch, "E7.5.0.85", {"start": v(71.3, -31.87) * mm, "end": v(74.08, -31.87) * mm});
            skPoint(sketch, "E8.3.0.0", {"position": v(-60.66, 19.05) * mm});
            skPoint(sketch, "E8.3.0.1", {"position": v(-56.85, 15.24) * mm});
            skPoint(sketch, "E8.3.0.2", {"position": v(-60.66, -11.43) * mm});
            skPoint(sketch, "E8.3.0.3", {"position": v(-56.85, 7.62) * mm});
            skPoint(sketch, "E8.3.0.4", {"position": v(-60.66, 11.43) * mm});
            skPoint(sketch, "E8.3.0.5", {"position": v(-60.66, -19.05) * mm});
            skPoint(sketch, "E8.3.0.6", {"position": v(-56.85, 0) * mm});
            skPoint(sketch, "E8.3.0.7", {"position": v(-56.85, -22.86) * mm});
            skLineSegment(sketch, "E8.3.0.9", {"start": v(-58.23, -29.1) * mm, "end": v(-58.23, -31.87) * mm});
            skLineSegment(sketch, "E8.3.0.10", {"start": v(-58.23, 31.87) * mm, "end": v(-58.23, 29.1) * mm});
            skPoint(sketch, "E8.3.0.11", {"position": v(-56.85, -15.24) * mm});
            skPoint(sketch, "E8.3.0.12", {"position": v(-60.66, -3.8) * mm});
            skPoint(sketch, "E8.3.0.13", {"position": v(-60.66, 26.67) * mm});
            skPoint(sketch, "E8.3.0.14", {"position": v(-56.85, 30.48) * mm});
            skPoint(sketch, "E8.3.0.15", {"position": v(-56.85, -30.48) * mm});
            skPoint(sketch, "E8.3.0.16", {"position": v(-60.66, -26.67) * mm});
            skPoint(sketch, "E8.3.0.17", {"position": v(-56.85, 22.86) * mm});
            skPoint(sketch, "E8.3.0.18", {"position": v(-56.85, -7.62) * mm});
            skPoint(sketch, "E8.3.0.19", {"position": v(-60.66, 3.81) * mm});
            skLineSegment(sketch, "E8.3.0.20", {"start": v(-55.46, -21.47) * mm, "end": v(-55.46, -24.25) * mm});
            skLineSegment(sketch, "E8.3.0.21", {"start": v(-62.04, -17.66) * mm, "end": v(-62.04, -20.44) * mm});
            skLineSegment(sketch, "E8.3.0.22", {"start": v(-58.23, -9) * mm, "end": v(-55.46, -9) * mm, "construction": true});
            skLineSegment(sketch, "E8.3.0.23", {"start": v(-55.46, 24.25) * mm, "end": v(-55.46, 21.47) * mm});
            skLineSegment(sketch, "E8.3.0.24", {"start": v(-58.23, -29.1) * mm, "end": v(-55.46, -29.1) * mm});
            skLineSegment(sketch, "E8.3.0.25", {"start": v(-58.23, -31.87) * mm, "end": v(-55.46, -31.87) * mm, "construction": true});
            skLineSegment(sketch, "E8.3.0.26", {"start": v(-58.23, -1.39) * mm, "end": v(-55.46, -1.39) * mm, "construction": true});
            skLineSegment(sketch, "E8.3.0.27", {"start": v(-55.46, -29.1) * mm, "end": v(-55.46, -31.87) * mm});
            skLineSegment(sketch, "E8.3.0.28", {"start": v(-58.23, 9) * mm, "end": v(-55.46, 9) * mm});
            skLineSegment(sketch, "E8.3.0.29", {"start": v(-62.04, 28.06) * mm, "end": v(-62.04, 25.28) * mm});
            skLineSegment(sketch, "E8.3.0.30", {"start": v(-58.23, 21.47) * mm, "end": v(-55.46, 21.47) * mm, "construction": true});
            skLineSegment(sketch, "E8.3.0.31", {"start": v(-59.27, -17.66) * mm, "end": v(-59.27, -20.44) * mm});
            skLineSegment(sketch, "E8.3.0.32", {"start": v(-55.46, 1.39) * mm, "end": v(-55.46, -1.39) * mm});
            skLineSegment(sketch, "E8.3.0.33", {"start": v(-59.27, 28.06) * mm, "end": v(-59.27, 25.28) * mm});
            skLineSegment(sketch, "E8.3.0.34", {"start": v(-55.46, 31.87) * mm, "end": v(-55.46, 29.1) * mm});
            skLineSegment(sketch, "E8.3.0.35", {"start": v(-55.46, -6.23) * mm, "end": v(-55.46, -9) * mm});
            skLineSegment(sketch, "E8.3.0.36", {"start": v(-55.46, 9) * mm, "end": v(-55.46, 6.23) * mm});
            skLineSegment(sketch, "E8.3.0.37", {"start": v(-58.23, 16.63) * mm, "end": v(-55.46, 16.63) * mm});
            skLineSegment(sketch, "E8.3.0.38", {"start": v(-58.23, 29.1) * mm, "end": v(-55.46, 29.1) * mm, "construction": true});
            skLineSegment(sketch, "E8.3.0.39", {"start": v(-58.23, 6.23) * mm, "end": v(-55.46, 6.23) * mm, "construction": true});
            skLineSegment(sketch, "E8.3.0.40", {"start": v(-58.23, -13.85) * mm, "end": v(-55.46, -13.85) * mm});
            skLineSegment(sketch, "E8.3.0.41", {"start": v(-55.46, 16.63) * mm, "end": v(-55.46, 13.85) * mm});
            skLineSegment(sketch, "E8.3.0.42", {"start": v(-58.23, 24.25) * mm, "end": v(-55.46, 24.25) * mm});
            skLineSegment(sketch, "E8.3.0.43", {"start": v(-58.23, -6.23) * mm, "end": v(-55.46, -6.23) * mm});
            skLineSegment(sketch, "E8.3.0.44", {"start": v(-58.23, 1.39) * mm, "end": v(-55.46, 1.39) * mm});
            skLineSegment(sketch, "E8.3.0.45", {"start": v(-58.23, 13.85) * mm, "end": v(-55.46, 13.85) * mm, "construction": true});
            skLineSegment(sketch, "E8.3.0.46", {"start": v(-58.23, -24.25) * mm, "end": v(-55.46, -24.25) * mm, "construction": true});
            skLineSegment(sketch, "E8.3.0.47", {"start": v(-55.46, -13.85) * mm, "end": v(-55.46, -16.63) * mm});
            skLineSegment(sketch, "E8.3.0.48", {"start": v(-58.23, -16.63) * mm, "end": v(-55.46, -16.63) * mm, "construction": true});
            skLineSegment(sketch, "E8.3.0.49", {"start": v(-58.23, -21.47) * mm, "end": v(-55.46, -21.47) * mm});
            skLineSegment(sketch, "E8.3.0.50", {"start": v(-62.04, 5.2) * mm, "end": v(-62.04, 2.42) * mm});
            skLineSegment(sketch, "E8.3.0.51", {"start": v(-58.23, 24.25) * mm, "end": v(-58.23, 21.47) * mm});
            skLineSegment(sketch, "E8.3.0.52", {"start": v(-58.23, -31.87) * mm, "end": v(-55.46, -31.87) * mm});
            skLineSegment(sketch, "E8.3.0.53", {"start": v(-58.23, -21.47) * mm, "end": v(-58.23, -24.25) * mm});
            skLineSegment(sketch, "E8.3.0.54", {"start": v(-58.23, -13.85) * mm, "end": v(-58.23, -16.63) * mm});
            skLineSegment(sketch, "E8.3.0.55", {"start": v(-62.04, -28.06) * mm, "end": v(-59.27, -28.06) * mm});
            skLineSegment(sketch, "E8.3.0.56", {"start": v(-62.04, -17.66) * mm, "end": v(-59.27, -17.66) * mm});
            skLineSegment(sketch, "E8.3.0.57", {"start": v(-59.27, -25.28) * mm, "end": v(-59.27, -28.06) * mm});
            skLineSegment(sketch, "E8.3.0.58", {"start": v(-59.27, 20.44) * mm, "end": v(-59.27, 17.66) * mm});
            skLineSegment(sketch, "E8.3.0.59", {"start": v(-62.04, -2.42) * mm, "end": v(-59.27, -2.42) * mm});
            skLineSegment(sketch, "E8.3.0.60", {"start": v(-62.04, 17.66) * mm, "end": v(-59.27, 17.66) * mm});
            skLineSegment(sketch, "E8.3.0.61", {"start": v(-62.04, 5.2) * mm, "end": v(-59.27, 5.2) * mm});
            skLineSegment(sketch, "E8.3.0.62", {"start": v(-59.27, -2.42) * mm, "end": v(-59.27, -5.2) * mm});
            skLineSegment(sketch, "E8.3.0.63", {"start": v(-62.04, 28.06) * mm, "end": v(-59.27, 28.06) * mm});
            skLineSegment(sketch, "E8.3.0.64", {"start": v(-58.23, -1.39) * mm, "end": v(-55.46, -1.39) * mm});
            skLineSegment(sketch, "E8.3.0.65", {"start": v(-62.04, -5.2) * mm, "end": v(-59.27, -5.2) * mm});
            skLineSegment(sketch, "E8.3.0.66", {"start": v(-58.23, 21.47) * mm, "end": v(-55.46, 21.47) * mm});
            skLineSegment(sketch, "E8.3.0.67", {"start": v(-62.04, -10.04) * mm, "end": v(-59.27, -10.04) * mm});
            skLineSegment(sketch, "E8.3.0.68", {"start": v(-58.23, 1.39) * mm, "end": v(-58.23, -1.39) * mm});
            skLineSegment(sketch, "E8.3.0.69", {"start": v(-59.27, 5.2) * mm, "end": v(-59.27, 2.42) * mm});
            skLineSegment(sketch, "E8.3.0.70", {"start": v(-62.04, 25.28) * mm, "end": v(-59.27, 25.28) * mm});
            skLineSegment(sketch, "E8.3.0.71", {"start": v(-58.23, -24.25) * mm, "end": v(-55.46, -24.25) * mm});
            skLineSegment(sketch, "E8.3.0.72", {"start": v(-62.04, 2.42) * mm, "end": v(-59.27, 2.42) * mm});
            skLineSegment(sketch, "E8.3.0.73", {"start": v(-58.23, 29.1) * mm, "end": v(-55.46, 29.1) * mm});
            skLineSegment(sketch, "E8.3.0.74", {"start": v(-58.23, 6.23) * mm, "end": v(-55.46, 6.23) * mm});
            skLineSegment(sketch, "E8.3.0.75", {"start": v(-59.27, -10.04) * mm, "end": v(-59.27, -12.82) * mm});
            skLineSegment(sketch, "E8.3.0.76", {"start": v(-62.04, 12.82) * mm, "end": v(-62.04, 10.04) * mm});
            skLineSegment(sketch, "E8.3.0.77", {"start": v(-58.23, 9) * mm, "end": v(-58.23, 6.23) * mm});
            skLineSegment(sketch, "E8.3.0.78", {"start": v(-62.04, 12.82) * mm, "end": v(-59.27, 12.82) * mm});
            skLineSegment(sketch, "E8.3.0.79", {"start": v(-58.23, -6.23) * mm, "end": v(-58.23, -9) * mm});
            skLineSegment(sketch, "E8.3.0.80", {"start": v(-62.04, -20.44) * mm, "end": v(-59.27, -20.44) * mm});
            skLineSegment(sketch, "E8.3.0.81", {"start": v(-59.27, 12.82) * mm, "end": v(-59.27, 10.04) * mm});
            skLineSegment(sketch, "E8.3.0.82", {"start": v(-58.23, -9) * mm, "end": v(-55.46, -9) * mm});
            skLineSegment(sketch, "E8.3.0.83", {"start": v(-62.04, 10.04) * mm, "end": v(-59.27, 10.04) * mm});
            skLineSegment(sketch, "E8.3.0.84", {"start": v(-62.04, -10.04) * mm, "end": v(-62.04, -12.82) * mm});
            skLineSegment(sketch, "E8.3.0.85", {"start": v(-58.23, 13.85) * mm, "end": v(-55.46, 13.85) * mm});
            skLineSegment(sketch, "E8.3.0.86", {"start": v(-62.04, 20.44) * mm, "end": v(-62.04, 17.66) * mm});
            skLineSegment(sketch, "E8.3.0.87", {"start": v(-58.23, 16.63) * mm, "end": v(-58.23, 13.85) * mm});
            skLineSegment(sketch, "E8.3.0.88", {"start": v(-62.04, 20.44) * mm, "end": v(-59.27, 20.44) * mm});
            skLineSegment(sketch, "E8.3.0.89", {"start": v(-62.04, -2.42) * mm, "end": v(-62.04, -5.2) * mm});
            skLineSegment(sketch, "E8.3.0.90", {"start": v(-62.04, -12.82) * mm, "end": v(-59.27, -12.82) * mm});
            skLineSegment(sketch, "E8.3.0.91", {"start": v(-58.23, -16.63) * mm, "end": v(-55.46, -16.63) * mm});
            skLineSegment(sketch, "E8.3.0.92", {"start": v(-62.04, -25.28) * mm, "end": v(-59.27, -25.28) * mm});
            skLineSegment(sketch, "E8.3.0.93", {"start": v(-62.04, -25.28) * mm, "end": v(-62.04, -28.06) * mm});
            skLineSegment(sketch, "E8.3.0.94", {"start": v(-58.23, 31.87) * mm, "end": v(-55.46, 31.87) * mm});
            skPoint(sketch, "E8.4.0.0", {"position": v(-68.28, 19.05) * mm});
            skPoint(sketch, "E8.4.0.1", {"position": v(-64.47, 15.24) * mm});
            skPoint(sketch, "E8.4.0.2", {"position": v(-68.28, -11.43) * mm});
            skPoint(sketch, "E8.4.0.3", {"position": v(-64.47, 7.62) * mm});
            skPoint(sketch, "E8.4.0.4", {"position": v(-68.28, 11.43) * mm});
            skPoint(sketch, "E8.4.0.5", {"position": v(-68.28, -19.05) * mm});
            skPoint(sketch, "E8.4.0.6", {"position": v(-64.47, 0) * mm});
            skPoint(sketch, "E8.4.0.7", {"position": v(-64.47, -22.86) * mm});
            skLineSegment(sketch, "E8.4.0.9", {"start": v(-65.85, -29.1) * mm, "end": v(-65.85, -31.87) * mm});
            skLineSegment(sketch, "E8.4.0.10", {"start": v(-65.85, 31.87) * mm, "end": v(-65.85, 29.1) * mm});
            skPoint(sketch, "E8.4.0.11", {"position": v(-64.47, -15.24) * mm});
            skPoint(sketch, "E8.4.0.12", {"position": v(-68.28, -3.8) * mm});
            skPoint(sketch, "E8.4.0.13", {"position": v(-68.28, 26.67) * mm});
            skPoint(sketch, "E8.4.0.14", {"position": v(-64.47, 30.48) * mm});
            skPoint(sketch, "E8.4.0.15", {"position": v(-64.47, -30.48) * mm});
            skPoint(sketch, "E8.4.0.16", {"position": v(-68.28, -26.67) * mm});
            skPoint(sketch, "E8.4.0.17", {"position": v(-64.47, 22.86) * mm});
            skPoint(sketch, "E8.4.0.18", {"position": v(-64.47, -7.62) * mm});
            skPoint(sketch, "E8.4.0.19", {"position": v(-68.28, 3.81) * mm});
            skLineSegment(sketch, "E8.4.0.20", {"start": v(-63.08, -21.47) * mm, "end": v(-63.08, -24.25) * mm});
            skLineSegment(sketch, "E8.4.0.21", {"start": v(-69.66, -17.66) * mm, "end": v(-69.66, -20.44) * mm});
            skLineSegment(sketch, "E8.4.0.22", {"start": v(-65.85, -9) * mm, "end": v(-63.08, -9) * mm, "construction": true});
            skLineSegment(sketch, "E8.4.0.23", {"start": v(-63.08, 24.25) * mm, "end": v(-63.08, 21.47) * mm});
            skLineSegment(sketch, "E8.4.0.24", {"start": v(-65.85, -29.1) * mm, "end": v(-63.08, -29.1) * mm});
            skLineSegment(sketch, "E8.4.0.25", {"start": v(-65.85, -31.87) * mm, "end": v(-63.08, -31.87) * mm, "construction": true});
            skLineSegment(sketch, "E8.4.0.26", {"start": v(-65.85, -1.39) * mm, "end": v(-63.08, -1.39) * mm, "construction": true});
            skLineSegment(sketch, "E8.4.0.27", {"start": v(-63.08, -29.1) * mm, "end": v(-63.08, -31.87) * mm});
            skLineSegment(sketch, "E8.4.0.28", {"start": v(-65.85, 9) * mm, "end": v(-63.08, 9) * mm});
            skLineSegment(sketch, "E8.4.0.29", {"start": v(-69.66, 28.06) * mm, "end": v(-69.66, 25.28) * mm});
            skLineSegment(sketch, "E8.4.0.30", {"start": v(-65.85, 21.47) * mm, "end": v(-63.08, 21.47) * mm, "construction": true});
            skLineSegment(sketch, "E8.4.0.31", {"start": v(-66.89, -17.66) * mm, "end": v(-66.89, -20.44) * mm});
            skLineSegment(sketch, "E8.4.0.32", {"start": v(-63.08, 1.39) * mm, "end": v(-63.08, -1.39) * mm});
            skLineSegment(sketch, "E8.4.0.33", {"start": v(-66.89, 28.06) * mm, "end": v(-66.89, 25.28) * mm});
            skLineSegment(sketch, "E8.4.0.34", {"start": v(-63.08, 31.87) * mm, "end": v(-63.08, 29.1) * mm});
            skLineSegment(sketch, "E8.4.0.35", {"start": v(-63.08, -6.23) * mm, "end": v(-63.08, -9) * mm});
            skLineSegment(sketch, "E8.4.0.36", {"start": v(-63.08, 9) * mm, "end": v(-63.08, 6.23) * mm});
            skLineSegment(sketch, "E8.4.0.37", {"start": v(-65.85, 16.63) * mm, "end": v(-63.08, 16.63) * mm});
            skLineSegment(sketch, "E8.4.0.38", {"start": v(-65.85, 29.1) * mm, "end": v(-63.08, 29.1) * mm, "construction": true});
            skLineSegment(sketch, "E8.4.0.39", {"start": v(-65.85, 6.23) * mm, "end": v(-63.08, 6.23) * mm, "construction": true});
            skLineSegment(sketch, "E8.4.0.40", {"start": v(-65.85, -13.85) * mm, "end": v(-63.08, -13.85) * mm});
            skLineSegment(sketch, "E8.4.0.41", {"start": v(-63.08, 16.63) * mm, "end": v(-63.08, 13.85) * mm});
            skLineSegment(sketch, "E8.4.0.42", {"start": v(-65.85, 24.25) * mm, "end": v(-63.08, 24.25) * mm});
            skLineSegment(sketch, "E8.4.0.43", {"start": v(-65.85, -6.23) * mm, "end": v(-63.08, -6.23) * mm});
            skLineSegment(sketch, "E8.4.0.44", {"start": v(-65.85, 1.39) * mm, "end": v(-63.08, 1.39) * mm});
            skLineSegment(sketch, "E8.4.0.45", {"start": v(-65.85, 13.85) * mm, "end": v(-63.08, 13.85) * mm, "construction": true});
            skLineSegment(sketch, "E8.4.0.46", {"start": v(-65.85, -24.25) * mm, "end": v(-63.08, -24.25) * mm, "construction": true});
            skLineSegment(sketch, "E8.4.0.47", {"start": v(-63.08, -13.85) * mm, "end": v(-63.08, -16.63) * mm});
            skLineSegment(sketch, "E8.4.0.48", {"start": v(-65.85, -16.63) * mm, "end": v(-63.08, -16.63) * mm, "construction": true});
            skLineSegment(sketch, "E8.4.0.49", {"start": v(-65.85, -21.47) * mm, "end": v(-63.08, -21.47) * mm});
            skLineSegment(sketch, "E8.4.0.50", {"start": v(-69.66, 5.2) * mm, "end": v(-69.66, 2.42) * mm});
            skLineSegment(sketch, "E8.4.0.51", {"start": v(-65.85, 24.25) * mm, "end": v(-65.85, 21.47) * mm});
            skLineSegment(sketch, "E8.4.0.52", {"start": v(-65.85, -31.87) * mm, "end": v(-63.08, -31.87) * mm});
            skLineSegment(sketch, "E8.4.0.53", {"start": v(-65.85, -21.47) * mm, "end": v(-65.85, -24.25) * mm});
            skLineSegment(sketch, "E8.4.0.54", {"start": v(-65.85, -13.85) * mm, "end": v(-65.85, -16.63) * mm});
            skLineSegment(sketch, "E8.4.0.55", {"start": v(-69.66, -28.06) * mm, "end": v(-66.89, -28.06) * mm});
            skLineSegment(sketch, "E8.4.0.56", {"start": v(-69.66, -17.66) * mm, "end": v(-66.89, -17.66) * mm});
            skLineSegment(sketch, "E8.4.0.57", {"start": v(-66.89, -25.28) * mm, "end": v(-66.89, -28.06) * mm});
            skLineSegment(sketch, "E8.4.0.58", {"start": v(-66.89, 20.44) * mm, "end": v(-66.89, 17.66) * mm});
            skLineSegment(sketch, "E8.4.0.59", {"start": v(-69.66, -2.42) * mm, "end": v(-66.89, -2.42) * mm});
            skLineSegment(sketch, "E8.4.0.60", {"start": v(-69.66, 17.66) * mm, "end": v(-66.89, 17.66) * mm});
            skLineSegment(sketch, "E8.4.0.61", {"start": v(-69.66, 5.2) * mm, "end": v(-66.89, 5.2) * mm});
            skLineSegment(sketch, "E8.4.0.62", {"start": v(-66.89, -2.42) * mm, "end": v(-66.89, -5.2) * mm});
            skLineSegment(sketch, "E8.4.0.63", {"start": v(-69.66, 28.06) * mm, "end": v(-66.89, 28.06) * mm});
            skLineSegment(sketch, "E8.4.0.64", {"start": v(-65.85, -1.39) * mm, "end": v(-63.08, -1.39) * mm});
            skLineSegment(sketch, "E8.4.0.65", {"start": v(-69.66, -5.2) * mm, "end": v(-66.89, -5.2) * mm});
            skLineSegment(sketch, "E8.4.0.66", {"start": v(-65.85, 21.47) * mm, "end": v(-63.08, 21.47) * mm});
            skLineSegment(sketch, "E8.4.0.67", {"start": v(-69.66, -10.04) * mm, "end": v(-66.89, -10.04) * mm});
            skLineSegment(sketch, "E8.4.0.68", {"start": v(-65.85, 1.39) * mm, "end": v(-65.85, -1.39) * mm});
            skLineSegment(sketch, "E8.4.0.69", {"start": v(-66.89, 5.2) * mm, "end": v(-66.89, 2.42) * mm});
            skLineSegment(sketch, "E8.4.0.70", {"start": v(-69.66, 25.28) * mm, "end": v(-66.89, 25.28) * mm});
            skLineSegment(sketch, "E8.4.0.71", {"start": v(-65.85, -24.25) * mm, "end": v(-63.08, -24.25) * mm});
            skLineSegment(sketch, "E8.4.0.72", {"start": v(-69.66, 2.42) * mm, "end": v(-66.89, 2.42) * mm});
            skLineSegment(sketch, "E8.4.0.73", {"start": v(-65.85, 29.1) * mm, "end": v(-63.08, 29.1) * mm});
            skLineSegment(sketch, "E8.4.0.74", {"start": v(-65.85, 6.23) * mm, "end": v(-63.08, 6.23) * mm});
            skLineSegment(sketch, "E8.4.0.75", {"start": v(-66.89, -10.04) * mm, "end": v(-66.89, -12.82) * mm});
            skLineSegment(sketch, "E8.4.0.76", {"start": v(-69.66, 12.82) * mm, "end": v(-69.66, 10.04) * mm});
            skLineSegment(sketch, "E8.4.0.77", {"start": v(-65.85, 9) * mm, "end": v(-65.85, 6.23) * mm});
            skLineSegment(sketch, "E8.4.0.78", {"start": v(-69.66, 12.82) * mm, "end": v(-66.89, 12.82) * mm});
            skLineSegment(sketch, "E8.4.0.79", {"start": v(-65.85, -6.23) * mm, "end": v(-65.85, -9) * mm});
            skLineSegment(sketch, "E8.4.0.80", {"start": v(-69.66, -20.44) * mm, "end": v(-66.89, -20.44) * mm});
            skLineSegment(sketch, "E8.4.0.81", {"start": v(-66.89, 12.82) * mm, "end": v(-66.89, 10.04) * mm});
            skLineSegment(sketch, "E8.4.0.82", {"start": v(-65.85, -9) * mm, "end": v(-63.08, -9) * mm});
            skLineSegment(sketch, "E8.4.0.83", {"start": v(-69.66, 10.04) * mm, "end": v(-66.89, 10.04) * mm});
            skLineSegment(sketch, "E8.4.0.84", {"start": v(-69.66, -10.04) * mm, "end": v(-69.66, -12.82) * mm});
            skLineSegment(sketch, "E8.4.0.85", {"start": v(-65.85, 13.85) * mm, "end": v(-63.08, 13.85) * mm});
            skLineSegment(sketch, "E8.4.0.86", {"start": v(-69.66, 20.44) * mm, "end": v(-69.66, 17.66) * mm});
            skLineSegment(sketch, "E8.4.0.87", {"start": v(-65.85, 16.63) * mm, "end": v(-65.85, 13.85) * mm});
            skLineSegment(sketch, "E8.4.0.88", {"start": v(-69.66, 20.44) * mm, "end": v(-66.89, 20.44) * mm});
            skLineSegment(sketch, "E8.4.0.89", {"start": v(-69.66, -2.42) * mm, "end": v(-69.66, -5.2) * mm});
            skLineSegment(sketch, "E8.4.0.90", {"start": v(-69.66, -12.82) * mm, "end": v(-66.89, -12.82) * mm});
            skLineSegment(sketch, "E8.4.0.91", {"start": v(-65.85, -16.63) * mm, "end": v(-63.08, -16.63) * mm});
            skLineSegment(sketch, "E8.4.0.92", {"start": v(-69.66, -25.28) * mm, "end": v(-66.89, -25.28) * mm});
            skLineSegment(sketch, "E8.4.0.93", {"start": v(-69.66, -25.28) * mm, "end": v(-69.66, -28.06) * mm});
            skLineSegment(sketch, "E8.4.0.94", {"start": v(-65.85, 31.87) * mm, "end": v(-63.08, 31.87) * mm});
            skPoint(sketch, "E8.5.0.1", {"position": v(-72.09, 15.24) * mm});
            skPoint(sketch, "E8.5.0.3", {"position": v(-72.09, 7.62) * mm});
            skPoint(sketch, "E8.5.0.6", {"position": v(-72.09, 0) * mm});
            skPoint(sketch, "E8.5.0.7", {"position": v(-72.09, -22.86) * mm});
            skLineSegment(sketch, "E8.5.0.9", {"start": v(-73.47, -29.1) * mm, "end": v(-73.47, -31.87) * mm});
            skLineSegment(sketch, "E8.5.0.10", {"start": v(-73.47, 31.87) * mm, "end": v(-73.47, 29.1) * mm});
            skPoint(sketch, "E8.5.0.11", {"position": v(-72.09, -15.24) * mm});
            skPoint(sketch, "E8.5.0.14", {"position": v(-72.09, 30.48) * mm});
            skPoint(sketch, "E8.5.0.15", {"position": v(-72.09, -30.48) * mm});
            skPoint(sketch, "E8.5.0.17", {"position": v(-72.09, 22.86) * mm});
            skPoint(sketch, "E8.5.0.18", {"position": v(-72.09, -7.62) * mm});
            skLineSegment(sketch, "E8.5.0.20", {"start": v(-70.7, -21.47) * mm, "end": v(-70.7, -24.25) * mm});
            skLineSegment(sketch, "E8.5.0.22", {"start": v(-73.47, -9) * mm, "end": v(-70.7, -9) * mm, "construction": true});
            skLineSegment(sketch, "E8.5.0.23", {"start": v(-70.7, 24.25) * mm, "end": v(-70.7, 21.47) * mm});
            skLineSegment(sketch, "E8.5.0.24", {"start": v(-73.47, -29.1) * mm, "end": v(-70.7, -29.1) * mm});
            skLineSegment(sketch, "E8.5.0.25", {"start": v(-73.47, -31.87) * mm, "end": v(-70.7, -31.87) * mm, "construction": true});
            skLineSegment(sketch, "E8.5.0.26", {"start": v(-73.47, -1.39) * mm, "end": v(-70.7, -1.39) * mm, "construction": true});
            skLineSegment(sketch, "E8.5.0.27", {"start": v(-70.7, -29.1) * mm, "end": v(-70.7, -31.87) * mm});
            skLineSegment(sketch, "E8.5.0.28", {"start": v(-73.47, 9) * mm, "end": v(-70.7, 9) * mm});
            skLineSegment(sketch, "E8.5.0.30", {"start": v(-73.47, 21.47) * mm, "end": v(-70.7, 21.47) * mm, "construction": true});
            skLineSegment(sketch, "E8.5.0.32", {"start": v(-70.7, 1.39) * mm, "end": v(-70.7, -1.39) * mm});
            skLineSegment(sketch, "E8.5.0.34", {"start": v(-70.7, 31.87) * mm, "end": v(-70.7, 29.1) * mm});
            skLineSegment(sketch, "E8.5.0.35", {"start": v(-70.7, -6.23) * mm, "end": v(-70.7, -9) * mm});
            skLineSegment(sketch, "E8.5.0.36", {"start": v(-70.7, 9) * mm, "end": v(-70.7, 6.23) * mm});
            skLineSegment(sketch, "E8.5.0.37", {"start": v(-73.47, 16.63) * mm, "end": v(-70.7, 16.63) * mm});
            skLineSegment(sketch, "E8.5.0.38", {"start": v(-73.47, 29.1) * mm, "end": v(-70.7, 29.1) * mm, "construction": true});
            skLineSegment(sketch, "E8.5.0.39", {"start": v(-73.47, 6.23) * mm, "end": v(-70.7, 6.23) * mm, "construction": true});
            skLineSegment(sketch, "E8.5.0.40", {"start": v(-73.47, -13.85) * mm, "end": v(-70.7, -13.85) * mm});
            skLineSegment(sketch, "E8.5.0.41", {"start": v(-70.7, 16.63) * mm, "end": v(-70.7, 13.85) * mm});
            skLineSegment(sketch, "E8.5.0.42", {"start": v(-73.47, 24.25) * mm, "end": v(-70.7, 24.25) * mm});
            skLineSegment(sketch, "E8.5.0.43", {"start": v(-73.47, -6.23) * mm, "end": v(-70.7, -6.23) * mm});
            skLineSegment(sketch, "E8.5.0.44", {"start": v(-73.47, 1.39) * mm, "end": v(-70.7, 1.39) * mm});
            skLineSegment(sketch, "E8.5.0.45", {"start": v(-73.47, 13.85) * mm, "end": v(-70.7, 13.85) * mm, "construction": true});
            skLineSegment(sketch, "E8.5.0.46", {"start": v(-73.47, -24.25) * mm, "end": v(-70.7, -24.25) * mm, "construction": true});
            skLineSegment(sketch, "E8.5.0.47", {"start": v(-70.7, -13.85) * mm, "end": v(-70.7, -16.63) * mm});
            skLineSegment(sketch, "E8.5.0.48", {"start": v(-73.47, -16.63) * mm, "end": v(-70.7, -16.63) * mm, "construction": true});
            skLineSegment(sketch, "E8.5.0.49", {"start": v(-73.47, -21.47) * mm, "end": v(-70.7, -21.47) * mm});
            skLineSegment(sketch, "E8.5.0.51", {"start": v(-73.47, 24.25) * mm, "end": v(-73.47, 21.47) * mm});
            skLineSegment(sketch, "E8.5.0.52", {"start": v(-73.47, -31.87) * mm, "end": v(-70.7, -31.87) * mm});
            skLineSegment(sketch, "E8.5.0.53", {"start": v(-73.47, -21.47) * mm, "end": v(-73.47, -24.25) * mm});
            skLineSegment(sketch, "E8.5.0.54", {"start": v(-73.47, -13.85) * mm, "end": v(-73.47, -16.63) * mm});
            skLineSegment(sketch, "E8.5.0.64", {"start": v(-73.47, -1.39) * mm, "end": v(-70.7, -1.39) * mm});
            skLineSegment(sketch, "E8.5.0.66", {"start": v(-73.47, 21.47) * mm, "end": v(-70.7, 21.47) * mm});
            skLineSegment(sketch, "E8.5.0.68", {"start": v(-73.47, 1.39) * mm, "end": v(-73.47, -1.39) * mm});
            skLineSegment(sketch, "E8.5.0.71", {"start": v(-73.47, -24.25) * mm, "end": v(-70.7, -24.25) * mm});
            skLineSegment(sketch, "E8.5.0.73", {"start": v(-73.47, 29.1) * mm, "end": v(-70.7, 29.1) * mm});
            skLineSegment(sketch, "E8.5.0.74", {"start": v(-73.47, 6.23) * mm, "end": v(-70.7, 6.23) * mm});
            skLineSegment(sketch, "E8.5.0.77", {"start": v(-73.47, 9) * mm, "end": v(-73.47, 6.23) * mm});
            skLineSegment(sketch, "E8.5.0.79", {"start": v(-73.47, -6.23) * mm, "end": v(-73.47, -9) * mm});
            skLineSegment(sketch, "E8.5.0.82", {"start": v(-73.47, -9) * mm, "end": v(-70.7, -9) * mm});
            skLineSegment(sketch, "E8.5.0.85", {"start": v(-73.47, 13.85) * mm, "end": v(-70.7, 13.85) * mm});
            skLineSegment(sketch, "E8.5.0.87", {"start": v(-73.47, 16.63) * mm, "end": v(-73.47, 13.85) * mm});
            skLineSegment(sketch, "E8.5.0.91", {"start": v(-73.47, -16.63) * mm, "end": v(-70.7, -16.63) * mm});
            skLineSegment(sketch, "E8.5.0.94", {"start": v(-73.47, 31.87) * mm, "end": v(-70.7, 31.87) * mm});
            skSolve(sketch);
        }
        {
            var Q0;
            Q0=makeQuery(id+"F0.imprint","IMPRINT",FACE,{"disambiguationData":[TD([[makeQuery(id+"F0.imprint","IMPRINT",EDGE,{"derivedFrom":sQuery(id+"F0.wireOp",EDGE,"E0.0")}),-1.0]])]});
            extrude(context, id + "F1", {"entities" : qUnion([Q0]), "depth" : 25.4 * mm});
        }
    });
